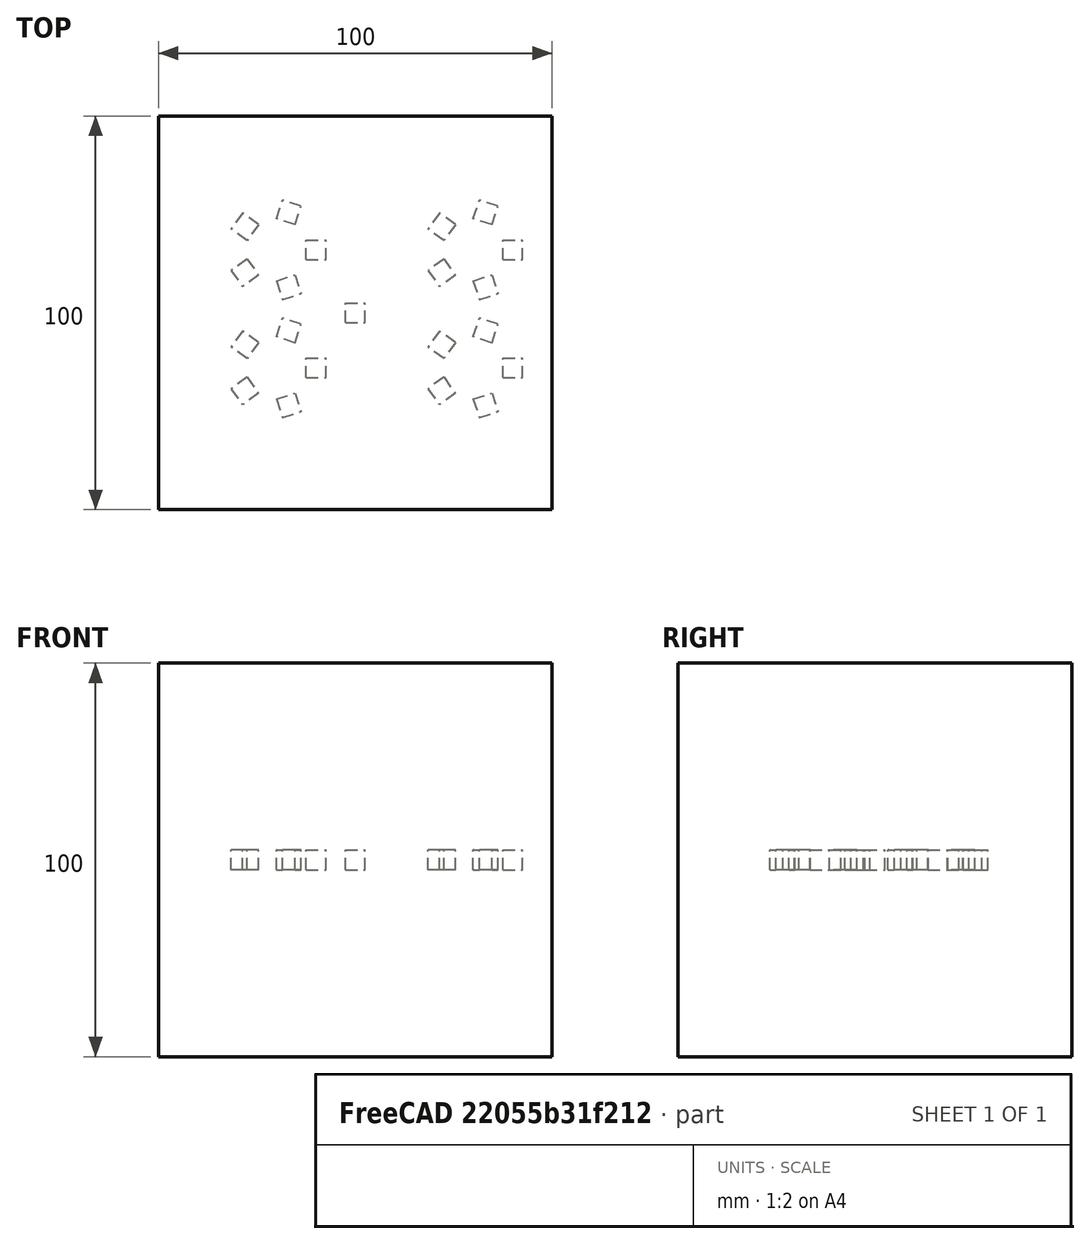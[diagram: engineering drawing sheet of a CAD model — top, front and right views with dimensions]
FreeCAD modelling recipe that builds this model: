
FCSTD DOCUMENT  (FreeCAD 1.0R39109 (Git))
Label: arrayTest-1
License: All rights reserved
LicenseURL: http://en.wikipedia.org/wiki/All_rights_reserved
objects: App::DocumentObjectGroupPython×1248, Part::FeaturePython×4, App::Part×3
note: 4 computed .brp shape members not serialized (recipe doc carries the construction recipe); baked Part::Feature solids carry a one-line shape summary decoded from their .brp

FEATURE [App::DocumentObjectGroupPython] HALFPI  # scripted group (container) (typed FeaturePython)
  name = HALFPI
  value = pi/2.
FEATURE [App::DocumentObjectGroupPython] PI  # scripted group (container) (typed FeaturePython)
  name = PI
  value = 1.*pi
FEATURE [App::DocumentObjectGroupPython] TWOPI  # scripted group (container) (typed FeaturePython)
  name = TWOPI
  value = 2.*pi
FEATURE [App::DocumentObjectGroupPython] Constants  # scripted group (container) (typed FeaturePython)
  Group = -> [HALFPI,PI,TWOPI]
FEATURE [App::DocumentObjectGroupPython] Variables  # scripted group (container) (typed FeaturePython)
FEATURE [App::DocumentObjectGroupPython] Quantities  # scripted group (container) (typed FeaturePython)
FEATURE [App::DocumentObjectGroupPython] Isotopes  # scripted group (container) (typed FeaturePython)
FEATURE [App::DocumentObjectGroupPython] Elements  # scripted group (container) (typed FeaturePython)
FEATURE [App::DocumentObjectGroupPython] G4Isotopes  # scripted group (container) (typed FeaturePython)
FEATURE [App::DocumentObjectGroupPython] H_element  # scripted group (container) (typed FeaturePython)
  Z = 1
  atom_value = 1.008
  formula = H
  name = H_element
FEATURE [App::DocumentObjectGroupPython] He_element  # scripted group (container) (typed FeaturePython)
  Z = 2
  atom_value = 4.0026
  formula = He
  name = He_element
FEATURE [App::DocumentObjectGroupPython] Li_element  # scripted group (container) (typed FeaturePython)
  Z = 3
  atom_value = 6.94
  formula = Li
  name = Li_element
FEATURE [App::DocumentObjectGroupPython] Be_element  # scripted group (container) (typed FeaturePython)
  Z = 4
  atom_value = 9.01218
  formula = Be
  name = Be_element
FEATURE [App::DocumentObjectGroupPython] B_element  # scripted group (container) (typed FeaturePython)
  Z = 5
  atom_value = 10.81
  formula = B
  name = B_element
FEATURE [App::DocumentObjectGroupPython] C_element  # scripted group (container) (typed FeaturePython)
  Z = 6
  atom_value = 12.011
  formula = C
  name = C_element
FEATURE [App::DocumentObjectGroupPython] N_element  # scripted group (container) (typed FeaturePython)
  Z = 7
  atom_value = 14.007
  formula = N
  name = N_element
FEATURE [App::DocumentObjectGroupPython] O_element  # scripted group (container) (typed FeaturePython)
  Z = 8
  atom_value = 15.999
  formula = O
  name = O_element
FEATURE [App::DocumentObjectGroupPython] F_element  # scripted group (container) (typed FeaturePython)
  Z = 9
  atom_value = 18.9984
  formula = F
  name = F_element
FEATURE [App::DocumentObjectGroupPython] Ne_element  # scripted group (container) (typed FeaturePython)
  Z = 10
  atom_value = 20.1797
  formula = Ne
  name = Ne_element
FEATURE [App::DocumentObjectGroupPython] Na_element  # scripted group (container) (typed FeaturePython)
  Z = 11
  atom_value = 22.9898
  formula = Na
  name = Na_element
FEATURE [App::DocumentObjectGroupPython] Mg_element  # scripted group (container) (typed FeaturePython)
  Z = 12
  atom_value = 24.305
  formula = Mg
  name = Mg_element
FEATURE [App::DocumentObjectGroupPython] Al_element  # scripted group (container) (typed FeaturePython)
  Z = 13
  atom_value = 26.9815
  formula = Al
  name = Al_element
FEATURE [App::DocumentObjectGroupPython] Si_element  # scripted group (container) (typed FeaturePython)
  Z = 14
  atom_value = 28.085
  formula = Si
  name = Si_element
FEATURE [App::DocumentObjectGroupPython] P_element  # scripted group (container) (typed FeaturePython)
  Z = 15
  atom_value = 30.9738
  formula = P
  name = P_element
FEATURE [App::DocumentObjectGroupPython] S_element  # scripted group (container) (typed FeaturePython)
  Z = 16
  atom_value = 32.06
  formula = S
  name = S_element
FEATURE [App::DocumentObjectGroupPython] Cl_element  # scripted group (container) (typed FeaturePython)
  Z = 17
  atom_value = 35.45
  formula = Cl
  name = Cl_element
FEATURE [App::DocumentObjectGroupPython] Ar_element  # scripted group (container) (typed FeaturePython)
  Z = 18
  atom_value = 39.95
  formula = Ar
  name = Ar_element
FEATURE [App::DocumentObjectGroupPython] K_element  # scripted group (container) (typed FeaturePython)
  Z = 19
  atom_value = 39.0983
  formula = K
  name = K_element
FEATURE [App::DocumentObjectGroupPython] Ca_element  # scripted group (container) (typed FeaturePython)
  Z = 20
  atom_value = 40.078
  formula = Ca
  name = Ca_element
FEATURE [App::DocumentObjectGroupPython] Sc_element  # scripted group (container) (typed FeaturePython)
  Z = 21
  atom_value = 44.9559
  formula = Sc
  name = Sc_element
FEATURE [App::DocumentObjectGroupPython] Ti_element  # scripted group (container) (typed FeaturePython)
  Z = 22
  atom_value = 47.867
  formula = Ti
  name = Ti_element
FEATURE [App::DocumentObjectGroupPython] V_element  # scripted group (container) (typed FeaturePython)
  Z = 23
  atom_value = 50.9415
  formula = V
  name = V_element
FEATURE [App::DocumentObjectGroupPython] Cr_element  # scripted group (container) (typed FeaturePython)
  Z = 24
  atom_value = 51.9961
  formula = Cr
  name = Cr_element
FEATURE [App::DocumentObjectGroupPython] Mn_element  # scripted group (container) (typed FeaturePython)
  Z = 25
  atom_value = 54.938
  formula = Mn
  name = Mn_element
FEATURE [App::DocumentObjectGroupPython] Fe_element  # scripted group (container) (typed FeaturePython)
  Z = 26
  atom_value = 55.845
  formula = Fe
  name = Fe_element
FEATURE [App::DocumentObjectGroupPython] Co_element  # scripted group (container) (typed FeaturePython)
  Z = 27
  atom_value = 58.9332
  formula = Co
  name = Co_element
FEATURE [App::DocumentObjectGroupPython] Ni_element  # scripted group (container) (typed FeaturePython)
  Z = 28
  atom_value = 58.6934
  formula = Ni
  name = Ni_element
FEATURE [App::DocumentObjectGroupPython] Cu_element  # scripted group (container) (typed FeaturePython)
  Z = 29
  atom_value = 63.546
  formula = Cu
  name = Cu_element
FEATURE [App::DocumentObjectGroupPython] Zn_element  # scripted group (container) (typed FeaturePython)
  Z = 30
  atom_value = 65.38
  formula = Zn
  name = Zn_element
FEATURE [App::DocumentObjectGroupPython] Ga_element  # scripted group (container) (typed FeaturePython)
  Z = 31
  atom_value = 69.723
  formula = Ga
  name = Ga_element
FEATURE [App::DocumentObjectGroupPython] Ge_element  # scripted group (container) (typed FeaturePython)
  Z = 32
  atom_value = 72.63
  formula = Ge
  name = Ge_element
FEATURE [App::DocumentObjectGroupPython] As_element  # scripted group (container) (typed FeaturePython)
  Z = 33
  atom_value = 74.9216
  formula = As
  name = As_element
FEATURE [App::DocumentObjectGroupPython] Se_element  # scripted group (container) (typed FeaturePython)
  Z = 34
  atom_value = 78.971
  formula = Se
  name = Se_element
FEATURE [App::DocumentObjectGroupPython] Br_element  # scripted group (container) (typed FeaturePython)
  Z = 35
  atom_value = 79.904
  formula = Br
  name = Br_element
FEATURE [App::DocumentObjectGroupPython] Kr_element  # scripted group (container) (typed FeaturePython)
  Z = 36
  atom_value = 83.798
  formula = Kr
  name = Kr_element
FEATURE [App::DocumentObjectGroupPython] Rb_element  # scripted group (container) (typed FeaturePython)
  Z = 37
  atom_value = 85.4678
  formula = Rb
  name = Rb_element
FEATURE [App::DocumentObjectGroupPython] Sr_element  # scripted group (container) (typed FeaturePython)
  Z = 38
  atom_value = 87.62
  formula = Sr
  name = Sr_element
FEATURE [App::DocumentObjectGroupPython] Y_element  # scripted group (container) (typed FeaturePython)
  Z = 39
  atom_value = 88.9058
  formula = Y
  name = Y_element
FEATURE [App::DocumentObjectGroupPython] Zr_element  # scripted group (container) (typed FeaturePython)
  Z = 40
  atom_value = 91.224
  formula = Zr
  name = Zr_element
FEATURE [App::DocumentObjectGroupPython] Nb_element  # scripted group (container) (typed FeaturePython)
  Z = 41
  atom_value = 92.9064
  formula = Nb
  name = Nb_element
FEATURE [App::DocumentObjectGroupPython] Mo_element  # scripted group (container) (typed FeaturePython)
  Z = 42
  atom_value = 95.95
  formula = Mo
  name = Mo_element
FEATURE [App::DocumentObjectGroupPython] Tc_element  # scripted group (container) (typed FeaturePython)
  Z = 43
  atom_value = 97
  formula = Tc
  name = Tc_element
FEATURE [App::DocumentObjectGroupPython] Ru_element  # scripted group (container) (typed FeaturePython)
  Z = 44
  atom_value = 101.07
  formula = Ru
  name = Ru_element
FEATURE [App::DocumentObjectGroupPython] Rh_element  # scripted group (container) (typed FeaturePython)
  Z = 45
  atom_value = 102.905
  formula = Rh
  name = Rh_element
FEATURE [App::DocumentObjectGroupPython] Pd_element  # scripted group (container) (typed FeaturePython)
  Z = 46
  atom_value = 106.42
  formula = Pd
  name = Pd_element
FEATURE [App::DocumentObjectGroupPython] Ag_element  # scripted group (container) (typed FeaturePython)
  Z = 47
  atom_value = 107.868
  formula = Ag
  name = Ag_element
FEATURE [App::DocumentObjectGroupPython] Cd_element  # scripted group (container) (typed FeaturePython)
  Z = 48
  atom_value = 112.414
  formula = Cd
  name = Cd_element
FEATURE [App::DocumentObjectGroupPython] In_element  # scripted group (container) (typed FeaturePython)
  Z = 49
  atom_value = 114.818
  formula = In
  name = In_element
FEATURE [App::DocumentObjectGroupPython] Sn_element  # scripted group (container) (typed FeaturePython)
  Z = 50
  atom_value = 118.71
  formula = Sn
  name = Sn_element
FEATURE [App::DocumentObjectGroupPython] Sb_element  # scripted group (container) (typed FeaturePython)
  Z = 51
  atom_value = 121.76
  formula = Sb
  name = Sb_element
FEATURE [App::DocumentObjectGroupPython] Te_element  # scripted group (container) (typed FeaturePython)
  Z = 52
  atom_value = 127.6
  formula = Te
  name = Te_element
FEATURE [App::DocumentObjectGroupPython] I_element  # scripted group (container) (typed FeaturePython)
  Z = 53
  atom_value = 126.904
  formula = I
  name = I_element
FEATURE [App::DocumentObjectGroupPython] Xe_element  # scripted group (container) (typed FeaturePython)
  Z = 54
  atom_value = 131.293
  formula = Xe
  name = Xe_element
FEATURE [App::DocumentObjectGroupPython] Cs_element  # scripted group (container) (typed FeaturePython)
  Z = 55
  atom_value = 132.905
  formula = Cs
  name = Cs_element
FEATURE [App::DocumentObjectGroupPython] Ba_element  # scripted group (container) (typed FeaturePython)
  Z = 56
  atom_value = 137.327
  formula = Ba
  name = Ba_element
FEATURE [App::DocumentObjectGroupPython] La_element  # scripted group (container) (typed FeaturePython)
  Z = 57
  atom_value = 138.905
  formula = La
  name = La_element
FEATURE [App::DocumentObjectGroupPython] Ce_element  # scripted group (container) (typed FeaturePython)
  Z = 58
  atom_value = 140.116
  formula = Ce
  name = Ce_element
FEATURE [App::DocumentObjectGroupPython] Pr_element  # scripted group (container) (typed FeaturePython)
  Z = 59
  atom_value = 140.908
  formula = Pr
  name = Pr_element
FEATURE [App::DocumentObjectGroupPython] Nd_element  # scripted group (container) (typed FeaturePython)
  Z = 60
  atom_value = 144.242
  formula = Nd
  name = Nd_element
FEATURE [App::DocumentObjectGroupPython] Pm_element  # scripted group (container) (typed FeaturePython)
  Z = 61
  atom_value = 145
  formula = Pm
  name = Pm_element
FEATURE [App::DocumentObjectGroupPython] Sm_element  # scripted group (container) (typed FeaturePython)
  Z = 62
  atom_value = 150.36
  formula = Sm
  name = Sm_element
FEATURE [App::DocumentObjectGroupPython] Eu_element  # scripted group (container) (typed FeaturePython)
  Z = 63
  atom_value = 151.964
  formula = Eu
  name = Eu_element
FEATURE [App::DocumentObjectGroupPython] Gd_element  # scripted group (container) (typed FeaturePython)
  Z = 64
  atom_value = 157.25
  formula = Gd
  name = Gd_element
FEATURE [App::DocumentObjectGroupPython] Tb_element  # scripted group (container) (typed FeaturePython)
  Z = 65
  atom_value = 158.925
  formula = Tb
  name = Tb_element
FEATURE [App::DocumentObjectGroupPython] Dy_element  # scripted group (container) (typed FeaturePython)
  Z = 66
  atom_value = 162.5
  formula = Dy
  name = Dy_element
FEATURE [App::DocumentObjectGroupPython] Ho_element  # scripted group (container) (typed FeaturePython)
  Z = 67
  atom_value = 164.93
  formula = Ho
  name = Ho_element
FEATURE [App::DocumentObjectGroupPython] Er_element  # scripted group (container) (typed FeaturePython)
  Z = 68
  atom_value = 167.259
  formula = Er
  name = Er_element
FEATURE [App::DocumentObjectGroupPython] Tm_element  # scripted group (container) (typed FeaturePython)
  Z = 69
  atom_value = 168.934
  formula = Tm
  name = Tm_element
FEATURE [App::DocumentObjectGroupPython] Yb_element  # scripted group (container) (typed FeaturePython)
  Z = 70
  atom_value = 173.045
  formula = Yb
  name = Yb_element
FEATURE [App::DocumentObjectGroupPython] Lu_element  # scripted group (container) (typed FeaturePython)
  Z = 71
  atom_value = 174.967
  formula = Lu
  name = Lu_element
FEATURE [App::DocumentObjectGroupPython] Hf_element  # scripted group (container) (typed FeaturePython)
  Z = 72
  atom_value = 178.49
  formula = Hf
  name = Hf_element
FEATURE [App::DocumentObjectGroupPython] Ta_element  # scripted group (container) (typed FeaturePython)
  Z = 73
  atom_value = 180.948
  formula = Ta
  name = Ta_element
FEATURE [App::DocumentObjectGroupPython] W_element  # scripted group (container) (typed FeaturePython)
  Z = 74
  atom_value = 183.84
  formula = W
  name = W_element
FEATURE [App::DocumentObjectGroupPython] Re_element  # scripted group (container) (typed FeaturePython)
  Z = 75
  atom_value = 186.207
  formula = Re
  name = Re_element
FEATURE [App::DocumentObjectGroupPython] Os_element  # scripted group (container) (typed FeaturePython)
  Z = 76
  atom_value = 190.23
  formula = Os
  name = Os_element
FEATURE [App::DocumentObjectGroupPython] Ir_element  # scripted group (container) (typed FeaturePython)
  Z = 77
  atom_value = 192.217
  formula = Ir
  name = Ir_element
FEATURE [App::DocumentObjectGroupPython] Pt_element  # scripted group (container) (typed FeaturePython)
  Z = 78
  atom_value = 195.084
  formula = Pt
  name = Pt_element
FEATURE [App::DocumentObjectGroupPython] Au_element  # scripted group (container) (typed FeaturePython)
  Z = 79
  atom_value = 196.967
  formula = Au
  name = Au_element
FEATURE [App::DocumentObjectGroupPython] Hg_element  # scripted group (container) (typed FeaturePython)
  Z = 80
  atom_value = 200.592
  formula = Hg
  name = Hg_element
FEATURE [App::DocumentObjectGroupPython] Tl_element  # scripted group (container) (typed FeaturePython)
  Z = 81
  atom_value = 204.38
  formula = Tl
  name = Tl_element
FEATURE [App::DocumentObjectGroupPython] Pb_element  # scripted group (container) (typed FeaturePython)
  Z = 82
  atom_value = 207.2
  formula = Pb
  name = Pb_element
FEATURE [App::DocumentObjectGroupPython] Bi_element  # scripted group (container) (typed FeaturePython)
  Z = 83
  atom_value = 208.98
  formula = Bi
  name = Bi_element
FEATURE [App::DocumentObjectGroupPython] Po_element  # scripted group (container) (typed FeaturePython)
  Z = 84
  atom_value = 209
  formula = Po
  name = Po_element
FEATURE [App::DocumentObjectGroupPython] At_element  # scripted group (container) (typed FeaturePython)
  Z = 85
  atom_value = 210
  formula = At
  name = At_element
FEATURE [App::DocumentObjectGroupPython] Rn_element  # scripted group (container) (typed FeaturePython)
  Z = 86
  atom_value = 222
  formula = Rn
  name = Rn_element
FEATURE [App::DocumentObjectGroupPython] Fr_element  # scripted group (container) (typed FeaturePython)
  Z = 87
  atom_value = 223
  formula = Fr
  name = Fr_element
FEATURE [App::DocumentObjectGroupPython] Ra_element  # scripted group (container) (typed FeaturePython)
  Z = 88
  atom_value = 226
  formula = Ra
  name = Ra_element
FEATURE [App::DocumentObjectGroupPython] Ac_element  # scripted group (container) (typed FeaturePython)
  Z = 89
  atom_value = 227
  formula = Ac
  name = Ac_element
FEATURE [App::DocumentObjectGroupPython] Th_element  # scripted group (container) (typed FeaturePython)
  Z = 90
  atom_value = 232.038
  formula = Th
  name = Th_element
FEATURE [App::DocumentObjectGroupPython] Pa_element  # scripted group (container) (typed FeaturePython)
  Z = 91
  atom_value = 231.036
  formula = Pa
  name = Pa_element
FEATURE [App::DocumentObjectGroupPython] U_element  # scripted group (container) (typed FeaturePython)
  Z = 92
  atom_value = 238.029
  formula = U
  name = U_element
FEATURE [App::DocumentObjectGroupPython] Np_element  # scripted group (container) (typed FeaturePython)
  Z = 93
  atom_value = 237
  formula = Np
  name = Np_element
FEATURE [App::DocumentObjectGroupPython] Pu_element  # scripted group (container) (typed FeaturePython)
  Z = 94
  atom_value = 244
  formula = Pu
  name = Pu_element
FEATURE [App::DocumentObjectGroupPython] Am_element  # scripted group (container) (typed FeaturePython)
  Z = 95
  atom_value = 243
  formula = Am
  name = Am_element
FEATURE [App::DocumentObjectGroupPython] Cm_element  # scripted group (container) (typed FeaturePython)
  Z = 96
  atom_value = 247
  formula = Cm
  name = Cm_element
FEATURE [App::DocumentObjectGroupPython] Bk_element  # scripted group (container) (typed FeaturePython)
  Z = 97
  atom_value = 247
  formula = Bk
  name = Bk_element
FEATURE [App::DocumentObjectGroupPython] Cf_element  # scripted group (container) (typed FeaturePython)
  Z = 98
  atom_value = 251
  formula = Cf
  name = Cf_element
FEATURE [App::DocumentObjectGroupPython] G4Elements  # scripted group (container) (typed FeaturePython)
  Group = -> [H_element,He_element,Li_element,Be_element,B_element,C_element,N_element,O_element,F_element,Ne_element,Na_element,Mg_element,Al_element,Si_element,P_element,S_element,Cl_element,Ar_element,K_element,Ca_element,Sc_element,Ti_element,V_element,Cr_element,Mn_element,Fe_element,Co_element,Ni_element,Cu_element,Zn_element,Ga_element,Ge_element,As_element,Se_element,Br_element,Kr_element,Rb_element,+61 more]
FEATURE [App::DocumentObjectGroupPython] H_element001  label="H_element : 0.101"  # scripted group (container) (typed FeaturePython)
  n = 0.101327
FEATURE [App::DocumentObjectGroupPython] C_element001  label="C_element : 0.775"  # scripted group (container) (typed FeaturePython)
  n = 0.7755
FEATURE [App::DocumentObjectGroupPython] N_element001  label="N_element : 0.035"  # scripted group (container) (typed FeaturePython)
  n = 0.035057
FEATURE [App::DocumentObjectGroupPython] O_element001  label="O_element : 0.052"  # scripted group (container) (typed FeaturePython)
  n = 0.0523159
FEATURE [App::DocumentObjectGroupPython] F_element001  label="F_element : 0.017"  # scripted group (container) (typed FeaturePython)
  n = 0.017422
FEATURE [App::DocumentObjectGroupPython] Ca_element001  label="Ca_element : 0.018"  # scripted group (container) (typed FeaturePython)
  n = 0.018378
FEATURE [App::DocumentObjectGroupPython] G4_A_150_TISSUE  label="G4_A-150_TISSUE"  # scripted group (container) (typed FeaturePython)
  Dunit = g/cm3
  Dvalue = 1.127
  Group = -> [H_element001,C_element001,N_element001,O_element001,F_element001,Ca_element001]
  conduct = 2
  density = 1
  expand = 3
  formula = G4_A-150_TISSUE
  name = G4_A-150_TISSUE
  specific = 4
FEATURE [App::DocumentObjectGroupPython] C_element002  label="C_element : 3"  # scripted group (container) (typed FeaturePython)
  n = 3
  ref = C_element
FEATURE [App::DocumentObjectGroupPython] H_element002  label="H_element : 6"  # scripted group (container) (typed FeaturePython)
  n = 6
  ref = H_element
FEATURE [App::DocumentObjectGroupPython] O_element002  label="O_element : 1"  # scripted group (container) (typed FeaturePython)
  n = 1
  ref = O_element
FEATURE [App::DocumentObjectGroupPython] G4_ACETONE  # scripted group (container) (typed FeaturePython)
  Dunit = g/cm3
  Dvalue = 0.7899
  Group = -> [C_element002,H_element002,O_element002]
  conduct = 2
  density = 1
  expand = 3
  formula = G4_ACETONE
  name = G4_ACETONE
  specific = 4
FEATURE [App::DocumentObjectGroupPython] C_element003  label="C_element : 2"  # scripted group (container) (typed FeaturePython)
  n = 2
  ref = C_element
FEATURE [App::DocumentObjectGroupPython] H_element003  label="H_element : 2"  # scripted group (container) (typed FeaturePython)
  n = 2
  ref = H_element
FEATURE [App::DocumentObjectGroupPython] G4_ACETYLENE  # scripted group (container) (typed FeaturePython)
  Dunit = g/cm3
  Dvalue = 0.0010967
  Group = -> [C_element003,H_element003]
  conduct = 2
  density = 1
  expand = 3
  formula = G4_ACETYLENE
  name = G4_ACETYLENE
  specific = 4
FEATURE [App::DocumentObjectGroupPython] C_element004  label="C_element : 5"  # scripted group (container) (typed FeaturePython)
  n = 5
  ref = C_element
FEATURE [App::DocumentObjectGroupPython] H_element004  label="H_element : 5"  # scripted group (container) (typed FeaturePython)
  n = 5
  ref = H_element
FEATURE [App::DocumentObjectGroupPython] N_element002  label="N_element : 5"  # scripted group (container) (typed FeaturePython)
  n = 5
  ref = N_element
FEATURE [App::DocumentObjectGroupPython] G4_ADENINE  # scripted group (container) (typed FeaturePython)
  Dunit = g/cm3
  Dvalue = 1.6
  Group = -> [C_element004,H_element004,N_element002]
  conduct = 2
  density = 1
  expand = 3
  formula = G4_ADENINE
  name = G4_ADENINE
  specific = 4
FEATURE [App::DocumentObjectGroupPython] H_element005  label="H_element : 0.114"  # scripted group (container) (typed FeaturePython)
  n = 0.114
FEATURE [App::DocumentObjectGroupPython] C_element005  label="C_element : 0.598"  # scripted group (container) (typed FeaturePython)
  n = 0.598
FEATURE [App::DocumentObjectGroupPython] N_element003  label="N_element : 0.007"  # scripted group (container) (typed FeaturePython)
  n = 0.007
FEATURE [App::DocumentObjectGroupPython] O_element003  label="O_element : 0.278"  # scripted group (container) (typed FeaturePython)
  n = 0.278
FEATURE [App::DocumentObjectGroupPython] Na_element001  label="Na_element : 0.001"  # scripted group (container) (typed FeaturePython)
  n = 0.001
FEATURE [App::DocumentObjectGroupPython] S_element001  label="S_element : 0.001"  # scripted group (container) (typed FeaturePython)
  n = 0.001
FEATURE [App::DocumentObjectGroupPython] Cl_element001  label="Cl_element : 0.001"  # scripted group (container) (typed FeaturePython)
  n = 0.001
FEATURE [App::DocumentObjectGroupPython] G4_ADIPOSE_TISSUE_ICRP  # scripted group (container) (typed FeaturePython)
  Dunit = g/cm3
  Dvalue = 0.95
  Group = -> [H_element005,C_element005,N_element003,O_element003,Na_element001,S_element001,Cl_element001]
  conduct = 2
  density = 1
  expand = 3
  formula = G4_ADIPOSE_TISSUE_ICRP
  name = G4_ADIPOSE_TISSUE_ICRP
  specific = 4
FEATURE [App::DocumentObjectGroupPython] C_element006  label="C_element : 0.000"  # scripted group (container) (typed FeaturePython)
  n = 0.000124
FEATURE [App::DocumentObjectGroupPython] N_element004  label="N_element : 0.755"  # scripted group (container) (typed FeaturePython)
  n = 0.755268
FEATURE [App::DocumentObjectGroupPython] O_element004  label="O_element : 0.232"  # scripted group (container) (typed FeaturePython)
  n = 0.231781
FEATURE [App::DocumentObjectGroupPython] Ar_element001  label="Ar_element : 0.013"  # scripted group (container) (typed FeaturePython)
  n = 0.012827
FEATURE [App::DocumentObjectGroupPython] G4_AIR  # scripted group (container) (typed FeaturePython)
  Dunit = g/cm3
  Dvalue = 0.00120479
  Group = -> [C_element006,N_element004,O_element004,Ar_element001]
  conduct = 2
  density = 1
  expand = 3
  formula = G4_AIR
  name = G4_AIR
  specific = 4
FEATURE [App::DocumentObjectGroupPython] C_element007  label="C_element : 006"  # scripted group (container) (typed FeaturePython)
  n = 3
  ref = C_element
FEATURE [App::DocumentObjectGroupPython] H_element006  label="H_element : 7"  # scripted group (container) (typed FeaturePython)
  n = 7
  ref = H_element
FEATURE [App::DocumentObjectGroupPython] N_element005  label="N_element : 1"  # scripted group (container) (typed FeaturePython)
  n = 1
  ref = N_element
FEATURE [App::DocumentObjectGroupPython] O_element005  label="O_element : 2"  # scripted group (container) (typed FeaturePython)
  n = 2
  ref = O_element
FEATURE [App::DocumentObjectGroupPython] G4_ALANINE  # scripted group (container) (typed FeaturePython)
  Dunit = g/cm3
  Dvalue = 1.42
  Group = -> [C_element007,H_element006,N_element005,O_element005]
  conduct = 2
  density = 1
  expand = 3
  formula = G4_ALANINE
  name = G4_ALANINE
  specific = 4
FEATURE [App::DocumentObjectGroupPython] Al_element001  label="Al_element : 2"  # scripted group (container) (typed FeaturePython)
  n = 2
  ref = Al_element
FEATURE [App::DocumentObjectGroupPython] O_element006  label="O_element : 3"  # scripted group (container) (typed FeaturePython)
  n = 3
  ref = O_element
FEATURE [App::DocumentObjectGroupPython] G4_ALUMINUM_OXIDE  # scripted group (container) (typed FeaturePython)
  Dunit = g/cm3
  Dvalue = 3.97
  Group = -> [Al_element001,O_element006]
  conduct = 2
  density = 1
  expand = 3
  formula = G4_ALUMINUM_OXIDE
  name = G4_ALUMINUM_OXIDE
  specific = 4
FEATURE [App::DocumentObjectGroupPython] H_element007  label="H_element : 0.106"  # scripted group (container) (typed FeaturePython)
  n = 0.10593
FEATURE [App::DocumentObjectGroupPython] C_element008  label="C_element : 0.789"  # scripted group (container) (typed FeaturePython)
  n = 0.788974
FEATURE [App::DocumentObjectGroupPython] O_element007  label="O_element : 0.105"  # scripted group (container) (typed FeaturePython)
  n = 0.105096
FEATURE [App::DocumentObjectGroupPython] G4_AMBER  # scripted group (container) (typed FeaturePython)
  Dunit = g/cm3
  Dvalue = 1.1
  Group = -> [H_element007,C_element008,O_element007]
  conduct = 2
  density = 1
  expand = 3
  formula = G4_AMBER
  name = G4_AMBER
  specific = 4
FEATURE [App::DocumentObjectGroupPython] N_element006  label="N_element : 006"  # scripted group (container) (typed FeaturePython)
  n = 1
  ref = N_element
FEATURE [App::DocumentObjectGroupPython] H_element008  label="H_element : 3"  # scripted group (container) (typed FeaturePython)
  n = 3
  ref = H_element
FEATURE [App::DocumentObjectGroupPython] G4_AMMONIA  # scripted group (container) (typed FeaturePython)
  Dunit = g/cm3
  Dvalue = 0.000826019
  Group = -> [N_element006,H_element008]
  conduct = 2
  density = 1
  expand = 3
  formula = G4_AMMONIA
  name = G4_AMMONIA
  specific = 4
FEATURE [App::DocumentObjectGroupPython] C_element009  label="C_element : 6"  # scripted group (container) (typed FeaturePython)
  n = 6
  ref = C_element
FEATURE [App::DocumentObjectGroupPython] H_element009  label="H_element : 008"  # scripted group (container) (typed FeaturePython)
  n = 7
  ref = H_element
FEATURE [App::DocumentObjectGroupPython] N_element007  label="N_element : 007"  # scripted group (container) (typed FeaturePython)
  n = 1
  ref = N_element
FEATURE [App::DocumentObjectGroupPython] G4_ANILINE  # scripted group (container) (typed FeaturePython)
  Dunit = g/cm3
  Dvalue = 1.0235
  Group = -> [C_element009,H_element009,N_element007]
  conduct = 2
  density = 1
  expand = 3
  formula = G4_ANILINE
  name = G4_ANILINE
  specific = 4
FEATURE [App::DocumentObjectGroupPython] C_element010  label="C_element : 14"  # scripted group (container) (typed FeaturePython)
  n = 14
  ref = C_element
FEATURE [App::DocumentObjectGroupPython] H_element010  label="H_element : 10"  # scripted group (container) (typed FeaturePython)
  n = 10
  ref = H_element
FEATURE [App::DocumentObjectGroupPython] G4_ANTHRACENE  # scripted group (container) (typed FeaturePython)
  Dunit = g/cm3
  Dvalue = 1.283
  Group = -> [C_element010,H_element010]
  conduct = 2
  density = 1
  expand = 3
  formula = G4_ANTHRACENE
  name = G4_ANTHRACENE
  specific = 4
FEATURE [App::DocumentObjectGroupPython] H_element011  label="H_element : 0.065"  # scripted group (container) (typed FeaturePython)
  n = 0.0654709
FEATURE [App::DocumentObjectGroupPython] C_element011  label="C_element : 0.537"  # scripted group (container) (typed FeaturePython)
  n = 0.536944
FEATURE [App::DocumentObjectGroupPython] N_element008  label="N_element : 0.021"  # scripted group (container) (typed FeaturePython)
  n = 0.0215
FEATURE [App::DocumentObjectGroupPython] O_element008  label="O_element : 0.032"  # scripted group (container) (typed FeaturePython)
  n = 0.032085
FEATURE [App::DocumentObjectGroupPython] F_element002  label="F_element : 0.167"  # scripted group (container) (typed FeaturePython)
  n = 0.167411
FEATURE [App::DocumentObjectGroupPython] Ca_element002  label="Ca_element : 0.177"  # scripted group (container) (typed FeaturePython)
  n = 0.176589
FEATURE [App::DocumentObjectGroupPython] G4_B_100_BONE  label="G4_B-100_BONE"  # scripted group (container) (typed FeaturePython)
  Dunit = g/cm3
  Dvalue = 1.45
  Group = -> [H_element011,C_element011,N_element008,O_element008,F_element002,Ca_element002]
  conduct = 2
  density = 1
  expand = 3
  formula = G4_B-100_BONE
  name = G4_B-100_BONE
  specific = 4
FEATURE [App::DocumentObjectGroupPython] H_element012  label="H_element : 0.057"  # scripted group (container) (typed FeaturePython)
  n = 0.057441
FEATURE [App::DocumentObjectGroupPython] C_element012  label="C_element : 0.790"  # scripted group (container) (typed FeaturePython)
  n = 0.774591
FEATURE [App::DocumentObjectGroupPython] O_element009  label="O_element : 0.168"  # scripted group (container) (typed FeaturePython)
  n = 0.167968
FEATURE [App::DocumentObjectGroupPython] G4_BAKELITE  # scripted group (container) (typed FeaturePython)
  Dunit = g/cm3
  Dvalue = 1.25
  Group = -> [H_element012,C_element012,O_element009]
  conduct = 2
  density = 1
  expand = 3
  formula = G4_BAKELITE
  name = G4_BAKELITE
  specific = 4
FEATURE [App::DocumentObjectGroupPython] Ba_element001  label="Ba_element : 1"  # scripted group (container) (typed FeaturePython)
  n = 1
  ref = Ba_element
FEATURE [App::DocumentObjectGroupPython] F_element003  label="F_element : 2"  # scripted group (container) (typed FeaturePython)
  n = 2
  ref = F_element
FEATURE [App::DocumentObjectGroupPython] G4_BARIUM_FLUORIDE  # scripted group (container) (typed FeaturePython)
  Dunit = g/cm3
  Dvalue = 4.89
  Group = -> [Ba_element001,F_element003]
  conduct = 2
  density = 1
  expand = 3
  formula = G4_BARIUM_FLUORIDE
  name = G4_BARIUM_FLUORIDE
  specific = 4
FEATURE [App::DocumentObjectGroupPython] Ba_element002  label="Ba_element : 002"  # scripted group (container) (typed FeaturePython)
  n = 1
  ref = Ba_element
FEATURE [App::DocumentObjectGroupPython] S_element002  label="S_element : 1"  # scripted group (container) (typed FeaturePython)
  n = 1
  ref = S_element
FEATURE [App::DocumentObjectGroupPython] O_element010  label="O_element : 4"  # scripted group (container) (typed FeaturePython)
  n = 4
  ref = O_element
FEATURE [App::DocumentObjectGroupPython] G4_BARIUM_SULFATE  # scripted group (container) (typed FeaturePython)
  Dunit = g/cm3
  Dvalue = 4.5
  Group = -> [Ba_element002,S_element002,O_element010]
  conduct = 2
  density = 1
  expand = 3
  formula = G4_BARIUM_SULFATE
  name = G4_BARIUM_SULFATE
  specific = 4
FEATURE [App::DocumentObjectGroupPython] C_element013  label="C_element : 007"  # scripted group (container) (typed FeaturePython)
  n = 6
  ref = C_element
FEATURE [App::DocumentObjectGroupPython] H_element013  label="H_element : 009"  # scripted group (container) (typed FeaturePython)
  n = 6
  ref = H_element
FEATURE [App::DocumentObjectGroupPython] G4_BENZENE  # scripted group (container) (typed FeaturePython)
  Dunit = g/cm3
  Dvalue = 0.87865
  Group = -> [C_element013,H_element013]
  conduct = 2
  density = 1
  expand = 3
  formula = G4_BENZENE
  name = G4_BENZENE
  specific = 4
FEATURE [App::DocumentObjectGroupPython] Be_element001  label="Be_element : 1"  # scripted group (container) (typed FeaturePython)
  n = 1
  ref = Be_element
FEATURE [App::DocumentObjectGroupPython] O_element011  label="O_element : 005"  # scripted group (container) (typed FeaturePython)
  n = 1
  ref = O_element
FEATURE [App::DocumentObjectGroupPython] G4_BERYLLIUM_OXIDE  # scripted group (container) (typed FeaturePython)
  Dunit = g/cm3
  Dvalue = 3.01
  Group = -> [Be_element001,O_element011]
  conduct = 2
  density = 1
  expand = 3
  formula = G4_BERYLLIUM_OXIDE
  name = G4_BERYLLIUM_OXIDE
  specific = 4
FEATURE [App::DocumentObjectGroupPython] Bi_element001  label="Bi_element : 4"  # scripted group (container) (typed FeaturePython)
  n = 4
  ref = Bi_element
FEATURE [App::DocumentObjectGroupPython] Ge_element001  label="Ge_element : 3"  # scripted group (container) (typed FeaturePython)
  n = 3
  ref = Ge_element
FEATURE [App::DocumentObjectGroupPython] O_element012  label="O_element : 12"  # scripted group (container) (typed FeaturePython)
  n = 12
  ref = O_element
FEATURE [App::DocumentObjectGroupPython] G4_BGO  # scripted group (container) (typed FeaturePython)
  Dunit = g/cm3
  Dvalue = 7.13
  Group = -> [Bi_element001,Ge_element001,O_element012]
  conduct = 2
  density = 1
  expand = 3
  formula = G4_BGO
  name = G4_BGO
  specific = 4
FEATURE [App::DocumentObjectGroupPython] H_element014  label="H_element : 0.102"  # scripted group (container) (typed FeaturePython)
  n = 0.102
FEATURE [App::DocumentObjectGroupPython] C_element014  label="C_element : 0.110"  # scripted group (container) (typed FeaturePython)
  n = 0.11
FEATURE [App::DocumentObjectGroupPython] N_element009  label="N_element : 0.033"  # scripted group (container) (typed FeaturePython)
  n = 0.033
FEATURE [App::DocumentObjectGroupPython] O_element013  label="O_element : 0.745"  # scripted group (container) (typed FeaturePython)
  n = 0.745
FEATURE [App::DocumentObjectGroupPython] Na_element002  label="Na_element : 0.002"  # scripted group (container) (typed FeaturePython)
  n = 0.001
FEATURE [App::DocumentObjectGroupPython] P_element001  label="P_element : 0.001"  # scripted group (container) (typed FeaturePython)
  n = 0.001
FEATURE [App::DocumentObjectGroupPython] S_element003  label="S_element : 0.002"  # scripted group (container) (typed FeaturePython)
  n = 0.002
FEATURE [App::DocumentObjectGroupPython] Cl_element002  label="Cl_element : 0.003"  # scripted group (container) (typed FeaturePython)
  n = 0.003
FEATURE [App::DocumentObjectGroupPython] K_element001  label="K_element : 0.002"  # scripted group (container) (typed FeaturePython)
  n = 0.002
FEATURE [App::DocumentObjectGroupPython] Fe_element001  label="Fe_element : 0.001"  # scripted group (container) (typed FeaturePython)
  n = 0.001
FEATURE [App::DocumentObjectGroupPython] G4_BLOOD_ICRP  # scripted group (container) (typed FeaturePython)
  Dunit = g/cm3
  Dvalue = 1.06
  Group = -> [H_element014,C_element014,N_element009,O_element013,Na_element002,P_element001,S_element003,Cl_element002,K_element001,Fe_element001]
  conduct = 2
  density = 1
  expand = 3
  formula = G4_BLOOD_ICRP
  name = G4_BLOOD_ICRP
  specific = 4
FEATURE [App::DocumentObjectGroupPython] H_element015  label="H_element : 0.064"  # scripted group (container) (typed FeaturePython)
  n = 0.064
FEATURE [App::DocumentObjectGroupPython] C_element015  label="C_element : 0.278"  # scripted group (container) (typed FeaturePython)
  n = 0.278
FEATURE [App::DocumentObjectGroupPython] N_element010  label="N_element : 0.027"  # scripted group (container) (typed FeaturePython)
  n = 0.027
FEATURE [App::DocumentObjectGroupPython] O_element014  label="O_element : 0.410"  # scripted group (container) (typed FeaturePython)
  n = 0.41
FEATURE [App::DocumentObjectGroupPython] Mg_element001  label="Mg_element : 0.002"  # scripted group (container) (typed FeaturePython)
  n = 0.002
FEATURE [App::DocumentObjectGroupPython] P_element002  label="P_element : 0.070"  # scripted group (container) (typed FeaturePython)
  n = 0.07
FEATURE [App::DocumentObjectGroupPython] S_element004  label="S_element : 0.003"  # scripted group (container) (typed FeaturePython)
  n = 0.002
FEATURE [App::DocumentObjectGroupPython] Ca_element003  label="Ca_element : 0.147"  # scripted group (container) (typed FeaturePython)
  n = 0.147
FEATURE [App::DocumentObjectGroupPython] G4_BONE_COMPACT_ICRU  # scripted group (container) (typed FeaturePython)
  Dunit = g/cm3
  Dvalue = 1.85
  Group = -> [H_element015,C_element015,N_element010,O_element014,Mg_element001,P_element002,S_element004,Ca_element003]
  conduct = 2
  density = 1
  expand = 3
  formula = G4_BONE_COMPACT_ICRU
  name = G4_BONE_COMPACT_ICRU
  specific = 4
FEATURE [App::DocumentObjectGroupPython] H_element016  label="H_element : 0.034"  # scripted group (container) (typed FeaturePython)
  n = 0.034
FEATURE [App::DocumentObjectGroupPython] C_element016  label="C_element : 0.155"  # scripted group (container) (typed FeaturePython)
  n = 0.155
FEATURE [App::DocumentObjectGroupPython] N_element011  label="N_element : 0.042"  # scripted group (container) (typed FeaturePython)
  n = 0.042
FEATURE [App::DocumentObjectGroupPython] O_element015  label="O_element : 0.435"  # scripted group (container) (typed FeaturePython)
  n = 0.435
FEATURE [App::DocumentObjectGroupPython] Na_element003  label="Na_element : 0.003"  # scripted group (container) (typed FeaturePython)
  n = 0.001
FEATURE [App::DocumentObjectGroupPython] Mg_element002  label="Mg_element : 0.003"  # scripted group (container) (typed FeaturePython)
  n = 0.002
FEATURE [App::DocumentObjectGroupPython] P_element003  label="P_element : 0.103"  # scripted group (container) (typed FeaturePython)
  n = 0.103
FEATURE [App::DocumentObjectGroupPython] S_element005  label="S_element : 0.004"  # scripted group (container) (typed FeaturePython)
  n = 0.003
FEATURE [App::DocumentObjectGroupPython] Ca_element004  label="Ca_element : 0.225"  # scripted group (container) (typed FeaturePython)
  n = 0.225
FEATURE [App::DocumentObjectGroupPython] G4_BONE_CORTICAL_ICRP  # scripted group (container) (typed FeaturePython)
  Dunit = g/cm3
  Dvalue = 1.92
  Group = -> [H_element016,C_element016,N_element011,O_element015,Na_element003,Mg_element002,P_element003,S_element005,Ca_element004]
  conduct = 2
  density = 1
  expand = 3
  formula = G4_BONE_CORTICAL_ICRP
  name = G4_BONE_CORTICAL_ICRP
  specific = 4
FEATURE [App::DocumentObjectGroupPython] B_element001  label="B_element : 4"  # scripted group (container) (typed FeaturePython)
  n = 4
  ref = B_element
FEATURE [App::DocumentObjectGroupPython] C_element017  label="C_element : 1"  # scripted group (container) (typed FeaturePython)
  n = 1
  ref = C_element
FEATURE [App::DocumentObjectGroupPython] G4_BORON_CARBIDE  # scripted group (container) (typed FeaturePython)
  Dunit = g/cm3
  Dvalue = 2.52
  Group = -> [B_element001,C_element017]
  conduct = 2
  density = 1
  expand = 3
  formula = G4_BORON_CARBIDE
  name = G4_BORON_CARBIDE
  specific = 4
FEATURE [App::DocumentObjectGroupPython] B_element002  label="B_element : 2"  # scripted group (container) (typed FeaturePython)
  n = 2
  ref = B_element
FEATURE [App::DocumentObjectGroupPython] O_element016  label="O_element : 006"  # scripted group (container) (typed FeaturePython)
  n = 3
  ref = O_element
FEATURE [App::DocumentObjectGroupPython] G4_BORON_OXIDE  # scripted group (container) (typed FeaturePython)
  Dunit = g/cm3
  Dvalue = 1.812
  Group = -> [B_element002,O_element016]
  conduct = 2
  density = 1
  expand = 3
  formula = G4_BORON_OXIDE
  name = G4_BORON_OXIDE
  specific = 4
FEATURE [App::DocumentObjectGroupPython] H_element017  label="H_element : 0.107"  # scripted group (container) (typed FeaturePython)
  n = 0.107
FEATURE [App::DocumentObjectGroupPython] C_element018  label="C_element : 0.145"  # scripted group (container) (typed FeaturePython)
  n = 0.145
FEATURE [App::DocumentObjectGroupPython] N_element012  label="N_element : 0.022"  # scripted group (container) (typed FeaturePython)
  n = 0.022
FEATURE [App::DocumentObjectGroupPython] O_element017  label="O_element : 0.712"  # scripted group (container) (typed FeaturePython)
  n = 0.712
FEATURE [App::DocumentObjectGroupPython] Na_element004  label="Na_element : 0.004"  # scripted group (container) (typed FeaturePython)
  n = 0.002
FEATURE [App::DocumentObjectGroupPython] P_element004  label="P_element : 0.004"  # scripted group (container) (typed FeaturePython)
  n = 0.004
FEATURE [App::DocumentObjectGroupPython] S_element006  label="S_element : 0.005"  # scripted group (container) (typed FeaturePython)
  n = 0.002
FEATURE [App::DocumentObjectGroupPython] Cl_element003  label="Cl_element : 0.004"  # scripted group (container) (typed FeaturePython)
  n = 0.003
FEATURE [App::DocumentObjectGroupPython] K_element002  label="K_element : 0.003"  # scripted group (container) (typed FeaturePython)
  n = 0.003
FEATURE [App::DocumentObjectGroupPython] G4_BRAIN_ICRP  # scripted group (container) (typed FeaturePython)
  Dunit = g/cm3
  Dvalue = 1.04
  Group = -> [H_element017,C_element018,N_element012,O_element017,Na_element004,P_element004,S_element006,Cl_element003,K_element002]
  conduct = 2
  density = 1
  expand = 3
  formula = G4_BRAIN_ICRP
  name = G4_BRAIN_ICRP
  specific = 4
FEATURE [App::DocumentObjectGroupPython] C_element019  label="C_element : 4"  # scripted group (container) (typed FeaturePython)
  n = 4
  ref = C_element
FEATURE [App::DocumentObjectGroupPython] H_element018  label="H_element : 010"  # scripted group (container) (typed FeaturePython)
  n = 10
  ref = H_element
FEATURE [App::DocumentObjectGroupPython] G4_BUTANE  # scripted group (container) (typed FeaturePython)
  Dunit = g/cm3
  Dvalue = 0.00249343
  Group = -> [C_element019,H_element018]
  conduct = 2
  density = 1
  expand = 3
  formula = G4_BUTANE
  name = G4_BUTANE
  specific = 4
FEATURE [App::DocumentObjectGroupPython] C_element020  label="C_element : 008"  # scripted group (container) (typed FeaturePython)
  n = 4
  ref = C_element
FEATURE [App::DocumentObjectGroupPython] H_element019  label="H_element : 011"  # scripted group (container) (typed FeaturePython)
  n = 10
  ref = H_element
FEATURE [App::DocumentObjectGroupPython] O_element018  label="O_element : 007"  # scripted group (container) (typed FeaturePython)
  n = 1
  ref = O_element
FEATURE [App::DocumentObjectGroupPython] G4_N_BUTYL_ALCOHOL  label="G4_N-BUTYL_ALCOHOL"  # scripted group (container) (typed FeaturePython)
  Dunit = g/cm3
  Dvalue = 0.8098
  Group = -> [C_element020,H_element019,O_element018]
  conduct = 2
  density = 1
  expand = 3
  formula = G4_N-BUTYL_ALCOHOL
  name = G4_N-BUTYL_ALCOHOL
  specific = 4
FEATURE [App::DocumentObjectGroupPython] H_element020  label="H_element : 0.025"  # scripted group (container) (typed FeaturePython)
  n = 0.02468
FEATURE [App::DocumentObjectGroupPython] C_element021  label="C_element : 0.502"  # scripted group (container) (typed FeaturePython)
  n = 0.501611
FEATURE [App::DocumentObjectGroupPython] O_element019  label="O_element : 0.005"  # scripted group (container) (typed FeaturePython)
  n = 0.004527
FEATURE [App::DocumentObjectGroupPython] F_element004  label="F_element : 0.465"  # scripted group (container) (typed FeaturePython)
  n = 0.465209
FEATURE [App::DocumentObjectGroupPython] Si_element001  label="Si_element : 0.004"  # scripted group (container) (typed FeaturePython)
  n = 0.003973
FEATURE [App::DocumentObjectGroupPython] G4_C_552  label="G4_C-552"  # scripted group (container) (typed FeaturePython)
  Dunit = g/cm3
  Dvalue = 1.76
  Group = -> [H_element020,C_element021,O_element019,F_element004,Si_element001]
  conduct = 2
  density = 1
  expand = 3
  formula = G4_C-552
  name = G4_C-552
  specific = 4
FEATURE [App::DocumentObjectGroupPython] Cd_element001  label="Cd_element : 1"  # scripted group (container) (typed FeaturePython)
  n = 1
  ref = Cd_element
FEATURE [App::DocumentObjectGroupPython] Te_element001  label="Te_element : 1"  # scripted group (container) (typed FeaturePython)
  n = 1
  ref = Te_element
FEATURE [App::DocumentObjectGroupPython] G4_CADMIUM_TELLURIDE  # scripted group (container) (typed FeaturePython)
  Dunit = g/cm3
  Dvalue = 6.2
  Group = -> [Cd_element001,Te_element001]
  conduct = 2
  density = 1
  expand = 3
  formula = G4_CADMIUM_TELLURIDE
  name = G4_CADMIUM_TELLURIDE
  specific = 4
FEATURE [App::DocumentObjectGroupPython] Cd_element002  label="Cd_element : 002"  # scripted group (container) (typed FeaturePython)
  n = 1
  ref = Cd_element
FEATURE [App::DocumentObjectGroupPython] W_element001  label="W_element : 1"  # scripted group (container) (typed FeaturePython)
  n = 1
  ref = W_element
FEATURE [App::DocumentObjectGroupPython] O_element020  label="O_element : 008"  # scripted group (container) (typed FeaturePython)
  n = 4
  ref = O_element
FEATURE [App::DocumentObjectGroupPython] G4_CADMIUM_TUNGSTATE  # scripted group (container) (typed FeaturePython)
  Dunit = g/cm3
  Dvalue = 7.9
  Group = -> [Cd_element002,W_element001,O_element020]
  conduct = 2
  density = 1
  expand = 3
  formula = G4_CADMIUM_TUNGSTATE
  name = G4_CADMIUM_TUNGSTATE
  specific = 4
FEATURE [App::DocumentObjectGroupPython] Ca_element005  label="Ca_element : 1"  # scripted group (container) (typed FeaturePython)
  n = 1
  ref = Ca_element
FEATURE [App::DocumentObjectGroupPython] C_element022  label="C_element : 009"  # scripted group (container) (typed FeaturePython)
  n = 1
  ref = C_element
FEATURE [App::DocumentObjectGroupPython] O_element021  label="O_element : 009"  # scripted group (container) (typed FeaturePython)
  n = 3
  ref = O_element
FEATURE [App::DocumentObjectGroupPython] G4_CALCIUM_CARBONATE  # scripted group (container) (typed FeaturePython)
  Dunit = g/cm3
  Dvalue = 2.8
  Group = -> [Ca_element005,C_element022,O_element021]
  conduct = 2
  density = 1
  expand = 3
  formula = G4_CALCIUM_CARBONATE
  name = G4_CALCIUM_CARBONATE
  specific = 4
FEATURE [App::DocumentObjectGroupPython] Ca_element006  label="Ca_element : 002"  # scripted group (container) (typed FeaturePython)
  n = 1
  ref = Ca_element
FEATURE [App::DocumentObjectGroupPython] F_element005  label="F_element : 003"  # scripted group (container) (typed FeaturePython)
  n = 2
  ref = F_element
FEATURE [App::DocumentObjectGroupPython] G4_CALCIUM_FLUORIDE  # scripted group (container) (typed FeaturePython)
  Dunit = g/cm3
  Dvalue = 3.18
  Group = -> [Ca_element006,F_element005]
  conduct = 2
  density = 1
  expand = 3
  formula = G4_CALCIUM_FLUORIDE
  name = G4_CALCIUM_FLUORIDE
  specific = 4
FEATURE [App::DocumentObjectGroupPython] Ca_element007  label="Ca_element : 003"  # scripted group (container) (typed FeaturePython)
  n = 1
  ref = Ca_element
FEATURE [App::DocumentObjectGroupPython] O_element022  label="O_element : 010"  # scripted group (container) (typed FeaturePython)
  n = 1
  ref = O_element
FEATURE [App::DocumentObjectGroupPython] G4_CALCIUM_OXIDE  # scripted group (container) (typed FeaturePython)
  Dunit = g/cm3
  Dvalue = 3.3
  Group = -> [Ca_element007,O_element022]
  conduct = 2
  density = 1
  expand = 3
  formula = G4_CALCIUM_OXIDE
  name = G4_CALCIUM_OXIDE
  specific = 4
FEATURE [App::DocumentObjectGroupPython] Ca_element008  label="Ca_element : 004"  # scripted group (container) (typed FeaturePython)
  n = 1
  ref = Ca_element
FEATURE [App::DocumentObjectGroupPython] S_element007  label="S_element : 002"  # scripted group (container) (typed FeaturePython)
  n = 1
  ref = S_element
FEATURE [App::DocumentObjectGroupPython] O_element023  label="O_element : 011"  # scripted group (container) (typed FeaturePython)
  n = 4
  ref = O_element
FEATURE [App::DocumentObjectGroupPython] G4_CALCIUM_SULFATE  # scripted group (container) (typed FeaturePython)
  Dunit = g/cm3
  Dvalue = 2.96
  Group = -> [Ca_element008,S_element007,O_element023]
  conduct = 2
  density = 1
  expand = 3
  formula = G4_CALCIUM_SULFATE
  name = G4_CALCIUM_SULFATE
  specific = 4
FEATURE [App::DocumentObjectGroupPython] Ca_element009  label="Ca_element : 005"  # scripted group (container) (typed FeaturePython)
  n = 1
  ref = Ca_element
FEATURE [App::DocumentObjectGroupPython] W_element002  label="W_element : 002"  # scripted group (container) (typed FeaturePython)
  n = 1
  ref = W_element
FEATURE [App::DocumentObjectGroupPython] O_element024  label="O_element : 012"  # scripted group (container) (typed FeaturePython)
  n = 4
  ref = O_element
FEATURE [App::DocumentObjectGroupPython] G4_CALCIUM_TUNGSTATE  # scripted group (container) (typed FeaturePython)
  Dunit = g/cm3
  Dvalue = 6.062
  Group = -> [Ca_element009,W_element002,O_element024]
  conduct = 2
  density = 1
  expand = 3
  formula = G4_CALCIUM_TUNGSTATE
  name = G4_CALCIUM_TUNGSTATE
  specific = 4
FEATURE [App::DocumentObjectGroupPython] C_element023  label="C_element : 010"  # scripted group (container) (typed FeaturePython)
  n = 1
  ref = C_element
FEATURE [App::DocumentObjectGroupPython] O_element025  label="O_element : 013"  # scripted group (container) (typed FeaturePython)
  n = 2
  ref = O_element
FEATURE [App::DocumentObjectGroupPython] G4_CARBON_DIOXIDE  # scripted group (container) (typed FeaturePython)
  Dunit = g/cm3
  Dvalue = 0.00184212
  Group = -> [C_element023,O_element025]
  conduct = 2
  density = 1
  expand = 3
  formula = G4_CARBON_DIOXIDE
  name = G4_CARBON_DIOXIDE
  specific = 4
FEATURE [App::DocumentObjectGroupPython] C_element024  label="C_element : 011"  # scripted group (container) (typed FeaturePython)
  n = 1
  ref = C_element
FEATURE [App::DocumentObjectGroupPython] Cl_element004  label="Cl_element : 4"  # scripted group (container) (typed FeaturePython)
  n = 4
  ref = Cl_element
FEATURE [App::DocumentObjectGroupPython] G4_CARBON_TETRACHLORIDE  # scripted group (container) (typed FeaturePython)
  Dunit = g/cm3
  Dvalue = 1.594
  Group = -> [C_element024,Cl_element004]
  conduct = 2
  density = 1
  expand = 3
  formula = G4_CARBON_TETRACHLORIDE
  name = G4_CARBON_TETRACHLORIDE
  specific = 4
FEATURE [App::DocumentObjectGroupPython] C_element025  label="C_element : 012"  # scripted group (container) (typed FeaturePython)
  n = 6
  ref = C_element
FEATURE [App::DocumentObjectGroupPython] H_element021  label="H_element : 012"  # scripted group (container) (typed FeaturePython)
  n = 10
  ref = H_element
FEATURE [App::DocumentObjectGroupPython] O_element026  label="O_element : 5"  # scripted group (container) (typed FeaturePython)
  n = 5
  ref = O_element
FEATURE [App::DocumentObjectGroupPython] G4_CELLULOSE_CELLOPHANE  # scripted group (container) (typed FeaturePython)
  Dunit = g/cm3
  Dvalue = 1.42
  Group = -> [C_element025,H_element021,O_element026]
  conduct = 2
  density = 1
  expand = 3
  formula = G4_CELLULOSE_CELLOPHANE
  name = G4_CELLULOSE_CELLOPHANE
  specific = 4
FEATURE [App::DocumentObjectGroupPython] H_element022  label="H_element : 0.067"  # scripted group (container) (typed FeaturePython)
  n = 0.067125
FEATURE [App::DocumentObjectGroupPython] C_element026  label="C_element : 0.545"  # scripted group (container) (typed FeaturePython)
  n = 0.545403
FEATURE [App::DocumentObjectGroupPython] O_element027  label="O_element : 0.387"  # scripted group (container) (typed FeaturePython)
  n = 0.387472
FEATURE [App::DocumentObjectGroupPython] G4_CELLULOSE_BUTYRATE  # scripted group (container) (typed FeaturePython)
  Dunit = g/cm3
  Dvalue = 1.2
  Group = -> [H_element022,C_element026,O_element027]
  conduct = 2
  density = 1
  expand = 3
  formula = G4_CELLULOSE_BUTYRATE
  name = G4_CELLULOSE_BUTYRATE
  specific = 4
FEATURE [App::DocumentObjectGroupPython] H_element023  label="H_element : 0.029"  # scripted group (container) (typed FeaturePython)
  n = 0.029216
FEATURE [App::DocumentObjectGroupPython] C_element027  label="C_element : 0.271"  # scripted group (container) (typed FeaturePython)
  n = 0.271296
FEATURE [App::DocumentObjectGroupPython] N_element013  label="N_element : 0.121"  # scripted group (container) (typed FeaturePython)
  n = 0.121276
FEATURE [App::DocumentObjectGroupPython] O_element028  label="O_element : 0.578"  # scripted group (container) (typed FeaturePython)
  n = 0.578212
FEATURE [App::DocumentObjectGroupPython] G4_CELLULOSE_NITRATE  # scripted group (container) (typed FeaturePython)
  Dunit = g/cm3
  Dvalue = 1.49
  Group = -> [H_element023,C_element027,N_element013,O_element028]
  conduct = 2
  density = 1
  expand = 3
  formula = G4_CELLULOSE_NITRATE
  name = G4_CELLULOSE_NITRATE
  specific = 4
FEATURE [App::DocumentObjectGroupPython] H_element024  label="H_element : 0.108"  # scripted group (container) (typed FeaturePython)
  n = 0.107596
FEATURE [App::DocumentObjectGroupPython] N_element014  label="N_element : 0.001"  # scripted group (container) (typed FeaturePython)
  n = 0.0008
FEATURE [App::DocumentObjectGroupPython] O_element029  label="O_element : 0.875"  # scripted group (container) (typed FeaturePython)
  n = 0.874976
FEATURE [App::DocumentObjectGroupPython] S_element008  label="S_element : 0.015"  # scripted group (container) (typed FeaturePython)
  n = 0.014627
FEATURE [App::DocumentObjectGroupPython] Ce_element001  label="Ce_element : 0.002"  # scripted group (container) (typed FeaturePython)
  n = 0.002001
FEATURE [App::DocumentObjectGroupPython] G4_CERIC_SULFATE  # scripted group (container) (typed FeaturePython)
  Dunit = g/cm3
  Dvalue = 1.03
  Group = -> [H_element024,N_element014,O_element029,S_element008,Ce_element001]
  conduct = 2
  density = 1
  expand = 3
  formula = G4_CERIC_SULFATE
  name = G4_CERIC_SULFATE
  specific = 4
FEATURE [App::DocumentObjectGroupPython] Cs_element001  label="Cs_element : 1"  # scripted group (container) (typed FeaturePython)
  n = 1
  ref = Cs_element
FEATURE [App::DocumentObjectGroupPython] F_element006  label="F_element : 1"  # scripted group (container) (typed FeaturePython)
  n = 1
  ref = F_element
FEATURE [App::DocumentObjectGroupPython] G4_CESIUM_FLUORIDE  # scripted group (container) (typed FeaturePython)
  Dunit = g/cm3
  Dvalue = 4.115
  Group = -> [Cs_element001,F_element006]
  conduct = 2
  density = 1
  expand = 3
  formula = G4_CESIUM_FLUORIDE
  name = G4_CESIUM_FLUORIDE
  specific = 4
FEATURE [App::DocumentObjectGroupPython] Cs_element002  label="Cs_element : 002"  # scripted group (container) (typed FeaturePython)
  n = 1
  ref = Cs_element
FEATURE [App::DocumentObjectGroupPython] I_element001  label="I_element : 1"  # scripted group (container) (typed FeaturePython)
  n = 1
  ref = I_element
FEATURE [App::DocumentObjectGroupPython] G4_CESIUM_IODIDE  # scripted group (container) (typed FeaturePython)
  Dunit = g/cm3
  Dvalue = 4.51
  Group = -> [Cs_element002,I_element001]
  conduct = 2
  density = 1
  expand = 3
  formula = G4_CESIUM_IODIDE
  name = G4_CESIUM_IODIDE
  specific = 4
FEATURE [App::DocumentObjectGroupPython] C_element028  label="C_element : 013"  # scripted group (container) (typed FeaturePython)
  n = 6
  ref = C_element
FEATURE [App::DocumentObjectGroupPython] H_element025  label="H_element : 013"  # scripted group (container) (typed FeaturePython)
  n = 5
  ref = H_element
FEATURE [App::DocumentObjectGroupPython] Cl_element005  label="Cl_element : 1"  # scripted group (container) (typed FeaturePython)
  n = 1
  ref = Cl_element
FEATURE [App::DocumentObjectGroupPython] G4_CHLOROBENZENE  # scripted group (container) (typed FeaturePython)
  Dunit = g/cm3
  Dvalue = 1.1058
  Group = -> [C_element028,H_element025,Cl_element005]
  conduct = 2
  density = 1
  expand = 3
  formula = G4_CHLOROBENZENE
  name = G4_CHLOROBENZENE
  specific = 4
FEATURE [App::DocumentObjectGroupPython] C_element029  label="C_element : 014"  # scripted group (container) (typed FeaturePython)
  n = 1
  ref = C_element
FEATURE [App::DocumentObjectGroupPython] H_element026  label="H_element : 1"  # scripted group (container) (typed FeaturePython)
  n = 1
  ref = H_element
FEATURE [App::DocumentObjectGroupPython] Cl_element006  label="Cl_element : 3"  # scripted group (container) (typed FeaturePython)
  n = 3
  ref = Cl_element
FEATURE [App::DocumentObjectGroupPython] G4_CHLOROFORM  # scripted group (container) (typed FeaturePython)
  Dunit = g/cm3
  Dvalue = 1.4832
  Group = -> [C_element029,H_element026,Cl_element006]
  conduct = 2
  density = 1
  expand = 3
  formula = G4_CHLOROFORM
  name = G4_CHLOROFORM
  specific = 4
FEATURE [App::DocumentObjectGroupPython] H_element027  label="H_element : 0.010"  # scripted group (container) (typed FeaturePython)
  n = 0.01
FEATURE [App::DocumentObjectGroupPython] C_element030  label="C_element : 0.001"  # scripted group (container) (typed FeaturePython)
  n = 0.001
FEATURE [App::DocumentObjectGroupPython] O_element030  label="O_element : 0.529"  # scripted group (container) (typed FeaturePython)
  n = 0.529107
FEATURE [App::DocumentObjectGroupPython] Na_element005  label="Na_element : 0.016"  # scripted group (container) (typed FeaturePython)
  n = 0.016
FEATURE [App::DocumentObjectGroupPython] Mg_element003  label="Mg_element : 0.004"  # scripted group (container) (typed FeaturePython)
  n = 0.002
FEATURE [App::DocumentObjectGroupPython] Al_element002  label="Al_element : 0.034"  # scripted group (container) (typed FeaturePython)
  n = 0.033872
FEATURE [App::DocumentObjectGroupPython] Si_element002  label="Si_element : 0.337"  # scripted group (container) (typed FeaturePython)
  n = 0.337021
FEATURE [App::DocumentObjectGroupPython] K_element003  label="K_element : 0.013"  # scripted group (container) (typed FeaturePython)
  n = 0.013
FEATURE [App::DocumentObjectGroupPython] Ca_element010  label="Ca_element : 0.044"  # scripted group (container) (typed FeaturePython)
  n = 0.044
FEATURE [App::DocumentObjectGroupPython] Fe_element002  label="Fe_element : 0.014"  # scripted group (container) (typed FeaturePython)
  n = 0.014
FEATURE [App::DocumentObjectGroupPython] G4_CONCRETE  # scripted group (container) (typed FeaturePython)
  Dunit = g/cm3
  Dvalue = 2.3
  Group = -> [H_element027,C_element030,O_element030,Na_element005,Mg_element003,Al_element002,Si_element002,K_element003,Ca_element010,Fe_element002]
  conduct = 2
  density = 1
  expand = 3
  formula = G4_CONCRETE
  name = G4_CONCRETE
  specific = 4
FEATURE [App::DocumentObjectGroupPython] C_element031  label="C_element : 015"  # scripted group (container) (typed FeaturePython)
  n = 6
  ref = C_element
FEATURE [App::DocumentObjectGroupPython] H_element028  label="H_element : 12"  # scripted group (container) (typed FeaturePython)
  n = 12
  ref = H_element
FEATURE [App::DocumentObjectGroupPython] G4_CYCLOHEXANE  # scripted group (container) (typed FeaturePython)
  Dunit = g/cm3
  Dvalue = 0.779
  Group = -> [C_element031,H_element028]
  conduct = 2
  density = 1
  expand = 3
  formula = G4_CYCLOHEXANE
  name = G4_CYCLOHEXANE
  specific = 4
FEATURE [App::DocumentObjectGroupPython] C_element032  label="C_element : 016"  # scripted group (container) (typed FeaturePython)
  n = 6
  ref = C_element
FEATURE [App::DocumentObjectGroupPython] H_element029  label="H_element : 4"  # scripted group (container) (typed FeaturePython)
  n = 4
  ref = H_element
FEATURE [App::DocumentObjectGroupPython] Cl_element007  label="Cl_element : 2"  # scripted group (container) (typed FeaturePython)
  n = 2
  ref = Cl_element
FEATURE [App::DocumentObjectGroupPython] G4_1_2_DICHLOROBENZENE  label="G4_1.2-DICHLOROBENZENE"  # scripted group (container) (typed FeaturePython)
  Dunit = g/cm3
  Dvalue = 1.3048
  Group = -> [C_element032,H_element029,Cl_element007]
  conduct = 2
  density = 1
  expand = 3
  formula = G4_1.2-DICHLOROBENZENE
  name = G4_1.2-DICHLOROBENZENE
  specific = 4
FEATURE [App::DocumentObjectGroupPython] C_element033  label="C_element : 017"  # scripted group (container) (typed FeaturePython)
  n = 4
  ref = C_element
FEATURE [App::DocumentObjectGroupPython] H_element030  label="H_element : 8"  # scripted group (container) (typed FeaturePython)
  n = 8
  ref = H_element
FEATURE [App::DocumentObjectGroupPython] O_element031  label="O_element : 014"  # scripted group (container) (typed FeaturePython)
  n = 1
  ref = O_element
FEATURE [App::DocumentObjectGroupPython] Cl_element008  label="Cl_element : 005"  # scripted group (container) (typed FeaturePython)
  n = 2
  ref = Cl_element
FEATURE [App::DocumentObjectGroupPython] G4_DICHLORODIETHYL_ETHER  # scripted group (container) (typed FeaturePython)
  Dunit = g/cm3
  Dvalue = 1.2199
  Group = -> [C_element033,H_element030,O_element031,Cl_element008]
  conduct = 2
  density = 1
  expand = 3
  formula = G4_DICHLORODIETHYL_ETHER
  name = G4_DICHLORODIETHYL_ETHER
  specific = 4
FEATURE [App::DocumentObjectGroupPython] C_element034  label="C_element : 018"  # scripted group (container) (typed FeaturePython)
  n = 2
  ref = C_element
FEATURE [App::DocumentObjectGroupPython] H_element031  label="H_element : 014"  # scripted group (container) (typed FeaturePython)
  n = 4
  ref = H_element
FEATURE [App::DocumentObjectGroupPython] Cl_element009  label="Cl_element : 006"  # scripted group (container) (typed FeaturePython)
  n = 2
  ref = Cl_element
FEATURE [App::DocumentObjectGroupPython] G4_1_2_DICHLOROETHANE  label="G4_1.2-DICHLOROETHANE"  # scripted group (container) (typed FeaturePython)
  Dunit = g/cm3
  Dvalue = 1.2351
  Group = -> [C_element034,H_element031,Cl_element009]
  conduct = 2
  density = 1
  expand = 3
  formula = G4_1.2-DICHLOROETHANE
  name = G4_1.2-DICHLOROETHANE
  specific = 4
FEATURE [App::DocumentObjectGroupPython] C_element035  label="C_element : 019"  # scripted group (container) (typed FeaturePython)
  n = 4
  ref = C_element
FEATURE [App::DocumentObjectGroupPython] H_element032  label="H_element : 015"  # scripted group (container) (typed FeaturePython)
  n = 10
  ref = H_element
FEATURE [App::DocumentObjectGroupPython] O_element032  label="O_element : 015"  # scripted group (container) (typed FeaturePython)
  n = 1
  ref = O_element
FEATURE [App::DocumentObjectGroupPython] G4_DIETHYL_ETHER  # scripted group (container) (typed FeaturePython)
  Dunit = g/cm3
  Dvalue = 0.71378
  Group = -> [C_element035,H_element032,O_element032]
  conduct = 2
  density = 1
  expand = 3
  formula = G4_DIETHYL_ETHER
  name = G4_DIETHYL_ETHER
  specific = 4
FEATURE [App::DocumentObjectGroupPython] C_element036  label="C_element : 020"  # scripted group (container) (typed FeaturePython)
  n = 3
  ref = C_element
FEATURE [App::DocumentObjectGroupPython] H_element033  label="H_element : 016"  # scripted group (container) (typed FeaturePython)
  n = 7
  ref = H_element
FEATURE [App::DocumentObjectGroupPython] N_element015  label="N_element : 008"  # scripted group (container) (typed FeaturePython)
  n = 1
  ref = N_element
FEATURE [App::DocumentObjectGroupPython] O_element033  label="O_element : 016"  # scripted group (container) (typed FeaturePython)
  n = 1
  ref = O_element
FEATURE [App::DocumentObjectGroupPython] G4_N_N_DIMETHYL_FORMAMIDE  label="G4_N.N-DIMETHYL_FORMAMIDE"  # scripted group (container) (typed FeaturePython)
  Dunit = g/cm3
  Dvalue = 0.9487
  Group = -> [C_element036,H_element033,N_element015,O_element033]
  conduct = 2
  density = 1
  expand = 3
  formula = G4_N.N-DIMETHYL_FORMAMIDE
  name = G4_N.N-DIMETHYL_FORMAMIDE
  specific = 4
FEATURE [App::DocumentObjectGroupPython] C_element037  label="C_element : 021"  # scripted group (container) (typed FeaturePython)
  n = 2
  ref = C_element
FEATURE [App::DocumentObjectGroupPython] H_element034  label="H_element : 017"  # scripted group (container) (typed FeaturePython)
  n = 6
  ref = H_element
FEATURE [App::DocumentObjectGroupPython] O_element034  label="O_element : 017"  # scripted group (container) (typed FeaturePython)
  n = 1
  ref = O_element
FEATURE [App::DocumentObjectGroupPython] S_element009  label="S_element : 003"  # scripted group (container) (typed FeaturePython)
  n = 1
  ref = S_element
FEATURE [App::DocumentObjectGroupPython] G4_DIMETHYL_SULFOXIDE  # scripted group (container) (typed FeaturePython)
  Dunit = g/cm3
  Dvalue = 1.1014
  Group = -> [C_element037,H_element034,O_element034,S_element009]
  conduct = 2
  density = 1
  expand = 3
  formula = G4_DIMETHYL_SULFOXIDE
  name = G4_DIMETHYL_SULFOXIDE
  specific = 4
FEATURE [App::DocumentObjectGroupPython] C_element038  label="C_element : 022"  # scripted group (container) (typed FeaturePython)
  n = 2
  ref = C_element
FEATURE [App::DocumentObjectGroupPython] H_element035  label="H_element : 018"  # scripted group (container) (typed FeaturePython)
  n = 6
  ref = H_element
FEATURE [App::DocumentObjectGroupPython] G4_ETHANE  # scripted group (container) (typed FeaturePython)
  Dunit = g/cm3
  Dvalue = 0.00125324
  Group = -> [C_element038,H_element035]
  conduct = 2
  density = 1
  expand = 3
  formula = G4_ETHANE
  name = G4_ETHANE
  specific = 4
FEATURE [App::DocumentObjectGroupPython] C_element039  label="C_element : 023"  # scripted group (container) (typed FeaturePython)
  n = 2
  ref = C_element
FEATURE [App::DocumentObjectGroupPython] H_element036  label="H_element : 019"  # scripted group (container) (typed FeaturePython)
  n = 6
  ref = H_element
FEATURE [App::DocumentObjectGroupPython] O_element035  label="O_element : 018"  # scripted group (container) (typed FeaturePython)
  n = 1
  ref = O_element
FEATURE [App::DocumentObjectGroupPython] G4_ETHYL_ALCOHOL  # scripted group (container) (typed FeaturePython)
  Dunit = g/cm3
  Dvalue = 0.7893
  Group = -> [C_element039,H_element036,O_element035]
  conduct = 2
  density = 1
  expand = 3
  formula = G4_ETHYL_ALCOHOL
  name = G4_ETHYL_ALCOHOL
  specific = 4
FEATURE [App::DocumentObjectGroupPython] H_element037  label="H_element : 0.090"  # scripted group (container) (typed FeaturePython)
  n = 0.090027
FEATURE [App::DocumentObjectGroupPython] C_element040  label="C_element : 0.585"  # scripted group (container) (typed FeaturePython)
  n = 0.585182
FEATURE [App::DocumentObjectGroupPython] O_element036  label="O_element : 0.325"  # scripted group (container) (typed FeaturePython)
  n = 0.324791
FEATURE [App::DocumentObjectGroupPython] G4_ETHYL_CELLULOSE  # scripted group (container) (typed FeaturePython)
  Dunit = g/cm3
  Dvalue = 1.13
  Group = -> [H_element037,C_element040,O_element036]
  conduct = 2
  density = 1
  expand = 3
  formula = G4_ETHYL_CELLULOSE
  name = G4_ETHYL_CELLULOSE
  specific = 4
FEATURE [App::DocumentObjectGroupPython] C_element041  label="C_element : 024"  # scripted group (container) (typed FeaturePython)
  n = 2
  ref = C_element
FEATURE [App::DocumentObjectGroupPython] H_element038  label="H_element : 020"  # scripted group (container) (typed FeaturePython)
  n = 4
  ref = H_element
FEATURE [App::DocumentObjectGroupPython] G4_ETHYLENE  # scripted group (container) (typed FeaturePython)
  Dunit = g/cm3
  Dvalue = 0.00117497
  Group = -> [C_element041,H_element038]
  conduct = 2
  density = 1
  expand = 3
  formula = G4_ETHYLENE
  name = G4_ETHYLENE
  specific = 4
FEATURE [App::DocumentObjectGroupPython] H_element039  label="H_element : 0.096"  # scripted group (container) (typed FeaturePython)
  n = 0.096
FEATURE [App::DocumentObjectGroupPython] C_element042  label="C_element : 0.195"  # scripted group (container) (typed FeaturePython)
  n = 0.195
FEATURE [App::DocumentObjectGroupPython] N_element016  label="N_element : 0.057"  # scripted group (container) (typed FeaturePython)
  n = 0.057
FEATURE [App::DocumentObjectGroupPython] O_element037  label="O_element : 0.646"  # scripted group (container) (typed FeaturePython)
  n = 0.646
FEATURE [App::DocumentObjectGroupPython] Na_element006  label="Na_element : 0.017"  # scripted group (container) (typed FeaturePython)
  n = 0.001
FEATURE [App::DocumentObjectGroupPython] P_element005  label="P_element : 0.104"  # scripted group (container) (typed FeaturePython)
  n = 0.001
FEATURE [App::DocumentObjectGroupPython] S_element010  label="S_element : 0.016"  # scripted group (container) (typed FeaturePython)
  n = 0.003
FEATURE [App::DocumentObjectGroupPython] Cl_element010  label="Cl_element : 0.005"  # scripted group (container) (typed FeaturePython)
  n = 0.001
FEATURE [App::DocumentObjectGroupPython] G4_EYE_LENS_ICRP  # scripted group (container) (typed FeaturePython)
  Dunit = g/cm3
  Dvalue = 1.07
  Group = -> [H_element039,C_element042,N_element016,O_element037,Na_element006,P_element005,S_element010,Cl_element010]
  conduct = 2
  density = 1
  expand = 3
  formula = G4_EYE_LENS_ICRP
  name = G4_EYE_LENS_ICRP
  specific = 4
FEATURE [App::DocumentObjectGroupPython] Fe_element003  label="Fe_element : 2"  # scripted group (container) (typed FeaturePython)
  n = 2
  ref = Fe_element
FEATURE [App::DocumentObjectGroupPython] O_element038  label="O_element : 019"  # scripted group (container) (typed FeaturePython)
  n = 3
  ref = O_element
FEATURE [App::DocumentObjectGroupPython] G4_FERRIC_OXIDE  # scripted group (container) (typed FeaturePython)
  Dunit = g/cm3
  Dvalue = 5.2
  Group = -> [Fe_element003,O_element038]
  conduct = 2
  density = 1
  expand = 3
  formula = G4_FERRIC_OXIDE
  name = G4_FERRIC_OXIDE
  specific = 4
FEATURE [App::DocumentObjectGroupPython] Fe_element004  label="Fe_element : 1"  # scripted group (container) (typed FeaturePython)
  n = 1
  ref = Fe_element
FEATURE [App::DocumentObjectGroupPython] B_element003  label="B_element : 1"  # scripted group (container) (typed FeaturePython)
  n = 1
  ref = B_element
FEATURE [App::DocumentObjectGroupPython] G4_FERROBORIDE  # scripted group (container) (typed FeaturePython)
  Dunit = g/cm3
  Dvalue = 7.15
  Group = -> [Fe_element004,B_element003]
  conduct = 2
  density = 1
  expand = 3
  formula = G4_FERROBORIDE
  name = G4_FERROBORIDE
  specific = 4
FEATURE [App::DocumentObjectGroupPython] Fe_element005  label="Fe_element : 003"  # scripted group (container) (typed FeaturePython)
  n = 1
  ref = Fe_element
FEATURE [App::DocumentObjectGroupPython] O_element039  label="O_element : 020"  # scripted group (container) (typed FeaturePython)
  n = 1
  ref = O_element
FEATURE [App::DocumentObjectGroupPython] G4_FERROUS_OXIDE  # scripted group (container) (typed FeaturePython)
  Dunit = g/cm3
  Dvalue = 5.7
  Group = -> [Fe_element005,O_element039]
  conduct = 2
  density = 1
  expand = 3
  formula = G4_FERROUS_OXIDE
  name = G4_FERROUS_OXIDE
  specific = 4
FEATURE [App::DocumentObjectGroupPython] H_element040  label="H_element : 0.115"  # scripted group (container) (typed FeaturePython)
  n = 0.108259
FEATURE [App::DocumentObjectGroupPython] N_element017  label="N_element : 0.000"  # scripted group (container) (typed FeaturePython)
  n = 2.7e-05
FEATURE [App::DocumentObjectGroupPython] O_element040  label="O_element : 0.879"  # scripted group (container) (typed FeaturePython)
  n = 0.878636
FEATURE [App::DocumentObjectGroupPython] Na_element007  label="Na_element : 0.000"  # scripted group (container) (typed FeaturePython)
  n = 2.2e-05
FEATURE [App::DocumentObjectGroupPython] S_element011  label="S_element : 0.013"  # scripted group (container) (typed FeaturePython)
  n = 0.012968
FEATURE [App::DocumentObjectGroupPython] Cl_element011  label="Cl_element : 0.000"  # scripted group (container) (typed FeaturePython)
  n = 3.4e-05
FEATURE [App::DocumentObjectGroupPython] Fe_element006  label="Fe_element : 0.000"  # scripted group (container) (typed FeaturePython)
  n = 5.4e-05
FEATURE [App::DocumentObjectGroupPython] G4_FERROUS_SULFATE  # scripted group (container) (typed FeaturePython)
  Dunit = g/cm3
  Dvalue = 1.024
  Group = -> [H_element040,N_element017,O_element040,Na_element007,S_element011,Cl_element011,Fe_element006]
  conduct = 2
  density = 1
  expand = 3
  formula = G4_FERROUS_SULFATE
  name = G4_FERROUS_SULFATE
  specific = 4
FEATURE [App::DocumentObjectGroupPython] C_element043  label="C_element : 0.099"  # scripted group (container) (typed FeaturePython)
  n = 0.099335
FEATURE [App::DocumentObjectGroupPython] F_element007  label="F_element : 0.314"  # scripted group (container) (typed FeaturePython)
  n = 0.314247
FEATURE [App::DocumentObjectGroupPython] Cl_element012  label="Cl_element : 0.586"  # scripted group (container) (typed FeaturePython)
  n = 0.586418
FEATURE [App::DocumentObjectGroupPython] G4_FREON_12  label="G4_FREON-12"  # scripted group (container) (typed FeaturePython)
  Dunit = g/cm3
  Dvalue = 1.12
  Group = -> [C_element043,F_element007,Cl_element012]
  conduct = 2
  density = 1
  expand = 3
  formula = G4_FREON-12
  name = G4_FREON-12
  specific = 4
FEATURE [App::DocumentObjectGroupPython] C_element044  label="C_element : 0.057"  # scripted group (container) (typed FeaturePython)
  n = 0.057245
FEATURE [App::DocumentObjectGroupPython] F_element008  label="F_element : 0.181"  # scripted group (container) (typed FeaturePython)
  n = 0.181096
FEATURE [App::DocumentObjectGroupPython] Br_element001  label="Br_element : 0.762"  # scripted group (container) (typed FeaturePython)
  n = 0.761659
FEATURE [App::DocumentObjectGroupPython] G4_FREON_12B2  label="G4_FREON-12B2"  # scripted group (container) (typed FeaturePython)
  Dunit = g/cm3
  Dvalue = 1.8
  Group = -> [C_element044,F_element008,Br_element001]
  conduct = 2
  density = 1
  expand = 3
  formula = G4_FREON-12B2
  name = G4_FREON-12B2
  specific = 4
FEATURE [App::DocumentObjectGroupPython] C_element045  label="C_element : 0.115"  # scripted group (container) (typed FeaturePython)
  n = 0.114983
FEATURE [App::DocumentObjectGroupPython] F_element009  label="F_element : 0.546"  # scripted group (container) (typed FeaturePython)
  n = 0.545621
FEATURE [App::DocumentObjectGroupPython] Cl_element013  label="Cl_element : 0.339"  # scripted group (container) (typed FeaturePython)
  n = 0.339396
FEATURE [App::DocumentObjectGroupPython] G4_FREON_13  label="G4_FREON-13"  # scripted group (container) (typed FeaturePython)
  Dunit = g/cm3
  Dvalue = 0.95
  Group = -> [C_element045,F_element009,Cl_element013]
  conduct = 2
  density = 1
  expand = 3
  formula = G4_FREON-13
  name = G4_FREON-13
  specific = 4
FEATURE [App::DocumentObjectGroupPython] C_element046  label="C_element : 025"  # scripted group (container) (typed FeaturePython)
  n = 1
  ref = C_element
FEATURE [App::DocumentObjectGroupPython] F_element010  label="F_element : 3"  # scripted group (container) (typed FeaturePython)
  n = 3
  ref = F_element
FEATURE [App::DocumentObjectGroupPython] Br_element002  label="Br_element : 1"  # scripted group (container) (typed FeaturePython)
  n = 1
  ref = Br_element
FEATURE [App::DocumentObjectGroupPython] G4_FREON_13B1  label="G4_FREON-13B1"  # scripted group (container) (typed FeaturePython)
  Dunit = g/cm3
  Dvalue = 1.5
  Group = -> [C_element046,F_element010,Br_element002]
  conduct = 2
  density = 1
  expand = 3
  formula = G4_FREON-13B1
  name = G4_FREON-13B1
  specific = 4
FEATURE [App::DocumentObjectGroupPython] C_element047  label="C_element : 0.061"  # scripted group (container) (typed FeaturePython)
  n = 0.061309
FEATURE [App::DocumentObjectGroupPython] F_element011  label="F_element : 0.291"  # scripted group (container) (typed FeaturePython)
  n = 0.290924
FEATURE [App::DocumentObjectGroupPython] I_element002  label="I_element : 0.648"  # scripted group (container) (typed FeaturePython)
  n = 0.647767
FEATURE [App::DocumentObjectGroupPython] G4_FREON_13I1  label="G4_FREON-13I1"  # scripted group (container) (typed FeaturePython)
  Dunit = g/cm3
  Dvalue = 1.8
  Group = -> [C_element047,F_element011,I_element002]
  conduct = 2
  density = 1
  expand = 3
  formula = G4_FREON-13I1
  name = G4_FREON-13I1
  specific = 4
FEATURE [App::DocumentObjectGroupPython] Gd_element001  label="Gd_element : 2"  # scripted group (container) (typed FeaturePython)
  n = 2
  ref = Gd_element
FEATURE [App::DocumentObjectGroupPython] O_element041  label="O_element : 021"  # scripted group (container) (typed FeaturePython)
  n = 2
  ref = O_element
FEATURE [App::DocumentObjectGroupPython] S_element012  label="S_element : 004"  # scripted group (container) (typed FeaturePython)
  n = 1
  ref = S_element
FEATURE [App::DocumentObjectGroupPython] G4_GADOLINIUM_OXYSULFIDE  # scripted group (container) (typed FeaturePython)
  Dunit = g/cm3
  Dvalue = 7.44
  Group = -> [Gd_element001,O_element041,S_element012]
  conduct = 2
  density = 1
  expand = 3
  formula = G4_GADOLINIUM_OXYSULFIDE
  name = G4_GADOLINIUM_OXYSULFIDE
  specific = 4
FEATURE [App::DocumentObjectGroupPython] Ga_element001  label="Ga_element : 1"  # scripted group (container) (typed FeaturePython)
  n = 1
  ref = Ga_element
FEATURE [App::DocumentObjectGroupPython] As_element001  label="As_element : 1"  # scripted group (container) (typed FeaturePython)
  n = 1
  ref = As_element
FEATURE [App::DocumentObjectGroupPython] G4_GALLIUM_ARSENIDE  # scripted group (container) (typed FeaturePython)
  Dunit = g/cm3
  Dvalue = 5.31
  Group = -> [Ga_element001,As_element001]
  conduct = 2
  density = 1
  expand = 3
  formula = G4_GALLIUM_ARSENIDE
  name = G4_GALLIUM_ARSENIDE
  specific = 4
FEATURE [App::DocumentObjectGroupPython] H_element041  label="H_element : 0.081"  # scripted group (container) (typed FeaturePython)
  n = 0.08118
FEATURE [App::DocumentObjectGroupPython] C_element048  label="C_element : 0.416"  # scripted group (container) (typed FeaturePython)
  n = 0.41606
FEATURE [App::DocumentObjectGroupPython] N_element018  label="N_element : 0.111"  # scripted group (container) (typed FeaturePython)
  n = 0.11124
FEATURE [App::DocumentObjectGroupPython] O_element042  label="O_element : 0.381"  # scripted group (container) (typed FeaturePython)
  n = 0.38064
FEATURE [App::DocumentObjectGroupPython] S_element013  label="S_element : 0.011"  # scripted group (container) (typed FeaturePython)
  n = 0.01088
FEATURE [App::DocumentObjectGroupPython] G4_GEL_PHOTO_EMULSION  # scripted group (container) (typed FeaturePython)
  Dunit = g/cm3
  Dvalue = 1.2914
  Group = -> [H_element041,C_element048,N_element018,O_element042,S_element013]
  conduct = 2
  density = 1
  expand = 3
  formula = G4_GEL_PHOTO_EMULSION
  name = G4_GEL_PHOTO_EMULSION
  specific = 4
FEATURE [App::DocumentObjectGroupPython] B_element004  label="B_element : 0.040"  # scripted group (container) (typed FeaturePython)
  n = 0.0400639
FEATURE [App::DocumentObjectGroupPython] O_element043  label="O_element : 0.540"  # scripted group (container) (typed FeaturePython)
  n = 0.539561
FEATURE [App::DocumentObjectGroupPython] Na_element008  label="Na_element : 0.028"  # scripted group (container) (typed FeaturePython)
  n = 0.0281909
FEATURE [App::DocumentObjectGroupPython] Al_element003  label="Al_element : 0.012"  # scripted group (container) (typed FeaturePython)
  n = 0.011644
FEATURE [App::DocumentObjectGroupPython] Si_element003  label="Si_element : 0.377"  # scripted group (container) (typed FeaturePython)
  n = 0.377219
FEATURE [App::DocumentObjectGroupPython] K_element004  label="K_element : 0.014"  # scripted group (container) (typed FeaturePython)
  n = 0.00332099
FEATURE [App::DocumentObjectGroupPython] G4_Pyrex_Glass  # scripted group (container) (typed FeaturePython)
  Dunit = g/cm3
  Dvalue = 2.23
  Group = -> [B_element004,O_element043,Na_element008,Al_element003,Si_element003,K_element004]
  conduct = 2
  density = 1
  expand = 3
  formula = G4_Pyrex_Glass
  name = G4_Pyrex_Glass
  specific = 4
FEATURE [App::DocumentObjectGroupPython] O_element044  label="O_element : 0.156"  # scripted group (container) (typed FeaturePython)
  n = 0.156453
FEATURE [App::DocumentObjectGroupPython] Si_element004  label="Si_element : 0.081"  # scripted group (container) (typed FeaturePython)
  n = 0.080866
FEATURE [App::DocumentObjectGroupPython] Ti_element001  label="Ti_element : 0.008"  # scripted group (container) (typed FeaturePython)
  n = 0.008092
FEATURE [App::DocumentObjectGroupPython] As_element002  label="As_element : 0.003"  # scripted group (container) (typed FeaturePython)
  n = 0.002651
FEATURE [App::DocumentObjectGroupPython] Pb_element001  label="Pb_element : 0.752"  # scripted group (container) (typed FeaturePython)
  n = 0.751938
FEATURE [App::DocumentObjectGroupPython] G4_GLASS_LEAD  # scripted group (container) (typed FeaturePython)
  Dunit = g/cm3
  Dvalue = 6.22
  Group = -> [O_element044,Si_element004,Ti_element001,As_element002,Pb_element001]
  conduct = 2
  density = 1
  expand = 3
  formula = G4_GLASS_LEAD
  name = G4_GLASS_LEAD
  specific = 4
FEATURE [App::DocumentObjectGroupPython] O_element045  label="O_element : 0.460"  # scripted group (container) (typed FeaturePython)
  n = 0.4598
FEATURE [App::DocumentObjectGroupPython] Na_element009  label="Na_element : 0.096"  # scripted group (container) (typed FeaturePython)
  n = 0.0964411
FEATURE [App::DocumentObjectGroupPython] Si_element005  label="Si_element : 0.378"  # scripted group (container) (typed FeaturePython)
  n = 0.336553
FEATURE [App::DocumentObjectGroupPython] Ca_element011  label="Ca_element : 0.107"  # scripted group (container) (typed FeaturePython)
  n = 0.107205
FEATURE [App::DocumentObjectGroupPython] G4_GLASS_PLATE  # scripted group (container) (typed FeaturePython)
  Dunit = g/cm3
  Dvalue = 2.4
  Group = -> [O_element045,Na_element009,Si_element005,Ca_element011]
  conduct = 2
  density = 1
  expand = 3
  formula = G4_GLASS_PLATE
  name = G4_GLASS_PLATE
  specific = 4
FEATURE [App::DocumentObjectGroupPython] C_element049  label="C_element : 026"  # scripted group (container) (typed FeaturePython)
  n = 5
  ref = C_element
FEATURE [App::DocumentObjectGroupPython] H_element042  label="H_element : 021"  # scripted group (container) (typed FeaturePython)
  n = 10
  ref = H_element
FEATURE [App::DocumentObjectGroupPython] N_element019  label="N_element : 2"  # scripted group (container) (typed FeaturePython)
  n = 2
  ref = N_element
FEATURE [App::DocumentObjectGroupPython] O_element046  label="O_element : 022"  # scripted group (container) (typed FeaturePython)
  n = 3
  ref = O_element
FEATURE [App::DocumentObjectGroupPython] G4_GLUTAMINE  # scripted group (container) (typed FeaturePython)
  Dunit = g/cm3
  Dvalue = 1.46
  Group = -> [C_element049,H_element042,N_element019,O_element046]
  conduct = 2
  density = 1
  expand = 3
  formula = G4_GLUTAMINE
  name = G4_GLUTAMINE
  specific = 4
FEATURE [App::DocumentObjectGroupPython] C_element050  label="C_element : 027"  # scripted group (container) (typed FeaturePython)
  n = 3
  ref = C_element
FEATURE [App::DocumentObjectGroupPython] H_element043  label="H_element : 022"  # scripted group (container) (typed FeaturePython)
  n = 8
  ref = H_element
FEATURE [App::DocumentObjectGroupPython] O_element047  label="O_element : 023"  # scripted group (container) (typed FeaturePython)
  n = 3
  ref = O_element
FEATURE [App::DocumentObjectGroupPython] G4_GLYCEROL  # scripted group (container) (typed FeaturePython)
  Dunit = g/cm3
  Dvalue = 1.2613
  Group = -> [C_element050,H_element043,O_element047]
  conduct = 2
  density = 1
  expand = 3
  formula = G4_GLYCEROL
  name = G4_GLYCEROL
  specific = 4
FEATURE [App::DocumentObjectGroupPython] C_element051  label="C_element : 028"  # scripted group (container) (typed FeaturePython)
  n = 5
  ref = C_element
FEATURE [App::DocumentObjectGroupPython] H_element044  label="H_element : 023"  # scripted group (container) (typed FeaturePython)
  n = 5
  ref = H_element
FEATURE [App::DocumentObjectGroupPython] N_element020  label="N_element : 009"  # scripted group (container) (typed FeaturePython)
  n = 5
  ref = N_element
FEATURE [App::DocumentObjectGroupPython] O_element048  label="O_element : 024"  # scripted group (container) (typed FeaturePython)
  n = 1
  ref = O_element
FEATURE [App::DocumentObjectGroupPython] G4_GUANINE  # scripted group (container) (typed FeaturePython)
  Dunit = g/cm3
  Dvalue = 2.2
  Group = -> [C_element051,H_element044,N_element020,O_element048]
  conduct = 2
  density = 1
  expand = 3
  formula = G4_GUANINE
  name = G4_GUANINE
  specific = 4
FEATURE [App::DocumentObjectGroupPython] Ca_element012  label="Ca_element : 006"  # scripted group (container) (typed FeaturePython)
  n = 1
  ref = Ca_element
FEATURE [App::DocumentObjectGroupPython] S_element014  label="S_element : 005"  # scripted group (container) (typed FeaturePython)
  n = 1
  ref = S_element
FEATURE [App::DocumentObjectGroupPython] O_element049  label="O_element : 6"  # scripted group (container) (typed FeaturePython)
  n = 6
  ref = O_element
FEATURE [App::DocumentObjectGroupPython] H_element045  label="H_element : 024"  # scripted group (container) (typed FeaturePython)
  n = 4
  ref = H_element
FEATURE [App::DocumentObjectGroupPython] G4_GYPSUM  # scripted group (container) (typed FeaturePython)
  Dunit = g/cm3
  Dvalue = 2.32
  Group = -> [Ca_element012,S_element014,O_element049,H_element045]
  conduct = 2
  density = 1
  expand = 3
  formula = G4_GYPSUM
  name = G4_GYPSUM
  specific = 4
FEATURE [App::DocumentObjectGroupPython] C_element052  label="C_element : 7"  # scripted group (container) (typed FeaturePython)
  n = 7
  ref = C_element
FEATURE [App::DocumentObjectGroupPython] H_element046  label="H_element : 16"  # scripted group (container) (typed FeaturePython)
  n = 16
  ref = H_element
FEATURE [App::DocumentObjectGroupPython] G4_N_HEPTANE  label="G4_N-HEPTANE"  # scripted group (container) (typed FeaturePython)
  Dunit = g/cm3
  Dvalue = 0.68376
  Group = -> [C_element052,H_element046]
  conduct = 2
  density = 1
  expand = 3
  formula = G4_N-HEPTANE
  name = G4_N-HEPTANE
  specific = 4
FEATURE [App::DocumentObjectGroupPython] C_element053  label="C_element : 029"  # scripted group (container) (typed FeaturePython)
  n = 6
  ref = C_element
FEATURE [App::DocumentObjectGroupPython] H_element047  label="H_element : 14"  # scripted group (container) (typed FeaturePython)
  n = 14
  ref = H_element
FEATURE [App::DocumentObjectGroupPython] G4_N_HEXANE  label="G4_N-HEXANE"  # scripted group (container) (typed FeaturePython)
  Dunit = g/cm3
  Dvalue = 0.6603
  Group = -> [C_element053,H_element047]
  conduct = 2
  density = 1
  expand = 3
  formula = G4_N-HEXANE
  name = G4_N-HEXANE
  specific = 4
FEATURE [App::DocumentObjectGroupPython] C_element054  label="C_element : 22"  # scripted group (container) (typed FeaturePython)
  n = 22
  ref = C_element
FEATURE [App::DocumentObjectGroupPython] H_element048  label="H_element : 025"  # scripted group (container) (typed FeaturePython)
  n = 10
  ref = H_element
FEATURE [App::DocumentObjectGroupPython] N_element021  label="N_element : 010"  # scripted group (container) (typed FeaturePython)
  n = 2
  ref = N_element
FEATURE [App::DocumentObjectGroupPython] O_element050  label="O_element : 025"  # scripted group (container) (typed FeaturePython)
  n = 5
  ref = O_element
FEATURE [App::DocumentObjectGroupPython] G4_KAPTON  # scripted group (container) (typed FeaturePython)
  Dunit = g/cm3
  Dvalue = 1.42
  Group = -> [C_element054,H_element048,N_element021,O_element050]
  conduct = 2
  density = 1
  expand = 3
  formula = G4_KAPTON
  name = G4_KAPTON
  specific = 4
FEATURE [App::DocumentObjectGroupPython] La_element001  label="La_element : 1"  # scripted group (container) (typed FeaturePython)
  n = 1
  ref = La_element
FEATURE [App::DocumentObjectGroupPython] Br_element003  label="Br_element : 002"  # scripted group (container) (typed FeaturePython)
  n = 1
  ref = Br_element
FEATURE [App::DocumentObjectGroupPython] O_element051  label="O_element : 026"  # scripted group (container) (typed FeaturePython)
  n = 1
  ref = O_element
FEATURE [App::DocumentObjectGroupPython] G4_LANTHANUM_OXYBROMIDE  # scripted group (container) (typed FeaturePython)
  Dunit = g/cm3
  Dvalue = 6.28
  Group = -> [La_element001,Br_element003,O_element051]
  conduct = 2
  density = 1
  expand = 3
  formula = G4_LANTHANUM_OXYBROMIDE
  name = G4_LANTHANUM_OXYBROMIDE
  specific = 4
FEATURE [App::DocumentObjectGroupPython] La_element002  label="La_element : 2"  # scripted group (container) (typed FeaturePython)
  n = 2
  ref = La_element
FEATURE [App::DocumentObjectGroupPython] O_element052  label="O_element : 027"  # scripted group (container) (typed FeaturePython)
  n = 2
  ref = O_element
FEATURE [App::DocumentObjectGroupPython] S_element015  label="S_element : 006"  # scripted group (container) (typed FeaturePython)
  n = 1
  ref = S_element
FEATURE [App::DocumentObjectGroupPython] G4_LANTHANUM_OXYSULFIDE  # scripted group (container) (typed FeaturePython)
  Dunit = g/cm3
  Dvalue = 5.86
  Group = -> [La_element002,O_element052,S_element015]
  conduct = 2
  density = 1
  expand = 3
  formula = G4_LANTHANUM_OXYSULFIDE
  name = G4_LANTHANUM_OXYSULFIDE
  specific = 4
FEATURE [App::DocumentObjectGroupPython] O_element053  label="O_element : 0.072"  # scripted group (container) (typed FeaturePython)
  n = 0.071682
FEATURE [App::DocumentObjectGroupPython] Pb_element002  label="Pb_element : 0.928"  # scripted group (container) (typed FeaturePython)
  n = 0.928318
FEATURE [App::DocumentObjectGroupPython] G4_LEAD_OXIDE  # scripted group (container) (typed FeaturePython)
  Dunit = g/cm3
  Dvalue = 9.53
  Group = -> [O_element053,Pb_element002]
  conduct = 2
  density = 1
  expand = 3
  formula = G4_LEAD_OXIDE
  name = G4_LEAD_OXIDE
  specific = 4
FEATURE [App::DocumentObjectGroupPython] Li_element001  label="Li_element : 1"  # scripted group (container) (typed FeaturePython)
  n = 1
  ref = Li_element
FEATURE [App::DocumentObjectGroupPython] N_element022  label="N_element : 011"  # scripted group (container) (typed FeaturePython)
  n = 1
  ref = N_element
FEATURE [App::DocumentObjectGroupPython] H_element049  label="H_element : 026"  # scripted group (container) (typed FeaturePython)
  n = 2
  ref = H_element
FEATURE [App::DocumentObjectGroupPython] G4_LITHIUM_AMIDE  # scripted group (container) (typed FeaturePython)
  Dunit = g/cm3
  Dvalue = 1.178
  Group = -> [Li_element001,N_element022,H_element049]
  conduct = 2
  density = 1
  expand = 3
  formula = G4_LITHIUM_AMIDE
  name = G4_LITHIUM_AMIDE
  specific = 4
FEATURE [App::DocumentObjectGroupPython] Li_element002  label="Li_element : 2"  # scripted group (container) (typed FeaturePython)
  n = 2
  ref = Li_element
FEATURE [App::DocumentObjectGroupPython] C_element055  label="C_element : 030"  # scripted group (container) (typed FeaturePython)
  n = 1
  ref = C_element
FEATURE [App::DocumentObjectGroupPython] O_element054  label="O_element : 028"  # scripted group (container) (typed FeaturePython)
  n = 3
  ref = O_element
FEATURE [App::DocumentObjectGroupPython] G4_LITHIUM_CARBONATE  # scripted group (container) (typed FeaturePython)
  Dunit = g/cm3
  Dvalue = 2.11
  Group = -> [Li_element002,C_element055,O_element054]
  conduct = 2
  density = 1
  expand = 3
  formula = G4_LITHIUM_CARBONATE
  name = G4_LITHIUM_CARBONATE
  specific = 4
FEATURE [App::DocumentObjectGroupPython] Li_element003  label="Li_element : 003"  # scripted group (container) (typed FeaturePython)
  n = 1
  ref = Li_element
FEATURE [App::DocumentObjectGroupPython] F_element012  label="F_element : 004"  # scripted group (container) (typed FeaturePython)
  n = 1
  ref = F_element
FEATURE [App::DocumentObjectGroupPython] G4_LITHIUM_FLUORIDE  # scripted group (container) (typed FeaturePython)
  Dunit = g/cm3
  Dvalue = 2.635
  Group = -> [Li_element003,F_element012]
  conduct = 2
  density = 1
  expand = 3
  formula = G4_LITHIUM_FLUORIDE
  name = G4_LITHIUM_FLUORIDE
  specific = 4
FEATURE [App::DocumentObjectGroupPython] Li_element004  label="Li_element : 004"  # scripted group (container) (typed FeaturePython)
  n = 1
  ref = Li_element
FEATURE [App::DocumentObjectGroupPython] H_element050  label="H_element : 027"  # scripted group (container) (typed FeaturePython)
  n = 1
  ref = H_element
FEATURE [App::DocumentObjectGroupPython] G4_LITHIUM_HYDRIDE  # scripted group (container) (typed FeaturePython)
  Dunit = g/cm3
  Dvalue = 0.82
  Group = -> [Li_element004,H_element050]
  conduct = 2
  density = 1
  expand = 3
  formula = G4_LITHIUM_HYDRIDE
  name = G4_LITHIUM_HYDRIDE
  specific = 4
FEATURE [App::DocumentObjectGroupPython] Li_element005  label="Li_element : 005"  # scripted group (container) (typed FeaturePython)
  n = 1
  ref = Li_element
FEATURE [App::DocumentObjectGroupPython] I_element003  label="I_element : 002"  # scripted group (container) (typed FeaturePython)
  n = 1
  ref = I_element
FEATURE [App::DocumentObjectGroupPython] G4_LITHIUM_IODIDE  # scripted group (container) (typed FeaturePython)
  Dunit = g/cm3
  Dvalue = 3.494
  Group = -> [Li_element005,I_element003]
  conduct = 2
  density = 1
  expand = 3
  formula = G4_LITHIUM_IODIDE
  name = G4_LITHIUM_IODIDE
  specific = 4
FEATURE [App::DocumentObjectGroupPython] Li_element006  label="Li_element : 006"  # scripted group (container) (typed FeaturePython)
  n = 2
  ref = Li_element
FEATURE [App::DocumentObjectGroupPython] O_element055  label="O_element : 029"  # scripted group (container) (typed FeaturePython)
  n = 1
  ref = O_element
FEATURE [App::DocumentObjectGroupPython] G4_LITHIUM_OXIDE  # scripted group (container) (typed FeaturePython)
  Dunit = g/cm3
  Dvalue = 2.013
  Group = -> [Li_element006,O_element055]
  conduct = 2
  density = 1
  expand = 3
  formula = G4_LITHIUM_OXIDE
  name = G4_LITHIUM_OXIDE
  specific = 4
FEATURE [App::DocumentObjectGroupPython] Li_element007  label="Li_element : 007"  # scripted group (container) (typed FeaturePython)
  n = 2
  ref = Li_element
FEATURE [App::DocumentObjectGroupPython] B_element005  label="B_element : 005"  # scripted group (container) (typed FeaturePython)
  n = 4
  ref = B_element
FEATURE [App::DocumentObjectGroupPython] O_element056  label="O_element : 7"  # scripted group (container) (typed FeaturePython)
  n = 7
  ref = O_element
FEATURE [App::DocumentObjectGroupPython] G4_LITHIUM_TETRABORATE  # scripted group (container) (typed FeaturePython)
  Dunit = g/cm3
  Dvalue = 2.44
  Group = -> [Li_element007,B_element005,O_element056]
  conduct = 2
  density = 1
  expand = 3
  formula = G4_LITHIUM_TETRABORATE
  name = G4_LITHIUM_TETRABORATE
  specific = 4
FEATURE [App::DocumentObjectGroupPython] H_element051  label="H_element : 0.105"  # scripted group (container) (typed FeaturePython)
  n = 0.105
FEATURE [App::DocumentObjectGroupPython] C_element056  label="C_element : 0.083"  # scripted group (container) (typed FeaturePython)
  n = 0.083
FEATURE [App::DocumentObjectGroupPython] N_element023  label="N_element : 0.023"  # scripted group (container) (typed FeaturePython)
  n = 0.023
FEATURE [App::DocumentObjectGroupPython] O_element057  label="O_element : 0.779"  # scripted group (container) (typed FeaturePython)
  n = 0.779
FEATURE [App::DocumentObjectGroupPython] Na_element010  label="Na_element : 0.097"  # scripted group (container) (typed FeaturePython)
  n = 0.002
FEATURE [App::DocumentObjectGroupPython] P_element006  label="P_element : 0.105"  # scripted group (container) (typed FeaturePython)
  n = 0.001
FEATURE [App::DocumentObjectGroupPython] S_element016  label="S_element : 0.017"  # scripted group (container) (typed FeaturePython)
  n = 0.002
FEATURE [App::DocumentObjectGroupPython] Cl_element014  label="Cl_element : 0.587"  # scripted group (container) (typed FeaturePython)
  n = 0.003
FEATURE [App::DocumentObjectGroupPython] K_element005  label="K_element : 0.015"  # scripted group (container) (typed FeaturePython)
  n = 0.002
FEATURE [App::DocumentObjectGroupPython] G4_LUNG_ICRP  # scripted group (container) (typed FeaturePython)
  Dunit = g/cm3
  Dvalue = 1.04
  Group = -> [H_element051,C_element056,N_element023,O_element057,Na_element010,P_element006,S_element016,Cl_element014,K_element005]
  conduct = 2
  density = 1
  expand = 3
  formula = G4_LUNG_ICRP
  name = G4_LUNG_ICRP
  specific = 4
FEATURE [App::DocumentObjectGroupPython] H_element052  label="H_element : 0.116"  # scripted group (container) (typed FeaturePython)
  n = 0.114318
FEATURE [App::DocumentObjectGroupPython] C_element057  label="C_element : 0.656"  # scripted group (container) (typed FeaturePython)
  n = 0.655824
FEATURE [App::DocumentObjectGroupPython] O_element058  label="O_element : 0.092"  # scripted group (container) (typed FeaturePython)
  n = 0.0921831
FEATURE [App::DocumentObjectGroupPython] Mg_element004  label="Mg_element : 0.135"  # scripted group (container) (typed FeaturePython)
  n = 0.134792
FEATURE [App::DocumentObjectGroupPython] Ca_element013  label="Ca_element : 0.003"  # scripted group (container) (typed FeaturePython)
  n = 0.002883
FEATURE [App::DocumentObjectGroupPython] G4_M3_WAX  # scripted group (container) (typed FeaturePython)
  Dunit = g/cm3
  Dvalue = 1.05
  Group = -> [H_element052,C_element057,O_element058,Mg_element004,Ca_element013]
  conduct = 2
  density = 1
  expand = 3
  formula = G4_M3_WAX
  name = G4_M3_WAX
  specific = 4
FEATURE [App::DocumentObjectGroupPython] Mg_element005  label="Mg_element : 1"  # scripted group (container) (typed FeaturePython)
  n = 1
  ref = Mg_element
FEATURE [App::DocumentObjectGroupPython] C_element058  label="C_element : 031"  # scripted group (container) (typed FeaturePython)
  n = 1
  ref = C_element
FEATURE [App::DocumentObjectGroupPython] O_element059  label="O_element : 030"  # scripted group (container) (typed FeaturePython)
  n = 3
  ref = O_element
FEATURE [App::DocumentObjectGroupPython] G4_MAGNESIUM_CARBONATE  # scripted group (container) (typed FeaturePython)
  Dunit = g/cm3
  Dvalue = 2.958
  Group = -> [Mg_element005,C_element058,O_element059]
  conduct = 2
  density = 1
  expand = 3
  formula = G4_MAGNESIUM_CARBONATE
  name = G4_MAGNESIUM_CARBONATE
  specific = 4
FEATURE [App::DocumentObjectGroupPython] Mg_element006  label="Mg_element : 002"  # scripted group (container) (typed FeaturePython)
  n = 1
  ref = Mg_element
FEATURE [App::DocumentObjectGroupPython] F_element013  label="F_element : 005"  # scripted group (container) (typed FeaturePython)
  n = 2
  ref = F_element
FEATURE [App::DocumentObjectGroupPython] G4_MAGNESIUM_FLUORIDE  # scripted group (container) (typed FeaturePython)
  Dunit = g/cm3
  Dvalue = 3
  Group = -> [Mg_element006,F_element013]
  conduct = 2
  density = 1
  expand = 3
  formula = G4_MAGNESIUM_FLUORIDE
  name = G4_MAGNESIUM_FLUORIDE
  specific = 4
FEATURE [App::DocumentObjectGroupPython] Mg_element007  label="Mg_element : 003"  # scripted group (container) (typed FeaturePython)
  n = 1
  ref = Mg_element
FEATURE [App::DocumentObjectGroupPython] O_element060  label="O_element : 031"  # scripted group (container) (typed FeaturePython)
  n = 1
  ref = O_element
FEATURE [App::DocumentObjectGroupPython] G4_MAGNESIUM_OXIDE  # scripted group (container) (typed FeaturePython)
  Dunit = g/cm3
  Dvalue = 3.58
  Group = -> [Mg_element007,O_element060]
  conduct = 2
  density = 1
  expand = 3
  formula = G4_MAGNESIUM_OXIDE
  name = G4_MAGNESIUM_OXIDE
  specific = 4
FEATURE [App::DocumentObjectGroupPython] Mg_element008  label="Mg_element : 004"  # scripted group (container) (typed FeaturePython)
  n = 1
  ref = Mg_element
FEATURE [App::DocumentObjectGroupPython] B_element006  label="B_element : 006"  # scripted group (container) (typed FeaturePython)
  n = 4
  ref = B_element
FEATURE [App::DocumentObjectGroupPython] O_element061  label="O_element : 032"  # scripted group (container) (typed FeaturePython)
  n = 7
  ref = O_element
FEATURE [App::DocumentObjectGroupPython] G4_MAGNESIUM_TETRABORATE  # scripted group (container) (typed FeaturePython)
  Dunit = g/cm3
  Dvalue = 2.53
  Group = -> [Mg_element008,B_element006,O_element061]
  conduct = 2
  density = 1
  expand = 3
  formula = G4_MAGNESIUM_TETRABORATE
  name = G4_MAGNESIUM_TETRABORATE
  specific = 4
FEATURE [App::DocumentObjectGroupPython] Hg_element001  label="Hg_element : 1"  # scripted group (container) (typed FeaturePython)
  n = 1
  ref = Hg_element
FEATURE [App::DocumentObjectGroupPython] I_element004  label="I_element : 2"  # scripted group (container) (typed FeaturePython)
  n = 2
  ref = I_element
FEATURE [App::DocumentObjectGroupPython] G4_MERCURIC_IODIDE  # scripted group (container) (typed FeaturePython)
  Dunit = g/cm3
  Dvalue = 6.36
  Group = -> [Hg_element001,I_element004]
  conduct = 2
  density = 1
  expand = 3
  formula = G4_MERCURIC_IODIDE
  name = G4_MERCURIC_IODIDE
  specific = 4
FEATURE [App::DocumentObjectGroupPython] C_element059  label="C_element : 032"  # scripted group (container) (typed FeaturePython)
  n = 1
  ref = C_element
FEATURE [App::DocumentObjectGroupPython] H_element053  label="H_element : 028"  # scripted group (container) (typed FeaturePython)
  n = 4
  ref = H_element
FEATURE [App::DocumentObjectGroupPython] G4_METHANE  # scripted group (container) (typed FeaturePython)
  Dunit = g/cm3
  Dvalue = 0.000667151
  Group = -> [C_element059,H_element053]
  conduct = 2
  density = 1
  expand = 3
  formula = G4_METHANE
  name = G4_METHANE
  specific = 4
FEATURE [App::DocumentObjectGroupPython] C_element060  label="C_element : 033"  # scripted group (container) (typed FeaturePython)
  n = 1
  ref = C_element
FEATURE [App::DocumentObjectGroupPython] H_element054  label="H_element : 029"  # scripted group (container) (typed FeaturePython)
  n = 4
  ref = H_element
FEATURE [App::DocumentObjectGroupPython] O_element062  label="O_element : 033"  # scripted group (container) (typed FeaturePython)
  n = 1
  ref = O_element
FEATURE [App::DocumentObjectGroupPython] G4_METHANOL  # scripted group (container) (typed FeaturePython)
  Dunit = g/cm3
  Dvalue = 0.7914
  Group = -> [C_element060,H_element054,O_element062]
  conduct = 2
  density = 1
  expand = 3
  formula = G4_METHANOL
  name = G4_METHANOL
  specific = 4
FEATURE [App::DocumentObjectGroupPython] H_element055  label="H_element : 0.134"  # scripted group (container) (typed FeaturePython)
  n = 0.13404
FEATURE [App::DocumentObjectGroupPython] C_element061  label="C_element : 0.778"  # scripted group (container) (typed FeaturePython)
  n = 0.77796
FEATURE [App::DocumentObjectGroupPython] O_element063  label="O_element : 0.035"  # scripted group (container) (typed FeaturePython)
  n = 0.03502
FEATURE [App::DocumentObjectGroupPython] Mg_element009  label="Mg_element : 0.039"  # scripted group (container) (typed FeaturePython)
  n = 0.038594
FEATURE [App::DocumentObjectGroupPython] Ti_element002  label="Ti_element : 0.014"  # scripted group (container) (typed FeaturePython)
  n = 0.014386
FEATURE [App::DocumentObjectGroupPython] G4_MIX_D_WAX  # scripted group (container) (typed FeaturePython)
  Dunit = g/cm3
  Dvalue = 0.99
  Group = -> [H_element055,C_element061,O_element063,Mg_element009,Ti_element002]
  conduct = 2
  density = 1
  expand = 3
  formula = G4_MIX_D_WAX
  name = G4_MIX_D_WAX
  specific = 4
FEATURE [App::DocumentObjectGroupPython] H_element056  label="H_element : 0.135"  # scripted group (container) (typed FeaturePython)
  n = 0.081192
FEATURE [App::DocumentObjectGroupPython] C_element062  label="C_element : 0.583"  # scripted group (container) (typed FeaturePython)
  n = 0.583442
FEATURE [App::DocumentObjectGroupPython] N_element024  label="N_element : 0.018"  # scripted group (container) (typed FeaturePython)
  n = 0.017798
FEATURE [App::DocumentObjectGroupPython] O_element064  label="O_element : 0.186"  # scripted group (container) (typed FeaturePython)
  n = 0.186381
FEATURE [App::DocumentObjectGroupPython] Mg_element010  label="Mg_element : 0.130"  # scripted group (container) (typed FeaturePython)
  n = 0.130287
FEATURE [App::DocumentObjectGroupPython] Cl_element015  label="Cl_element : 0.588"  # scripted group (container) (typed FeaturePython)
  n = 0.0009
FEATURE [App::DocumentObjectGroupPython] G4_MS20_TISSUE  # scripted group (container) (typed FeaturePython)
  Dunit = g/cm3
  Dvalue = 1
  Group = -> [H_element056,C_element062,N_element024,O_element064,Mg_element010,Cl_element015]
  conduct = 2
  density = 1
  expand = 3
  formula = G4_MS20_TISSUE
  name = G4_MS20_TISSUE
  specific = 4
FEATURE [App::DocumentObjectGroupPython] H_element057  label="H_element : 0.136"  # scripted group (container) (typed FeaturePython)
  n = 0.102
FEATURE [App::DocumentObjectGroupPython] C_element063  label="C_element : 0.143"  # scripted group (container) (typed FeaturePython)
  n = 0.143
FEATURE [App::DocumentObjectGroupPython] N_element025  label="N_element : 0.034"  # scripted group (container) (typed FeaturePython)
  n = 0.034
FEATURE [App::DocumentObjectGroupPython] O_element065  label="O_element : 0.710"  # scripted group (container) (typed FeaturePython)
  n = 0.71
FEATURE [App::DocumentObjectGroupPython] Na_element011  label="Na_element : 0.098"  # scripted group (container) (typed FeaturePython)
  n = 0.001
FEATURE [App::DocumentObjectGroupPython] P_element007  label="P_element : 0.002"  # scripted group (container) (typed FeaturePython)
  n = 0.002
FEATURE [App::DocumentObjectGroupPython] S_element017  label="S_element : 0.018"  # scripted group (container) (typed FeaturePython)
  n = 0.003
FEATURE [App::DocumentObjectGroupPython] Cl_element016  label="Cl_element : 0.589"  # scripted group (container) (typed FeaturePython)
  n = 0.001
FEATURE [App::DocumentObjectGroupPython] K_element006  label="K_element : 0.004"  # scripted group (container) (typed FeaturePython)
  n = 0.004
FEATURE [App::DocumentObjectGroupPython] G4_MUSCLE_SKELETAL_ICRP  # scripted group (container) (typed FeaturePython)
  Dunit = g/cm3
  Dvalue = 1.05
  Group = -> [H_element057,C_element063,N_element025,O_element065,Na_element011,P_element007,S_element017,Cl_element016,K_element006]
  conduct = 2
  density = 1
  expand = 3
  formula = G4_MUSCLE_SKELETAL_ICRP
  name = G4_MUSCLE_SKELETAL_ICRP
  specific = 4
FEATURE [App::DocumentObjectGroupPython] H_element058  label="H_element : 0.137"  # scripted group (container) (typed FeaturePython)
  n = 0.102102
FEATURE [App::DocumentObjectGroupPython] C_element064  label="C_element : 0.123"  # scripted group (container) (typed FeaturePython)
  n = 0.123123
FEATURE [App::DocumentObjectGroupPython] N_element026  label="N_element : 0.756"  # scripted group (container) (typed FeaturePython)
  n = 0.035035
FEATURE [App::DocumentObjectGroupPython] O_element066  label="O_element : 0.730"  # scripted group (container) (typed FeaturePython)
  n = 0.72973
FEATURE [App::DocumentObjectGroupPython] Na_element012  label="Na_element : 0.099"  # scripted group (container) (typed FeaturePython)
  n = 0.001001
FEATURE [App::DocumentObjectGroupPython] P_element008  label="P_element : 0.106"  # scripted group (container) (typed FeaturePython)
  n = 0.002002
FEATURE [App::DocumentObjectGroupPython] S_element018  label="S_element : 0.019"  # scripted group (container) (typed FeaturePython)
  n = 0.004004
FEATURE [App::DocumentObjectGroupPython] K_element007  label="K_element : 0.016"  # scripted group (container) (typed FeaturePython)
  n = 0.003003
FEATURE [App::DocumentObjectGroupPython] G4_MUSCLE_STRIATED_ICRU  # scripted group (container) (typed FeaturePython)
  Dunit = g/cm3
  Dvalue = 1.04
  Group = -> [H_element058,C_element064,N_element026,O_element066,Na_element012,P_element008,S_element018,K_element007]
  conduct = 2
  density = 1
  expand = 3
  formula = G4_MUSCLE_STRIATED_ICRU
  name = G4_MUSCLE_STRIATED_ICRU
  specific = 4
FEATURE [App::DocumentObjectGroupPython] H_element059  label="H_element : 0.098"  # scripted group (container) (typed FeaturePython)
  n = 0.0982341
FEATURE [App::DocumentObjectGroupPython] C_element065  label="C_element : 0.156"  # scripted group (container) (typed FeaturePython)
  n = 0.156214
FEATURE [App::DocumentObjectGroupPython] N_element027  label="N_element : 0.757"  # scripted group (container) (typed FeaturePython)
  n = 0.035451
FEATURE [App::DocumentObjectGroupPython] O_element067  label="O_element : 0.880"  # scripted group (container) (typed FeaturePython)
  n = 0.710101
FEATURE [App::DocumentObjectGroupPython] G4_MUSCLE_WITH_SUCROSE  # scripted group (container) (typed FeaturePython)
  Dunit = g/cm3
  Dvalue = 1.11
  Group = -> [H_element059,C_element065,N_element027,O_element067]
  conduct = 2
  density = 1
  expand = 3
  formula = G4_MUSCLE_WITH_SUCROSE
  name = G4_MUSCLE_WITH_SUCROSE
  specific = 4
FEATURE [App::DocumentObjectGroupPython] H_element060  label="H_element : 0.138"  # scripted group (container) (typed FeaturePython)
  n = 0.101969
FEATURE [App::DocumentObjectGroupPython] C_element066  label="C_element : 0.120"  # scripted group (container) (typed FeaturePython)
  n = 0.120058
FEATURE [App::DocumentObjectGroupPython] N_element028  label="N_element : 0.758"  # scripted group (container) (typed FeaturePython)
  n = 0.035451
FEATURE [App::DocumentObjectGroupPython] O_element068  label="O_element : 0.743"  # scripted group (container) (typed FeaturePython)
  n = 0.742522
FEATURE [App::DocumentObjectGroupPython] G4_MUSCLE_WITHOUT_SUCROSE  # scripted group (container) (typed FeaturePython)
  Dunit = g/cm3
  Dvalue = 1.07
  Group = -> [H_element060,C_element066,N_element028,O_element068]
  conduct = 2
  density = 1
  expand = 3
  formula = G4_MUSCLE_WITHOUT_SUCROSE
  name = G4_MUSCLE_WITHOUT_SUCROSE
  specific = 4
FEATURE [App::DocumentObjectGroupPython] C_element067  label="C_element : 10"  # scripted group (container) (typed FeaturePython)
  n = 10
  ref = C_element
FEATURE [App::DocumentObjectGroupPython] H_element061  label="H_element : 030"  # scripted group (container) (typed FeaturePython)
  n = 8
  ref = H_element
FEATURE [App::DocumentObjectGroupPython] G4_NAPHTHALENE  # scripted group (container) (typed FeaturePython)
  Dunit = g/cm3
  Dvalue = 1.145
  Group = -> [C_element067,H_element061]
  conduct = 2
  density = 1
  expand = 3
  formula = G4_NAPHTHALENE
  name = G4_NAPHTHALENE
  specific = 4
FEATURE [App::DocumentObjectGroupPython] C_element068  label="C_element : 034"  # scripted group (container) (typed FeaturePython)
  n = 6
  ref = C_element
FEATURE [App::DocumentObjectGroupPython] H_element062  label="H_element : 031"  # scripted group (container) (typed FeaturePython)
  n = 5
  ref = H_element
FEATURE [App::DocumentObjectGroupPython] N_element029  label="N_element : 012"  # scripted group (container) (typed FeaturePython)
  n = 1
  ref = N_element
FEATURE [App::DocumentObjectGroupPython] O_element069  label="O_element : 034"  # scripted group (container) (typed FeaturePython)
  n = 2
  ref = O_element
FEATURE [App::DocumentObjectGroupPython] G4_NITROBENZENE  # scripted group (container) (typed FeaturePython)
  Dunit = g/cm3
  Dvalue = 1.19867
  Group = -> [C_element068,H_element062,N_element029,O_element069]
  conduct = 2
  density = 1
  expand = 3
  formula = G4_NITROBENZENE
  name = G4_NITROBENZENE
  specific = 4
FEATURE [App::DocumentObjectGroupPython] N_element030  label="N_element : 013"  # scripted group (container) (typed FeaturePython)
  n = 2
  ref = N_element
FEATURE [App::DocumentObjectGroupPython] O_element070  label="O_element : 035"  # scripted group (container) (typed FeaturePython)
  n = 1
  ref = O_element
FEATURE [App::DocumentObjectGroupPython] G4_NITROUS_OXIDE  # scripted group (container) (typed FeaturePython)
  Dunit = g/cm3
  Dvalue = 0.00183094
  Group = -> [N_element030,O_element070]
  conduct = 2
  density = 1
  expand = 3
  formula = G4_NITROUS_OXIDE
  name = G4_NITROUS_OXIDE
  specific = 4
FEATURE [App::DocumentObjectGroupPython] H_element063  label="H_element : 0.104"  # scripted group (container) (typed FeaturePython)
  n = 0.103509
FEATURE [App::DocumentObjectGroupPython] C_element069  label="C_element : 0.648"  # scripted group (container) (typed FeaturePython)
  n = 0.648416
FEATURE [App::DocumentObjectGroupPython] N_element031  label="N_element : 0.100"  # scripted group (container) (typed FeaturePython)
  n = 0.0995361
FEATURE [App::DocumentObjectGroupPython] O_element071  label="O_element : 0.149"  # scripted group (container) (typed FeaturePython)
  n = 0.148539
FEATURE [App::DocumentObjectGroupPython] G4_NYLON_8062  label="G4_NYLON-8062"  # scripted group (container) (typed FeaturePython)
  Dunit = g/cm3
  Dvalue = 1.08
  Group = -> [H_element063,C_element069,N_element031,O_element071]
  conduct = 2
  density = 1
  expand = 3
  formula = G4_NYLON-8062
  name = G4_NYLON-8062
  specific = 4
FEATURE [App::DocumentObjectGroupPython] C_element070  label="C_element : 035"  # scripted group (container) (typed FeaturePython)
  n = 6
  ref = C_element
FEATURE [App::DocumentObjectGroupPython] H_element064  label="H_element : 11"  # scripted group (container) (typed FeaturePython)
  n = 11
  ref = H_element
FEATURE [App::DocumentObjectGroupPython] N_element032  label="N_element : 014"  # scripted group (container) (typed FeaturePython)
  n = 1
  ref = N_element
FEATURE [App::DocumentObjectGroupPython] O_element072  label="O_element : 036"  # scripted group (container) (typed FeaturePython)
  n = 1
  ref = O_element
FEATURE [App::DocumentObjectGroupPython] G4_NYLON_6_6  label="G4_NYLON-6-6"  # scripted group (container) (typed FeaturePython)
  Dunit = g/cm3
  Dvalue = 1.14
  Group = -> [C_element070,H_element064,N_element032,O_element072]
  conduct = 2
  density = 1
  expand = 3
  formula = G4_NYLON-6-6
  name = G4_NYLON-6-6
  specific = 4
FEATURE [App::DocumentObjectGroupPython] H_element065  label="H_element : 0.139"  # scripted group (container) (typed FeaturePython)
  n = 0.107062
FEATURE [App::DocumentObjectGroupPython] C_element071  label="C_element : 0.680"  # scripted group (container) (typed FeaturePython)
  n = 0.680449
FEATURE [App::DocumentObjectGroupPython] N_element033  label="N_element : 0.099"  # scripted group (container) (typed FeaturePython)
  n = 0.099189
FEATURE [App::DocumentObjectGroupPython] O_element073  label="O_element : 0.113"  # scripted group (container) (typed FeaturePython)
  n = 0.1133
FEATURE [App::DocumentObjectGroupPython] G4_NYLON_6_10  label="G4_NYLON-6-10"  # scripted group (container) (typed FeaturePython)
  Dunit = g/cm3
  Dvalue = 1.14
  Group = -> [H_element065,C_element071,N_element033,O_element073]
  conduct = 2
  density = 1
  expand = 3
  formula = G4_NYLON-6-10
  name = G4_NYLON-6-10
  specific = 4
FEATURE [App::DocumentObjectGroupPython] H_element066  label="H_element : 0.140"  # scripted group (container) (typed FeaturePython)
  n = 0.115476
FEATURE [App::DocumentObjectGroupPython] C_element072  label="C_element : 0.721"  # scripted group (container) (typed FeaturePython)
  n = 0.720818
FEATURE [App::DocumentObjectGroupPython] N_element034  label="N_element : 0.076"  # scripted group (container) (typed FeaturePython)
  n = 0.0764169
FEATURE [App::DocumentObjectGroupPython] O_element074  label="O_element : 0.087"  # scripted group (container) (typed FeaturePython)
  n = 0.0872889
FEATURE [App::DocumentObjectGroupPython] G4_NYLON_11_RILSAN  label="G4_NYLON-11_RILSAN"  # scripted group (container) (typed FeaturePython)
  Dunit = g/cm3
  Dvalue = 1.425
  Group = -> [H_element066,C_element072,N_element034,O_element074]
  conduct = 2
  density = 1
  expand = 3
  formula = G4_NYLON-11_RILSAN
  name = G4_NYLON-11_RILSAN
  specific = 4
FEATURE [App::DocumentObjectGroupPython] C_element073  label="C_element : 8"  # scripted group (container) (typed FeaturePython)
  n = 8
  ref = C_element
FEATURE [App::DocumentObjectGroupPython] H_element067  label="H_element : 18"  # scripted group (container) (typed FeaturePython)
  n = 18
  ref = H_element
FEATURE [App::DocumentObjectGroupPython] G4_OCTANE  # scripted group (container) (typed FeaturePython)
  Dunit = g/cm3
  Dvalue = 0.7026
  Group = -> [C_element073,H_element067]
  conduct = 2
  density = 1
  expand = 3
  formula = G4_OCTANE
  name = G4_OCTANE
  specific = 4
FEATURE [App::DocumentObjectGroupPython] C_element074  label="C_element : 25"  # scripted group (container) (typed FeaturePython)
  n = 25
  ref = C_element
FEATURE [App::DocumentObjectGroupPython] H_element068  label="H_element : 52"  # scripted group (container) (typed FeaturePython)
  n = 52
  ref = H_element
FEATURE [App::DocumentObjectGroupPython] G4_PARAFFIN  # scripted group (container) (typed FeaturePython)
  Dunit = g/cm3
  Dvalue = 0.93
  Group = -> [C_element074,H_element068]
  conduct = 2
  density = 1
  expand = 3
  formula = G4_PARAFFIN
  name = G4_PARAFFIN
  specific = 4
FEATURE [App::DocumentObjectGroupPython] C_element075  label="C_element : 036"  # scripted group (container) (typed FeaturePython)
  n = 5
  ref = C_element
FEATURE [App::DocumentObjectGroupPython] H_element069  label="H_element : 032"  # scripted group (container) (typed FeaturePython)
  n = 12
  ref = H_element
FEATURE [App::DocumentObjectGroupPython] G4_N_PENTANE  label="G4_N-PENTANE"  # scripted group (container) (typed FeaturePython)
  Dunit = g/cm3
  Dvalue = 0.6262
  Group = -> [C_element075,H_element069]
  conduct = 2
  density = 1
  expand = 3
  formula = G4_N-PENTANE
  name = G4_N-PENTANE
  specific = 4
FEATURE [App::DocumentObjectGroupPython] H_element070  label="H_element : 0.014"  # scripted group (container) (typed FeaturePython)
  n = 0.0141
FEATURE [App::DocumentObjectGroupPython] C_element076  label="C_element : 0.072"  # scripted group (container) (typed FeaturePython)
  n = 0.072261
FEATURE [App::DocumentObjectGroupPython] N_element035  label="N_element : 0.019"  # scripted group (container) (typed FeaturePython)
  n = 0.01932
FEATURE [App::DocumentObjectGroupPython] O_element075  label="O_element : 0.066"  # scripted group (container) (typed FeaturePython)
  n = 0.066101
FEATURE [App::DocumentObjectGroupPython] S_element019  label="S_element : 0.020"  # scripted group (container) (typed FeaturePython)
  n = 0.00189
FEATURE [App::DocumentObjectGroupPython] Br_element004  label="Br_element : 0.349"  # scripted group (container) (typed FeaturePython)
  n = 0.349103
FEATURE [App::DocumentObjectGroupPython] Ag_element001  label="Ag_element : 0.474"  # scripted group (container) (typed FeaturePython)
  n = 0.474105
FEATURE [App::DocumentObjectGroupPython] I_element005  label="I_element : 0.003"  # scripted group (container) (typed FeaturePython)
  n = 0.00312
FEATURE [App::DocumentObjectGroupPython] G4_PHOTO_EMULSION  # scripted group (container) (typed FeaturePython)
  Dunit = g/cm3
  Dvalue = 3.815
  Group = -> [H_element070,C_element076,N_element035,O_element075,S_element019,Br_element004,Ag_element001,I_element005]
  conduct = 2
  density = 1
  expand = 3
  formula = G4_PHOTO_EMULSION
  name = G4_PHOTO_EMULSION
  specific = 4
FEATURE [App::DocumentObjectGroupPython] C_element077  label="C_element : 9"  # scripted group (container) (typed FeaturePython)
  n = 9
  ref = C_element
FEATURE [App::DocumentObjectGroupPython] H_element071  label="H_element : 033"  # scripted group (container) (typed FeaturePython)
  n = 10
  ref = H_element
FEATURE [App::DocumentObjectGroupPython] G4_PLASTIC_SC_VINYLTOLUENE  # scripted group (container) (typed FeaturePython)
  Dunit = g/cm3
  Dvalue = 1.032
  Group = -> [C_element077,H_element071]
  conduct = 2
  density = 1
  expand = 3
  formula = G4_PLASTIC_SC_VINYLTOLUENE
  name = G4_PLASTIC_SC_VINYLTOLUENE
  specific = 4
FEATURE [App::DocumentObjectGroupPython] Pu_element001  label="Pu_element : 1"  # scripted group (container) (typed FeaturePython)
  n = 1
  ref = Pu_element
FEATURE [App::DocumentObjectGroupPython] O_element076  label="O_element : 037"  # scripted group (container) (typed FeaturePython)
  n = 2
  ref = O_element
FEATURE [App::DocumentObjectGroupPython] G4_PLUTONIUM_DIOXIDE  # scripted group (container) (typed FeaturePython)
  Dunit = g/cm3
  Dvalue = 11.46
  Group = -> [Pu_element001,O_element076]
  conduct = 2
  density = 1
  expand = 3
  formula = G4_PLUTONIUM_DIOXIDE
  name = G4_PLUTONIUM_DIOXIDE
  specific = 4
FEATURE [App::DocumentObjectGroupPython] C_element078  label="C_element : 037"  # scripted group (container) (typed FeaturePython)
  n = 3
  ref = C_element
FEATURE [App::DocumentObjectGroupPython] H_element072  label="H_element : 034"  # scripted group (container) (typed FeaturePython)
  n = 3
  ref = H_element
FEATURE [App::DocumentObjectGroupPython] N_element036  label="N_element : 015"  # scripted group (container) (typed FeaturePython)
  n = 1
  ref = N_element
FEATURE [App::DocumentObjectGroupPython] G4_POLYACRYLONITRILE  # scripted group (container) (typed FeaturePython)
  Dunit = g/cm3
  Dvalue = 1.17
  Group = -> [C_element078,H_element072,N_element036]
  conduct = 2
  density = 1
  expand = 3
  formula = G4_POLYACRYLONITRILE
  name = G4_POLYACRYLONITRILE
  specific = 4
FEATURE [App::DocumentObjectGroupPython] C_element079  label="C_element : 16"  # scripted group (container) (typed FeaturePython)
  n = 16
  ref = C_element
FEATURE [App::DocumentObjectGroupPython] H_element073  label="H_element : 035"  # scripted group (container) (typed FeaturePython)
  n = 14
  ref = H_element
FEATURE [App::DocumentObjectGroupPython] O_element077  label="O_element : 038"  # scripted group (container) (typed FeaturePython)
  n = 3
  ref = O_element
FEATURE [App::DocumentObjectGroupPython] G4_POLYCARBONATE  # scripted group (container) (typed FeaturePython)
  Dunit = g/cm3
  Dvalue = 1.2
  Group = -> [C_element079,H_element073,O_element077]
  conduct = 2
  density = 1
  expand = 3
  formula = G4_POLYCARBONATE
  name = G4_POLYCARBONATE
  specific = 4
FEATURE [App::DocumentObjectGroupPython] C_element080  label="C_element : 038"  # scripted group (container) (typed FeaturePython)
  n = 8
  ref = C_element
FEATURE [App::DocumentObjectGroupPython] H_element074  label="H_element : 036"  # scripted group (container) (typed FeaturePython)
  n = 7
  ref = H_element
FEATURE [App::DocumentObjectGroupPython] Cl_element017  label="Cl_element : 007"  # scripted group (container) (typed FeaturePython)
  n = 1
  ref = Cl_element
FEATURE [App::DocumentObjectGroupPython] G4_POLYCHLOROSTYRENE  # scripted group (container) (typed FeaturePython)
  Dunit = g/cm3
  Dvalue = 1.3
  Group = -> [C_element080,H_element074,Cl_element017]
  conduct = 2
  density = 1
  expand = 3
  formula = G4_POLYCHLOROSTYRENE
  name = G4_POLYCHLOROSTYRENE
  specific = 4
FEATURE [App::DocumentObjectGroupPython] C_element081  label="C_element : 039"  # scripted group (container) (typed FeaturePython)
  n = 1
  ref = C_element
FEATURE [App::DocumentObjectGroupPython] H_element075  label="H_element : 037"  # scripted group (container) (typed FeaturePython)
  n = 2
  ref = H_element
FEATURE [App::DocumentObjectGroupPython] G4_POLYETHYLENE  # scripted group (container) (typed FeaturePython)
  Dunit = g/cm3
  Dvalue = 0.94
  Group = -> [C_element081,H_element075]
  conduct = 2
  density = 1
  expand = 3
  formula = G4_POLYETHYLENE
  name = G4_POLYETHYLENE
  specific = 4
FEATURE [App::DocumentObjectGroupPython] C_element082  label="C_element : 040"  # scripted group (container) (typed FeaturePython)
  n = 10
  ref = C_element
FEATURE [App::DocumentObjectGroupPython] H_element076  label="H_element : 038"  # scripted group (container) (typed FeaturePython)
  n = 8
  ref = H_element
FEATURE [App::DocumentObjectGroupPython] O_element078  label="O_element : 039"  # scripted group (container) (typed FeaturePython)
  n = 4
  ref = O_element
FEATURE [App::DocumentObjectGroupPython] G4_MYLAR  # scripted group (container) (typed FeaturePython)
  Dunit = g/cm3
  Dvalue = 1.4
  Group = -> [C_element082,H_element076,O_element078]
  conduct = 2
  density = 1
  expand = 3
  formula = G4_MYLAR
  name = G4_MYLAR
  specific = 4
FEATURE [App::DocumentObjectGroupPython] C_element083  label="C_element : 041"  # scripted group (container) (typed FeaturePython)
  n = 5
  ref = C_element
FEATURE [App::DocumentObjectGroupPython] H_element077  label="H_element : 039"  # scripted group (container) (typed FeaturePython)
  n = 8
  ref = H_element
FEATURE [App::DocumentObjectGroupPython] O_element079  label="O_element : 040"  # scripted group (container) (typed FeaturePython)
  n = 2
  ref = O_element
FEATURE [App::DocumentObjectGroupPython] G4_PLEXIGLASS  # scripted group (container) (typed FeaturePython)
  Dunit = g/cm3
  Dvalue = 1.19
  Group = -> [C_element083,H_element077,O_element079]
  conduct = 2
  density = 1
  expand = 3
  formula = G4_PLEXIGLASS
  name = G4_PLEXIGLASS
  specific = 4
FEATURE [App::DocumentObjectGroupPython] C_element084  label="C_element : 042"  # scripted group (container) (typed FeaturePython)
  n = 1
  ref = C_element
FEATURE [App::DocumentObjectGroupPython] H_element078  label="H_element : 040"  # scripted group (container) (typed FeaturePython)
  n = 2
  ref = H_element
FEATURE [App::DocumentObjectGroupPython] O_element080  label="O_element : 041"  # scripted group (container) (typed FeaturePython)
  n = 1
  ref = O_element
FEATURE [App::DocumentObjectGroupPython] G4_POLYOXYMETHYLENE  # scripted group (container) (typed FeaturePython)
  Dunit = g/cm3
  Dvalue = 1.425
  Group = -> [C_element084,H_element078,O_element080]
  conduct = 2
  density = 1
  expand = 3
  formula = G4_POLYOXYMETHYLENE
  name = G4_POLYOXYMETHYLENE
  specific = 4
FEATURE [App::DocumentObjectGroupPython] C_element085  label="C_element : 043"  # scripted group (container) (typed FeaturePython)
  n = 2
  ref = C_element
FEATURE [App::DocumentObjectGroupPython] H_element079  label="H_element : 041"  # scripted group (container) (typed FeaturePython)
  n = 4
  ref = H_element
FEATURE [App::DocumentObjectGroupPython] G4_POLYPROPYLENE  # scripted group (container) (typed FeaturePython)
  Dunit = g/cm3
  Dvalue = 0.9
  Group = -> [C_element085,H_element079]
  conduct = 2
  density = 1
  expand = 3
  formula = G4_POLYPROPYLENE
  name = G4_POLYPROPYLENE
  specific = 4
FEATURE [App::DocumentObjectGroupPython] C_element086  label="C_element : 044"  # scripted group (container) (typed FeaturePython)
  n = 8
  ref = C_element
FEATURE [App::DocumentObjectGroupPython] H_element080  label="H_element : 042"  # scripted group (container) (typed FeaturePython)
  n = 8
  ref = H_element
FEATURE [App::DocumentObjectGroupPython] G4_POLYSTYRENE  # scripted group (container) (typed FeaturePython)
  Dunit = g/cm3
  Dvalue = 1.06
  Group = -> [C_element086,H_element080]
  conduct = 2
  density = 1
  expand = 3
  formula = G4_POLYSTYRENE
  name = G4_POLYSTYRENE
  specific = 4
FEATURE [App::DocumentObjectGroupPython] C_element087  label="C_element : 045"  # scripted group (container) (typed FeaturePython)
  n = 2
  ref = C_element
FEATURE [App::DocumentObjectGroupPython] F_element014  label="F_element : 4"  # scripted group (container) (typed FeaturePython)
  n = 4
  ref = F_element
FEATURE [App::DocumentObjectGroupPython] G4_TEFLON  # scripted group (container) (typed FeaturePython)
  Dunit = g/cm3
  Dvalue = 2.2
  Group = -> [C_element087,F_element014]
  conduct = 2
  density = 1
  expand = 3
  formula = G4_TEFLON
  name = G4_TEFLON
  specific = 4
FEATURE [App::DocumentObjectGroupPython] C_element088  label="C_element : 046"  # scripted group (container) (typed FeaturePython)
  n = 2
  ref = C_element
FEATURE [App::DocumentObjectGroupPython] F_element015  label="F_element : 006"  # scripted group (container) (typed FeaturePython)
  n = 3
  ref = F_element
FEATURE [App::DocumentObjectGroupPython] Cl_element018  label="Cl_element : 008"  # scripted group (container) (typed FeaturePython)
  n = 1
  ref = Cl_element
FEATURE [App::DocumentObjectGroupPython] G4_POLYTRIFLUOROCHLOROETHYLENE  # scripted group (container) (typed FeaturePython)
  Dunit = g/cm3
  Dvalue = 2.1
  Group = -> [C_element088,F_element015,Cl_element018]
  conduct = 2
  density = 1
  expand = 3
  formula = G4_POLYTRIFLUOROCHLOROETHYLENE
  name = G4_POLYTRIFLUOROCHLOROETHYLENE
  specific = 4
FEATURE [App::DocumentObjectGroupPython] C_element089  label="C_element : 047"  # scripted group (container) (typed FeaturePython)
  n = 4
  ref = C_element
FEATURE [App::DocumentObjectGroupPython] H_element081  label="H_element : 043"  # scripted group (container) (typed FeaturePython)
  n = 6
  ref = H_element
FEATURE [App::DocumentObjectGroupPython] O_element081  label="O_element : 042"  # scripted group (container) (typed FeaturePython)
  n = 2
  ref = O_element
FEATURE [App::DocumentObjectGroupPython] G4_POLYVINYL_ACETATE  # scripted group (container) (typed FeaturePython)
  Dunit = g/cm3
  Dvalue = 1.19
  Group = -> [C_element089,H_element081,O_element081]
  conduct = 2
  density = 1
  expand = 3
  formula = G4_POLYVINYL_ACETATE
  name = G4_POLYVINYL_ACETATE
  specific = 4
FEATURE [App::DocumentObjectGroupPython] C_element090  label="C_element : 048"  # scripted group (container) (typed FeaturePython)
  n = 2
  ref = C_element
FEATURE [App::DocumentObjectGroupPython] H_element082  label="H_element : 044"  # scripted group (container) (typed FeaturePython)
  n = 4
  ref = H_element
FEATURE [App::DocumentObjectGroupPython] O_element082  label="O_element : 043"  # scripted group (container) (typed FeaturePython)
  n = 1
  ref = O_element
FEATURE [App::DocumentObjectGroupPython] G4_POLYVINYL_ALCOHOL  # scripted group (container) (typed FeaturePython)
  Dunit = g/cm3
  Dvalue = 1.3
  Group = -> [C_element090,H_element082,O_element082]
  conduct = 2
  density = 1
  expand = 3
  formula = G4_POLYVINYL_ALCOHOL
  name = G4_POLYVINYL_ALCOHOL
  specific = 4
FEATURE [App::DocumentObjectGroupPython] C_element091  label="C_element : 049"  # scripted group (container) (typed FeaturePython)
  n = 8
  ref = C_element
FEATURE [App::DocumentObjectGroupPython] H_element083  label="H_element : 045"  # scripted group (container) (typed FeaturePython)
  n = 14
  ref = H_element
FEATURE [App::DocumentObjectGroupPython] O_element083  label="O_element : 044"  # scripted group (container) (typed FeaturePython)
  n = 2
  ref = O_element
FEATURE [App::DocumentObjectGroupPython] G4_POLYVINYL_BUTYRAL  # scripted group (container) (typed FeaturePython)
  Dunit = g/cm3
  Dvalue = 1.12
  Group = -> [C_element091,H_element083,O_element083]
  conduct = 2
  density = 1
  expand = 3
  formula = G4_POLYVINYL_BUTYRAL
  name = G4_POLYVINYL_BUTYRAL
  specific = 4
FEATURE [App::DocumentObjectGroupPython] C_element092  label="C_element : 050"  # scripted group (container) (typed FeaturePython)
  n = 2
  ref = C_element
FEATURE [App::DocumentObjectGroupPython] H_element084  label="H_element : 046"  # scripted group (container) (typed FeaturePython)
  n = 3
  ref = H_element
FEATURE [App::DocumentObjectGroupPython] Cl_element019  label="Cl_element : 009"  # scripted group (container) (typed FeaturePython)
  n = 1
  ref = Cl_element
FEATURE [App::DocumentObjectGroupPython] G4_POLYVINYL_CHLORIDE  # scripted group (container) (typed FeaturePython)
  Dunit = g/cm3
  Dvalue = 1.3
  Group = -> [C_element092,H_element084,Cl_element019]
  conduct = 2
  density = 1
  expand = 3
  formula = G4_POLYVINYL_CHLORIDE
  name = G4_POLYVINYL_CHLORIDE
  specific = 4
FEATURE [App::DocumentObjectGroupPython] C_element093  label="C_element : 051"  # scripted group (container) (typed FeaturePython)
  n = 2
  ref = C_element
FEATURE [App::DocumentObjectGroupPython] H_element085  label="H_element : 047"  # scripted group (container) (typed FeaturePython)
  n = 2
  ref = H_element
FEATURE [App::DocumentObjectGroupPython] Cl_element020  label="Cl_element : 010"  # scripted group (container) (typed FeaturePython)
  n = 2
  ref = Cl_element
FEATURE [App::DocumentObjectGroupPython] G4_POLYVINYLIDENE_CHLORIDE  # scripted group (container) (typed FeaturePython)
  Dunit = g/cm3
  Dvalue = 1.7
  Group = -> [C_element093,H_element085,Cl_element020]
  conduct = 2
  density = 1
  expand = 3
  formula = G4_POLYVINYLIDENE_CHLORIDE
  name = G4_POLYVINYLIDENE_CHLORIDE
  specific = 4
FEATURE [App::DocumentObjectGroupPython] C_element094  label="C_element : 052"  # scripted group (container) (typed FeaturePython)
  n = 2
  ref = C_element
FEATURE [App::DocumentObjectGroupPython] H_element086  label="H_element : 048"  # scripted group (container) (typed FeaturePython)
  n = 2
  ref = H_element
FEATURE [App::DocumentObjectGroupPython] F_element016  label="F_element : 007"  # scripted group (container) (typed FeaturePython)
  n = 2
  ref = F_element
FEATURE [App::DocumentObjectGroupPython] G4_POLYVINYLIDENE_FLUORIDE  # scripted group (container) (typed FeaturePython)
  Dunit = g/cm3
  Dvalue = 1.76
  Group = -> [C_element094,H_element086,F_element016]
  conduct = 2
  density = 1
  expand = 3
  formula = G4_POLYVINYLIDENE_FLUORIDE
  name = G4_POLYVINYLIDENE_FLUORIDE
  specific = 4
FEATURE [App::DocumentObjectGroupPython] C_element095  label="C_element : 053"  # scripted group (container) (typed FeaturePython)
  n = 6
  ref = C_element
FEATURE [App::DocumentObjectGroupPython] H_element087  label="H_element : 9"  # scripted group (container) (typed FeaturePython)
  n = 9
  ref = H_element
FEATURE [App::DocumentObjectGroupPython] N_element037  label="N_element : 016"  # scripted group (container) (typed FeaturePython)
  n = 1
  ref = N_element
FEATURE [App::DocumentObjectGroupPython] O_element084  label="O_element : 045"  # scripted group (container) (typed FeaturePython)
  n = 1
  ref = O_element
FEATURE [App::DocumentObjectGroupPython] G4_POLYVINYL_PYRROLIDONE  # scripted group (container) (typed FeaturePython)
  Dunit = g/cm3
  Dvalue = 1.25
  Group = -> [C_element095,H_element087,N_element037,O_element084]
  conduct = 2
  density = 1
  expand = 3
  formula = G4_POLYVINYL_PYRROLIDONE
  name = G4_POLYVINYL_PYRROLIDONE
  specific = 4
FEATURE [App::DocumentObjectGroupPython] K_element008  label="K_element : 1"  # scripted group (container) (typed FeaturePython)
  n = 1
  ref = K_element
FEATURE [App::DocumentObjectGroupPython] I_element006  label="I_element : 003"  # scripted group (container) (typed FeaturePython)
  n = 1
  ref = I_element
FEATURE [App::DocumentObjectGroupPython] G4_POTASSIUM_IODIDE  # scripted group (container) (typed FeaturePython)
  Dunit = g/cm3
  Dvalue = 3.13
  Group = -> [K_element008,I_element006]
  conduct = 2
  density = 1
  expand = 3
  formula = G4_POTASSIUM_IODIDE
  name = G4_POTASSIUM_IODIDE
  specific = 4
FEATURE [App::DocumentObjectGroupPython] K_element009  label="K_element : 2"  # scripted group (container) (typed FeaturePython)
  n = 2
  ref = K_element
FEATURE [App::DocumentObjectGroupPython] O_element085  label="O_element : 046"  # scripted group (container) (typed FeaturePython)
  n = 1
  ref = O_element
FEATURE [App::DocumentObjectGroupPython] G4_POTASSIUM_OXIDE  # scripted group (container) (typed FeaturePython)
  Dunit = g/cm3
  Dvalue = 2.32
  Group = -> [K_element009,O_element085]
  conduct = 2
  density = 1
  expand = 3
  formula = G4_POTASSIUM_OXIDE
  name = G4_POTASSIUM_OXIDE
  specific = 4
FEATURE [App::DocumentObjectGroupPython] C_element096  label="C_element : 054"  # scripted group (container) (typed FeaturePython)
  n = 3
  ref = C_element
FEATURE [App::DocumentObjectGroupPython] H_element088  label="H_element : 049"  # scripted group (container) (typed FeaturePython)
  n = 8
  ref = H_element
FEATURE [App::DocumentObjectGroupPython] G4_PROPANE  # scripted group (container) (typed FeaturePython)
  Dunit = g/cm3
  Dvalue = 0.00187939
  Group = -> [C_element096,H_element088]
  conduct = 2
  density = 1
  expand = 3
  formula = G4_PROPANE
  name = G4_PROPANE
  specific = 4
FEATURE [App::DocumentObjectGroupPython] C_element097  label="C_element : 055"  # scripted group (container) (typed FeaturePython)
  n = 3
  ref = C_element
FEATURE [App::DocumentObjectGroupPython] H_element089  label="H_element : 050"  # scripted group (container) (typed FeaturePython)
  n = 8
  ref = H_element
FEATURE [App::DocumentObjectGroupPython] G4_lPROPANE  # scripted group (container) (typed FeaturePython)
  Dunit = g/cm3
  Dvalue = 0.43
  Group = -> [C_element097,H_element089]
  conduct = 2
  density = 1
  expand = 3
  formula = G4_lPROPANE
  name = G4_lPROPANE
  specific = 4
FEATURE [App::DocumentObjectGroupPython] C_element098  label="C_element : 056"  # scripted group (container) (typed FeaturePython)
  n = 3
  ref = C_element
FEATURE [App::DocumentObjectGroupPython] H_element090  label="H_element : 051"  # scripted group (container) (typed FeaturePython)
  n = 8
  ref = H_element
FEATURE [App::DocumentObjectGroupPython] O_element086  label="O_element : 047"  # scripted group (container) (typed FeaturePython)
  n = 1
  ref = O_element
FEATURE [App::DocumentObjectGroupPython] G4_N_PROPYL_ALCOHOL  label="G4_N-PROPYL_ALCOHOL"  # scripted group (container) (typed FeaturePython)
  Dunit = g/cm3
  Dvalue = 0.8035
  Group = -> [C_element098,H_element090,O_element086]
  conduct = 2
  density = 1
  expand = 3
  formula = G4_N-PROPYL_ALCOHOL
  name = G4_N-PROPYL_ALCOHOL
  specific = 4
FEATURE [App::DocumentObjectGroupPython] C_element099  label="C_element : 057"  # scripted group (container) (typed FeaturePython)
  n = 5
  ref = C_element
FEATURE [App::DocumentObjectGroupPython] H_element091  label="H_element : 052"  # scripted group (container) (typed FeaturePython)
  n = 5
  ref = H_element
FEATURE [App::DocumentObjectGroupPython] N_element038  label="N_element : 017"  # scripted group (container) (typed FeaturePython)
  n = 1
  ref = N_element
FEATURE [App::DocumentObjectGroupPython] G4_PYRIDINE  # scripted group (container) (typed FeaturePython)
  Dunit = g/cm3
  Dvalue = 0.9819
  Group = -> [C_element099,H_element091,N_element038]
  conduct = 2
  density = 1
  expand = 3
  formula = G4_PYRIDINE
  name = G4_PYRIDINE
  specific = 4
FEATURE [App::DocumentObjectGroupPython] H_element092  label="H_element : 0.144"  # scripted group (container) (typed FeaturePython)
  n = 0.143711
FEATURE [App::DocumentObjectGroupPython] C_element100  label="C_element : 0.856"  # scripted group (container) (typed FeaturePython)
  n = 0.856289
FEATURE [App::DocumentObjectGroupPython] G4_RUBBER_BUTYL  # scripted group (container) (typed FeaturePython)
  Dunit = g/cm3
  Dvalue = 0.92
  Group = -> [H_element092,C_element100]
  conduct = 2
  density = 1
  expand = 3
  formula = G4_RUBBER_BUTYL
  name = G4_RUBBER_BUTYL
  specific = 4
FEATURE [App::DocumentObjectGroupPython] H_element093  label="H_element : 0.118"  # scripted group (container) (typed FeaturePython)
  n = 0.118371
FEATURE [App::DocumentObjectGroupPython] C_element101  label="C_element : 0.882"  # scripted group (container) (typed FeaturePython)
  n = 0.881629
FEATURE [App::DocumentObjectGroupPython] G4_RUBBER_NATURAL  # scripted group (container) (typed FeaturePython)
  Dunit = g/cm3
  Dvalue = 0.92
  Group = -> [H_element093,C_element101]
  conduct = 2
  density = 1
  expand = 3
  formula = G4_RUBBER_NATURAL
  name = G4_RUBBER_NATURAL
  specific = 4
FEATURE [App::DocumentObjectGroupPython] H_element094  label="H_element : 0.145"  # scripted group (container) (typed FeaturePython)
  n = 0.05692
FEATURE [App::DocumentObjectGroupPython] C_element102  label="C_element : 0.543"  # scripted group (container) (typed FeaturePython)
  n = 0.542646
FEATURE [App::DocumentObjectGroupPython] Cl_element021  label="Cl_element : 0.400"  # scripted group (container) (typed FeaturePython)
  n = 0.400434
FEATURE [App::DocumentObjectGroupPython] G4_RUBBER_NEOPRENE  # scripted group (container) (typed FeaturePython)
  Dunit = g/cm3
  Dvalue = 1.23
  Group = -> [H_element094,C_element102,Cl_element021]
  conduct = 2
  density = 1
  expand = 3
  formula = G4_RUBBER_NEOPRENE
  name = G4_RUBBER_NEOPRENE
  specific = 4
FEATURE [App::DocumentObjectGroupPython] Si_element006  label="Si_element : 1"  # scripted group (container) (typed FeaturePython)
  n = 1
  ref = Si_element
FEATURE [App::DocumentObjectGroupPython] O_element087  label="O_element : 048"  # scripted group (container) (typed FeaturePython)
  n = 2
  ref = O_element
FEATURE [App::DocumentObjectGroupPython] G4_SILICON_DIOXIDE  # scripted group (container) (typed FeaturePython)
  Dunit = g/cm3
  Dvalue = 2.32
  Group = -> [Si_element006,O_element087]
  conduct = 2
  density = 1
  expand = 3
  formula = G4_SILICON_DIOXIDE
  name = G4_SILICON_DIOXIDE
  specific = 4
FEATURE [App::DocumentObjectGroupPython] Ag_element002  label="Ag_element : 1"  # scripted group (container) (typed FeaturePython)
  n = 1
  ref = Ag_element
FEATURE [App::DocumentObjectGroupPython] Br_element005  label="Br_element : 003"  # scripted group (container) (typed FeaturePython)
  n = 1
  ref = Br_element
FEATURE [App::DocumentObjectGroupPython] G4_SILVER_BROMIDE  # scripted group (container) (typed FeaturePython)
  Dunit = g/cm3
  Dvalue = 6.473
  Group = -> [Ag_element002,Br_element005]
  conduct = 2
  density = 1
  expand = 3
  formula = G4_SILVER_BROMIDE
  name = G4_SILVER_BROMIDE
  specific = 4
FEATURE [App::DocumentObjectGroupPython] Ag_element003  label="Ag_element : 002"  # scripted group (container) (typed FeaturePython)
  n = 1
  ref = Ag_element
FEATURE [App::DocumentObjectGroupPython] Cl_element022  label="Cl_element : 011"  # scripted group (container) (typed FeaturePython)
  n = 1
  ref = Cl_element
FEATURE [App::DocumentObjectGroupPython] G4_SILVER_CHLORIDE  # scripted group (container) (typed FeaturePython)
  Dunit = g/cm3
  Dvalue = 5.56
  Group = -> [Ag_element003,Cl_element022]
  conduct = 2
  density = 1
  expand = 3
  formula = G4_SILVER_CHLORIDE
  name = G4_SILVER_CHLORIDE
  specific = 4
FEATURE [App::DocumentObjectGroupPython] Br_element006  label="Br_element : 0.423"  # scripted group (container) (typed FeaturePython)
  n = 0.422895
FEATURE [App::DocumentObjectGroupPython] Ag_element004  label="Ag_element : 0.574"  # scripted group (container) (typed FeaturePython)
  n = 0.573748
FEATURE [App::DocumentObjectGroupPython] I_element007  label="I_element : 0.649"  # scripted group (container) (typed FeaturePython)
  n = 0.003357
FEATURE [App::DocumentObjectGroupPython] G4_SILVER_HALIDES  # scripted group (container) (typed FeaturePython)
  Dunit = g/cm3
  Dvalue = 6.47
  Group = -> [Br_element006,Ag_element004,I_element007]
  conduct = 2
  density = 1
  expand = 3
  formula = G4_SILVER_HALIDES
  name = G4_SILVER_HALIDES
  specific = 4
FEATURE [App::DocumentObjectGroupPython] Ag_element005  label="Ag_element : 003"  # scripted group (container) (typed FeaturePython)
  n = 1
  ref = Ag_element
FEATURE [App::DocumentObjectGroupPython] I_element008  label="I_element : 004"  # scripted group (container) (typed FeaturePython)
  n = 1
  ref = I_element
FEATURE [App::DocumentObjectGroupPython] G4_SILVER_IODIDE  # scripted group (container) (typed FeaturePython)
  Dunit = g/cm3
  Dvalue = 6.01
  Group = -> [Ag_element005,I_element008]
  conduct = 2
  density = 1
  expand = 3
  formula = G4_SILVER_IODIDE
  name = G4_SILVER_IODIDE
  specific = 4
FEATURE [App::DocumentObjectGroupPython] H_element095  label="H_element : 0.100"  # scripted group (container) (typed FeaturePython)
  n = 0.1
FEATURE [App::DocumentObjectGroupPython] C_element103  label="C_element : 0.204"  # scripted group (container) (typed FeaturePython)
  n = 0.204
FEATURE [App::DocumentObjectGroupPython] N_element039  label="N_element : 0.759"  # scripted group (container) (typed FeaturePython)
  n = 0.042
FEATURE [App::DocumentObjectGroupPython] O_element088  label="O_element : 0.645"  # scripted group (container) (typed FeaturePython)
  n = 0.645
FEATURE [App::DocumentObjectGroupPython] Na_element013  label="Na_element : 0.100"  # scripted group (container) (typed FeaturePython)
  n = 0.002
FEATURE [App::DocumentObjectGroupPython] P_element009  label="P_element : 0.107"  # scripted group (container) (typed FeaturePython)
  n = 0.001
FEATURE [App::DocumentObjectGroupPython] S_element020  label="S_element : 0.021"  # scripted group (container) (typed FeaturePython)
  n = 0.002
FEATURE [App::DocumentObjectGroupPython] Cl_element023  label="Cl_element : 0.590"  # scripted group (container) (typed FeaturePython)
  n = 0.003
FEATURE [App::DocumentObjectGroupPython] K_element010  label="K_element : 0.001"  # scripted group (container) (typed FeaturePython)
  n = 0.001
FEATURE [App::DocumentObjectGroupPython] G4_SKIN_ICRP  # scripted group (container) (typed FeaturePython)
  Dunit = g/cm3
  Dvalue = 1.09
  Group = -> [H_element095,C_element103,N_element039,O_element088,Na_element013,P_element009,S_element020,Cl_element023,K_element010]
  conduct = 2
  density = 1
  expand = 3
  formula = G4_SKIN_ICRP
  name = G4_SKIN_ICRP
  specific = 4
FEATURE [App::DocumentObjectGroupPython] Na_element014  label="Na_element : 2"  # scripted group (container) (typed FeaturePython)
  n = 2
  ref = Na_element
FEATURE [App::DocumentObjectGroupPython] C_element104  label="C_element : 058"  # scripted group (container) (typed FeaturePython)
  n = 1
  ref = C_element
FEATURE [App::DocumentObjectGroupPython] O_element089  label="O_element : 049"  # scripted group (container) (typed FeaturePython)
  n = 3
  ref = O_element
FEATURE [App::DocumentObjectGroupPython] G4_SODIUM_CARBONATE  # scripted group (container) (typed FeaturePython)
  Dunit = g/cm3
  Dvalue = 2.532
  Group = -> [Na_element014,C_element104,O_element089]
  conduct = 2
  density = 1
  expand = 3
  formula = G4_SODIUM_CARBONATE
  name = G4_SODIUM_CARBONATE
  specific = 4
FEATURE [App::DocumentObjectGroupPython] Na_element015  label="Na_element : 1"  # scripted group (container) (typed FeaturePython)
  n = 1
  ref = Na_element
FEATURE [App::DocumentObjectGroupPython] I_element009  label="I_element : 005"  # scripted group (container) (typed FeaturePython)
  n = 1
  ref = I_element
FEATURE [App::DocumentObjectGroupPython] G4_SODIUM_IODIDE  # scripted group (container) (typed FeaturePython)
  Dunit = g/cm3
  Dvalue = 3.667
  Group = -> [Na_element015,I_element009]
  conduct = 2
  density = 1
  expand = 3
  formula = G4_SODIUM_IODIDE
  name = G4_SODIUM_IODIDE
  specific = 4
FEATURE [App::DocumentObjectGroupPython] Na_element016  label="Na_element : 003"  # scripted group (container) (typed FeaturePython)
  n = 2
  ref = Na_element
FEATURE [App::DocumentObjectGroupPython] O_element090  label="O_element : 050"  # scripted group (container) (typed FeaturePython)
  n = 1
  ref = O_element
FEATURE [App::DocumentObjectGroupPython] G4_SODIUM_MONOXIDE  # scripted group (container) (typed FeaturePython)
  Dunit = g/cm3
  Dvalue = 2.27
  Group = -> [Na_element016,O_element090]
  conduct = 2
  density = 1
  expand = 3
  formula = G4_SODIUM_MONOXIDE
  name = G4_SODIUM_MONOXIDE
  specific = 4
FEATURE [App::DocumentObjectGroupPython] Na_element017  label="Na_element : 004"  # scripted group (container) (typed FeaturePython)
  n = 1
  ref = Na_element
FEATURE [App::DocumentObjectGroupPython] N_element040  label="N_element : 018"  # scripted group (container) (typed FeaturePython)
  n = 1
  ref = N_element
FEATURE [App::DocumentObjectGroupPython] O_element091  label="O_element : 051"  # scripted group (container) (typed FeaturePython)
  n = 3
  ref = O_element
FEATURE [App::DocumentObjectGroupPython] G4_SODIUM_NITRATE  # scripted group (container) (typed FeaturePython)
  Dunit = g/cm3
  Dvalue = 2.261
  Group = -> [Na_element017,N_element040,O_element091]
  conduct = 2
  density = 1
  expand = 3
  formula = G4_SODIUM_NITRATE
  name = G4_SODIUM_NITRATE
  specific = 4
FEATURE [App::DocumentObjectGroupPython] C_element105  label="C_element : 059"  # scripted group (container) (typed FeaturePython)
  n = 14
  ref = C_element
FEATURE [App::DocumentObjectGroupPython] H_element096  label="H_element : 053"  # scripted group (container) (typed FeaturePython)
  n = 12
  ref = H_element
FEATURE [App::DocumentObjectGroupPython] G4_STILBENE  # scripted group (container) (typed FeaturePython)
  Dunit = g/cm3
  Dvalue = 0.9707
  Group = -> [C_element105,H_element096]
  conduct = 2
  density = 1
  expand = 3
  formula = G4_STILBENE
  name = G4_STILBENE
  specific = 4
FEATURE [App::DocumentObjectGroupPython] C_element106  label="C_element : 12"  # scripted group (container) (typed FeaturePython)
  n = 12
  ref = C_element
FEATURE [App::DocumentObjectGroupPython] H_element097  label="H_element : 22"  # scripted group (container) (typed FeaturePython)
  n = 22
  ref = H_element
FEATURE [App::DocumentObjectGroupPython] O_element092  label="O_element : 11"  # scripted group (container) (typed FeaturePython)
  n = 11
  ref = O_element
FEATURE [App::DocumentObjectGroupPython] G4_SUCROSE  # scripted group (container) (typed FeaturePython)
  Dunit = g/cm3
  Dvalue = 1.5805
  Group = -> [C_element106,H_element097,O_element092]
  conduct = 2
  density = 1
  expand = 3
  formula = G4_SUCROSE
  name = G4_SUCROSE
  specific = 4
FEATURE [App::DocumentObjectGroupPython] C_element107  label="C_element : 18"  # scripted group (container) (typed FeaturePython)
  n = 18
  ref = C_element
FEATURE [App::DocumentObjectGroupPython] H_element098  label="H_element : 054"  # scripted group (container) (typed FeaturePython)
  n = 14
  ref = H_element
FEATURE [App::DocumentObjectGroupPython] G4_TERPHENYL  # scripted group (container) (typed FeaturePython)
  Dunit = g/cm3
  Dvalue = 1.24
  Group = -> [C_element107,H_element098]
  conduct = 2
  density = 1
  expand = 3
  formula = G4_TERPHENYL
  name = G4_TERPHENYL
  specific = 4
FEATURE [App::DocumentObjectGroupPython] H_element099  label="H_element : 0.146"  # scripted group (container) (typed FeaturePython)
  n = 0.106
FEATURE [App::DocumentObjectGroupPython] C_element108  label="C_element : 0.883"  # scripted group (container) (typed FeaturePython)
  n = 0.099
FEATURE [App::DocumentObjectGroupPython] N_element041  label="N_element : 0.020"  # scripted group (container) (typed FeaturePython)
  n = 0.02
FEATURE [App::DocumentObjectGroupPython] O_element093  label="O_element : 0.766"  # scripted group (container) (typed FeaturePython)
  n = 0.766
FEATURE [App::DocumentObjectGroupPython] Na_element018  label="Na_element : 0.101"  # scripted group (container) (typed FeaturePython)
  n = 0.002
FEATURE [App::DocumentObjectGroupPython] P_element010  label="P_element : 0.108"  # scripted group (container) (typed FeaturePython)
  n = 0.001
FEATURE [App::DocumentObjectGroupPython] S_element021  label="S_element : 0.022"  # scripted group (container) (typed FeaturePython)
  n = 0.002
FEATURE [App::DocumentObjectGroupPython] Cl_element024  label="Cl_element : 0.002"  # scripted group (container) (typed FeaturePython)
  n = 0.002
FEATURE [App::DocumentObjectGroupPython] K_element011  label="K_element : 0.017"  # scripted group (container) (typed FeaturePython)
  n = 0.002
FEATURE [App::DocumentObjectGroupPython] G4_TESTIS_ICRP  # scripted group (container) (typed FeaturePython)
  Dunit = g/cm3
  Dvalue = 1.04
  Group = -> [H_element099,C_element108,N_element041,O_element093,Na_element018,P_element010,S_element021,Cl_element024,K_element011]
  conduct = 2
  density = 1
  expand = 3
  formula = G4_TESTIS_ICRP
  name = G4_TESTIS_ICRP
  specific = 4
FEATURE [App::DocumentObjectGroupPython] C_element109  label="C_element : 060"  # scripted group (container) (typed FeaturePython)
  n = 2
  ref = C_element
FEATURE [App::DocumentObjectGroupPython] Cl_element025  label="Cl_element : 012"  # scripted group (container) (typed FeaturePython)
  n = 4
  ref = Cl_element
FEATURE [App::DocumentObjectGroupPython] G4_TETRACHLOROETHYLENE  # scripted group (container) (typed FeaturePython)
  Dunit = g/cm3
  Dvalue = 1.625
  Group = -> [C_element109,Cl_element025]
  conduct = 2
  density = 1
  expand = 3
  formula = G4_TETRACHLOROETHYLENE
  name = G4_TETRACHLOROETHYLENE
  specific = 4
FEATURE [App::DocumentObjectGroupPython] Tl_element001  label="Tl_element : 1"  # scripted group (container) (typed FeaturePython)
  n = 1
  ref = Tl_element
FEATURE [App::DocumentObjectGroupPython] Cl_element026  label="Cl_element : 013"  # scripted group (container) (typed FeaturePython)
  n = 1
  ref = Cl_element
FEATURE [App::DocumentObjectGroupPython] G4_THALLIUM_CHLORIDE  # scripted group (container) (typed FeaturePython)
  Dunit = g/cm3
  Dvalue = 7.004
  Group = -> [Tl_element001,Cl_element026]
  conduct = 2
  density = 1
  expand = 3
  formula = G4_THALLIUM_CHLORIDE
  name = G4_THALLIUM_CHLORIDE
  specific = 4
FEATURE [App::DocumentObjectGroupPython] H_element100  label="H_element : 0.147"  # scripted group (container) (typed FeaturePython)
  n = 0.105
FEATURE [App::DocumentObjectGroupPython] C_element110  label="C_element : 0.256"  # scripted group (container) (typed FeaturePython)
  n = 0.256
FEATURE [App::DocumentObjectGroupPython] N_element042  label="N_element : 0.760"  # scripted group (container) (typed FeaturePython)
  n = 0.027
FEATURE [App::DocumentObjectGroupPython] O_element094  label="O_element : 0.602"  # scripted group (container) (typed FeaturePython)
  n = 0.602
FEATURE [App::DocumentObjectGroupPython] Na_element019  label="Na_element : 0.102"  # scripted group (container) (typed FeaturePython)
  n = 0.001
FEATURE [App::DocumentObjectGroupPython] P_element011  label="P_element : 0.109"  # scripted group (container) (typed FeaturePython)
  n = 0.002
FEATURE [App::DocumentObjectGroupPython] S_element022  label="S_element : 0.023"  # scripted group (container) (typed FeaturePython)
  n = 0.003
FEATURE [App::DocumentObjectGroupPython] Cl_element027  label="Cl_element : 0.591"  # scripted group (container) (typed FeaturePython)
  n = 0.002
FEATURE [App::DocumentObjectGroupPython] K_element012  label="K_element : 0.018"  # scripted group (container) (typed FeaturePython)
  n = 0.002
FEATURE [App::DocumentObjectGroupPython] G4_TISSUE_SOFT_ICRP  # scripted group (container) (typed FeaturePython)
  Dunit = g/cm3
  Dvalue = 1.03
  Group = -> [H_element100,C_element110,N_element042,O_element094,Na_element019,P_element011,S_element022,Cl_element027,K_element012]
  conduct = 2
  density = 1
  expand = 3
  formula = G4_TISSUE_SOFT_ICRP
  name = G4_TISSUE_SOFT_ICRP
  specific = 4
FEATURE [App::DocumentObjectGroupPython] H_element101  label="H_element : 0.148"  # scripted group (container) (typed FeaturePython)
  n = 0.101
FEATURE [App::DocumentObjectGroupPython] C_element111  label="C_element : 0.111"  # scripted group (container) (typed FeaturePython)
  n = 0.111
FEATURE [App::DocumentObjectGroupPython] N_element043  label="N_element : 0.026"  # scripted group (container) (typed FeaturePython)
  n = 0.026
FEATURE [App::DocumentObjectGroupPython] O_element095  label="O_element : 0.762"  # scripted group (container) (typed FeaturePython)
  n = 0.762
FEATURE [App::DocumentObjectGroupPython] G4_TISSUE_SOFT_ICRU_4  label="G4_TISSUE_SOFT_ICRU-4"  # scripted group (container) (typed FeaturePython)
  Dunit = g/cm3
  Dvalue = 1
  Group = -> [H_element101,C_element111,N_element043,O_element095]
  conduct = 2
  density = 1
  expand = 3
  formula = G4_TISSUE_SOFT_ICRU-4
  name = G4_TISSUE_SOFT_ICRU-4
  specific = 4
FEATURE [App::DocumentObjectGroupPython] H_element102  label="H_element : 0.149"  # scripted group (container) (typed FeaturePython)
  n = 0.101869
FEATURE [App::DocumentObjectGroupPython] C_element112  label="C_element : 0.456"  # scripted group (container) (typed FeaturePython)
  n = 0.456179
FEATURE [App::DocumentObjectGroupPython] N_element044  label="N_element : 0.761"  # scripted group (container) (typed FeaturePython)
  n = 0.035172
FEATURE [App::DocumentObjectGroupPython] O_element096  label="O_element : 0.407"  # scripted group (container) (typed FeaturePython)
  n = 0.40678
FEATURE [App::DocumentObjectGroupPython] G4_TISSUE_METHANE  label="G4_TISSUE-METHANE"  # scripted group (container) (typed FeaturePython)
  Dunit = g/cm3
  Dvalue = 0.00106409
  Group = -> [H_element102,C_element112,N_element044,O_element096]
  conduct = 2
  density = 1
  expand = 3
  formula = G4_TISSUE-METHANE
  name = G4_TISSUE-METHANE
  specific = 4
FEATURE [App::DocumentObjectGroupPython] H_element103  label="H_element : 0.103"  # scripted group (container) (typed FeaturePython)
  n = 0.102672
FEATURE [App::DocumentObjectGroupPython] C_element113  label="C_element : 0.569"  # scripted group (container) (typed FeaturePython)
  n = 0.56894
FEATURE [App::DocumentObjectGroupPython] N_element045  label="N_element : 0.762"  # scripted group (container) (typed FeaturePython)
  n = 0.035022
FEATURE [App::DocumentObjectGroupPython] O_element097  label="O_element : 0.293"  # scripted group (container) (typed FeaturePython)
  n = 0.293366
FEATURE [App::DocumentObjectGroupPython] G4_TISSUE_PROPANE  label="G4_TISSUE-PROPANE"  # scripted group (container) (typed FeaturePython)
  Dunit = g/cm3
  Dvalue = 0.00182628
  Group = -> [H_element103,C_element113,N_element045,O_element097]
  conduct = 2
  density = 1
  expand = 3
  formula = G4_TISSUE-PROPANE
  name = G4_TISSUE-PROPANE
  specific = 4
FEATURE [App::DocumentObjectGroupPython] Ti_element003  label="Ti_element : 1"  # scripted group (container) (typed FeaturePython)
  n = 1
  ref = Ti_element
FEATURE [App::DocumentObjectGroupPython] O_element098  label="O_element : 052"  # scripted group (container) (typed FeaturePython)
  n = 2
  ref = O_element
FEATURE [App::DocumentObjectGroupPython] G4_TITANIUM_DIOXIDE  # scripted group (container) (typed FeaturePython)
  Dunit = g/cm3
  Dvalue = 4.26
  Group = -> [Ti_element003,O_element098]
  conduct = 2
  density = 1
  expand = 3
  formula = G4_TITANIUM_DIOXIDE
  name = G4_TITANIUM_DIOXIDE
  specific = 4
FEATURE [App::DocumentObjectGroupPython] C_element114  label="C_element : 061"  # scripted group (container) (typed FeaturePython)
  n = 7
  ref = C_element
FEATURE [App::DocumentObjectGroupPython] H_element104  label="H_element : 055"  # scripted group (container) (typed FeaturePython)
  n = 8
  ref = H_element
FEATURE [App::DocumentObjectGroupPython] G4_TOLUENE  # scripted group (container) (typed FeaturePython)
  Dunit = g/cm3
  Dvalue = 0.8669
  Group = -> [C_element114,H_element104]
  conduct = 2
  density = 1
  expand = 3
  formula = G4_TOLUENE
  name = G4_TOLUENE
  specific = 4
FEATURE [App::DocumentObjectGroupPython] C_element115  label="C_element : 062"  # scripted group (container) (typed FeaturePython)
  n = 2
  ref = C_element
FEATURE [App::DocumentObjectGroupPython] H_element105  label="H_element : 056"  # scripted group (container) (typed FeaturePython)
  n = 1
  ref = H_element
FEATURE [App::DocumentObjectGroupPython] Cl_element028  label="Cl_element : 014"  # scripted group (container) (typed FeaturePython)
  n = 3
  ref = Cl_element
FEATURE [App::DocumentObjectGroupPython] G4_TRICHLOROETHYLENE  # scripted group (container) (typed FeaturePython)
  Dunit = g/cm3
  Dvalue = 1.46
  Group = -> [C_element115,H_element105,Cl_element028]
  conduct = 2
  density = 1
  expand = 3
  formula = G4_TRICHLOROETHYLENE
  name = G4_TRICHLOROETHYLENE
  specific = 4
FEATURE [App::DocumentObjectGroupPython] C_element116  label="C_element : 063"  # scripted group (container) (typed FeaturePython)
  n = 6
  ref = C_element
FEATURE [App::DocumentObjectGroupPython] H_element106  label="H_element : 15"  # scripted group (container) (typed FeaturePython)
  n = 15
  ref = H_element
FEATURE [App::DocumentObjectGroupPython] O_element099  label="O_element : 053"  # scripted group (container) (typed FeaturePython)
  n = 4
  ref = O_element
FEATURE [App::DocumentObjectGroupPython] P_element012  label="P_element : 1"  # scripted group (container) (typed FeaturePython)
  n = 1
  ref = P_element
FEATURE [App::DocumentObjectGroupPython] G4_TRIETHYL_PHOSPHATE  # scripted group (container) (typed FeaturePython)
  Dunit = g/cm3
  Dvalue = 1.07
  Group = -> [C_element116,H_element106,O_element099,P_element012]
  conduct = 2
  density = 1
  expand = 3
  formula = G4_TRIETHYL_PHOSPHATE
  name = G4_TRIETHYL_PHOSPHATE
  specific = 4
FEATURE [App::DocumentObjectGroupPython] W_element003  label="W_element : 003"  # scripted group (container) (typed FeaturePython)
  n = 1
  ref = W_element
FEATURE [App::DocumentObjectGroupPython] F_element017  label="F_element : 6"  # scripted group (container) (typed FeaturePython)
  n = 6
  ref = F_element
FEATURE [App::DocumentObjectGroupPython] G4_TUNGSTEN_HEXAFLUORIDE  # scripted group (container) (typed FeaturePython)
  Dunit = g/cm3
  Dvalue = 2.4
  Group = -> [W_element003,F_element017]
  conduct = 2
  density = 1
  expand = 3
  formula = G4_TUNGSTEN_HEXAFLUORIDE
  name = G4_TUNGSTEN_HEXAFLUORIDE
  specific = 4
FEATURE [App::DocumentObjectGroupPython] U_element001  label="U_element : 1"  # scripted group (container) (typed FeaturePython)
  n = 1
  ref = U_element
FEATURE [App::DocumentObjectGroupPython] C_element117  label="C_element : 064"  # scripted group (container) (typed FeaturePython)
  n = 2
  ref = C_element
FEATURE [App::DocumentObjectGroupPython] G4_URANIUM_DICARBIDE  # scripted group (container) (typed FeaturePython)
  Dunit = g/cm3
  Dvalue = 11.28
  Group = -> [U_element001,C_element117]
  conduct = 2
  density = 1
  expand = 3
  formula = G4_URANIUM_DICARBIDE
  name = G4_URANIUM_DICARBIDE
  specific = 4
FEATURE [App::DocumentObjectGroupPython] U_element002  label="U_element : 002"  # scripted group (container) (typed FeaturePython)
  n = 1
  ref = U_element
FEATURE [App::DocumentObjectGroupPython] C_element118  label="C_element : 065"  # scripted group (container) (typed FeaturePython)
  n = 1
  ref = C_element
FEATURE [App::DocumentObjectGroupPython] G4_URANIUM_MONOCARBIDE  # scripted group (container) (typed FeaturePython)
  Dunit = g/cm3
  Dvalue = 13.63
  Group = -> [U_element002,C_element118]
  conduct = 2
  density = 1
  expand = 3
  formula = G4_URANIUM_MONOCARBIDE
  name = G4_URANIUM_MONOCARBIDE
  specific = 4
FEATURE [App::DocumentObjectGroupPython] U_element003  label="U_element : 003"  # scripted group (container) (typed FeaturePython)
  n = 1
  ref = U_element
FEATURE [App::DocumentObjectGroupPython] O_element100  label="O_element : 054"  # scripted group (container) (typed FeaturePython)
  n = 2
  ref = O_element
FEATURE [App::DocumentObjectGroupPython] G4_URANIUM_OXIDE  # scripted group (container) (typed FeaturePython)
  Dunit = g/cm3
  Dvalue = 10.96
  Group = -> [U_element003,O_element100]
  conduct = 2
  density = 1
  expand = 3
  formula = G4_URANIUM_OXIDE
  name = G4_URANIUM_OXIDE
  specific = 4
FEATURE [App::DocumentObjectGroupPython] C_element119  label="C_element : 066"  # scripted group (container) (typed FeaturePython)
  n = 1
  ref = C_element
FEATURE [App::DocumentObjectGroupPython] H_element107  label="H_element : 057"  # scripted group (container) (typed FeaturePython)
  n = 4
  ref = H_element
FEATURE [App::DocumentObjectGroupPython] N_element046  label="N_element : 019"  # scripted group (container) (typed FeaturePython)
  n = 2
  ref = N_element
FEATURE [App::DocumentObjectGroupPython] O_element101  label="O_element : 055"  # scripted group (container) (typed FeaturePython)
  n = 1
  ref = O_element
FEATURE [App::DocumentObjectGroupPython] G4_UREA  # scripted group (container) (typed FeaturePython)
  Dunit = g/cm3
  Dvalue = 1.323
  Group = -> [C_element119,H_element107,N_element046,O_element101]
  conduct = 2
  density = 1
  expand = 3
  formula = G4_UREA
  name = G4_UREA
  specific = 4
FEATURE [App::DocumentObjectGroupPython] C_element120  label="C_element : 067"  # scripted group (container) (typed FeaturePython)
  n = 5
  ref = C_element
FEATURE [App::DocumentObjectGroupPython] H_element108  label="H_element : 058"  # scripted group (container) (typed FeaturePython)
  n = 11
  ref = H_element
FEATURE [App::DocumentObjectGroupPython] N_element047  label="N_element : 020"  # scripted group (container) (typed FeaturePython)
  n = 1
  ref = N_element
FEATURE [App::DocumentObjectGroupPython] O_element102  label="O_element : 056"  # scripted group (container) (typed FeaturePython)
  n = 2
  ref = O_element
FEATURE [App::DocumentObjectGroupPython] G4_VALINE  # scripted group (container) (typed FeaturePython)
  Dunit = g/cm3
  Dvalue = 1.23
  Group = -> [C_element120,H_element108,N_element047,O_element102]
  conduct = 2
  density = 1
  expand = 3
  formula = G4_VALINE
  name = G4_VALINE
  specific = 4
FEATURE [App::DocumentObjectGroupPython] H_element109  label="H_element : 0.009"  # scripted group (container) (typed FeaturePython)
  n = 0.009417
FEATURE [App::DocumentObjectGroupPython] C_element121  label="C_element : 0.281"  # scripted group (container) (typed FeaturePython)
  n = 0.280555
FEATURE [App::DocumentObjectGroupPython] F_element018  label="F_element : 0.710"  # scripted group (container) (typed FeaturePython)
  n = 0.710028
FEATURE [App::DocumentObjectGroupPython] G4_VITON  # scripted group (container) (typed FeaturePython)
  Dunit = g/cm3
  Dvalue = 1.8
  Group = -> [H_element109,C_element121,F_element018]
  conduct = 2
  density = 1
  expand = 3
  formula = G4_VITON
  name = G4_VITON
  specific = 4
FEATURE [App::DocumentObjectGroupPython] H_element110  label="H_element : 059"  # scripted group (container) (typed FeaturePython)
  n = 2
  ref = H_element
FEATURE [App::DocumentObjectGroupPython] O_element103  label="O_element : 057"  # scripted group (container) (typed FeaturePython)
  n = 1
  ref = O_element
FEATURE [App::DocumentObjectGroupPython] G4_WATER  # scripted group (container) (typed FeaturePython)
  Dunit = g/cm3
  Dvalue = 1
  Group = -> [H_element110,O_element103]
  conduct = 2
  density = 1
  expand = 3
  formula = G4_WATER
  name = G4_WATER
  specific = 4
FEATURE [App::DocumentObjectGroupPython] H_element111  label="H_element : 060"  # scripted group (container) (typed FeaturePython)
  n = 2
  ref = H_element
FEATURE [App::DocumentObjectGroupPython] O_element104  label="O_element : 058"  # scripted group (container) (typed FeaturePython)
  n = 1
  ref = O_element
FEATURE [App::DocumentObjectGroupPython] G4_WATER_VAPOR  # scripted group (container) (typed FeaturePython)
  Dunit = g/cm3
  Dvalue = 0.000756182
  Group = -> [H_element111,O_element104]
  conduct = 2
  density = 1
  expand = 3
  formula = G4_WATER_VAPOR
  name = G4_WATER_VAPOR
  specific = 4
FEATURE [App::DocumentObjectGroupPython] C_element122  label="C_element : 068"  # scripted group (container) (typed FeaturePython)
  n = 8
  ref = C_element
FEATURE [App::DocumentObjectGroupPython] H_element112  label="H_element : 061"  # scripted group (container) (typed FeaturePython)
  n = 10
  ref = H_element
FEATURE [App::DocumentObjectGroupPython] G4_XYLENE  # scripted group (container) (typed FeaturePython)
  Dunit = g/cm3
  Dvalue = 0.87
  Group = -> [C_element122,H_element112]
  conduct = 2
  density = 1
  expand = 3
  formula = G4_XYLENE
  name = G4_XYLENE
  specific = 4
FEATURE [App::DocumentObjectGroupPython] C_element123  label="C_element : 069"  # scripted group (container) (typed FeaturePython)
  n = 1
  ref = C_element
FEATURE [App::DocumentObjectGroupPython] G4_GRAPHITE  # scripted group (container) (typed FeaturePython)
  Dunit = g/cm3
  Dvalue = 2.21
  Group = -> [C_element123]
  conduct = 2
  density = 1
  expand = 3
  formula = G4_GRAPHITE
  name = G4_GRAPHITE
  specific = 4
FEATURE [App::DocumentObjectGroupPython] NIST  # scripted group (container) (typed FeaturePython)
  Group = -> [G4_A_150_TISSUE,G4_ACETONE,G4_ACETYLENE,G4_ADENINE,G4_ADIPOSE_TISSUE_ICRP,G4_AIR,G4_ALANINE,G4_ALUMINUM_OXIDE,G4_AMBER,G4_AMMONIA,G4_ANILINE,G4_ANTHRACENE,G4_B_100_BONE,G4_BAKELITE,G4_BARIUM_FLUORIDE,G4_BARIUM_SULFATE,G4_BENZENE,G4_BERYLLIUM_OXIDE,G4_BGO,G4_BLOOD_ICRP,G4_BONE_COMPACT_ICRU,G4_BONE_CORTICAL_ICRP,G4_BORON_CARBIDE,G4_BORON_OXIDE,G4_BRAIN_ICRP,G4_BUTANE,G4_N_BUTYL_ALCOHOL,G4_C_552,+152 more]
FEATURE [App::DocumentObjectGroupPython] H_element113  label="H_element : 062"  # scripted group (container) (typed FeaturePython)
  n = 1
  ref = H_element
FEATURE [App::DocumentObjectGroupPython] G4_H  # scripted group (container) (typed FeaturePython)
  Dunit = g/cm3
  Dvalue = 8.3748e-05
  Group = -> [H_element113]
  conduct = 2
  density = 1
  expand = 3
  formula = H
  name = G4_H
  specific = 4
FEATURE [App::DocumentObjectGroupPython] He_element001  label="He_element : 1"  # scripted group (container) (typed FeaturePython)
  n = 1
  ref = He_element
FEATURE [App::DocumentObjectGroupPython] G4_He  # scripted group (container) (typed FeaturePython)
  Dunit = g/cm3
  Dvalue = 0.000166322
  Group = -> [He_element001]
  conduct = 2
  density = 1
  expand = 3
  formula = He
  name = G4_He
  specific = 4
FEATURE [App::DocumentObjectGroupPython] Li_element008  label="Li_element : 008"  # scripted group (container) (typed FeaturePython)
  n = 1
  ref = Li_element
FEATURE [App::DocumentObjectGroupPython] G4_Li  # scripted group (container) (typed FeaturePython)
  Dunit = g/cm3
  Dvalue = 0.534
  Group = -> [Li_element008]
  conduct = 2
  density = 1
  expand = 3
  formula = Li
  name = G4_Li
  specific = 4
FEATURE [App::DocumentObjectGroupPython] Be_element002  label="Be_element : 002"  # scripted group (container) (typed FeaturePython)
  n = 1
  ref = Be_element
FEATURE [App::DocumentObjectGroupPython] G4_Be  # scripted group (container) (typed FeaturePython)
  Dunit = g/cm3
  Dvalue = 1.848
  Group = -> [Be_element002]
  conduct = 2
  density = 1
  expand = 3
  formula = Be
  name = G4_Be
  specific = 4
FEATURE [App::DocumentObjectGroupPython] B_element007  label="B_element : 007"  # scripted group (container) (typed FeaturePython)
  n = 1
  ref = B_element
FEATURE [App::DocumentObjectGroupPython] G4_B  # scripted group (container) (typed FeaturePython)
  Dunit = g/cm3
  Dvalue = 2.37
  Group = -> [B_element007]
  conduct = 2
  density = 1
  expand = 3
  formula = B
  name = G4_B
  specific = 4
FEATURE [App::DocumentObjectGroupPython] C_element124  label="C_element : 070"  # scripted group (container) (typed FeaturePython)
  n = 1
  ref = C_element
FEATURE [App::DocumentObjectGroupPython] G4_C  # scripted group (container) (typed FeaturePython)
  Dunit = g/cm3
  Dvalue = 2
  Group = -> [C_element124]
  conduct = 2
  density = 1
  expand = 3
  formula = C
  name = G4_C
  specific = 4
FEATURE [App::DocumentObjectGroupPython] N_element048  label="N_element : 021"  # scripted group (container) (typed FeaturePython)
  n = 1
  ref = N_element
FEATURE [App::DocumentObjectGroupPython] G4_N  # scripted group (container) (typed FeaturePython)
  Dunit = g/cm3
  Dvalue = 0.0011652
  Group = -> [N_element048]
  conduct = 2
  density = 1
  expand = 3
  formula = N
  name = G4_N
  specific = 4
FEATURE [App::DocumentObjectGroupPython] O_element105  label="O_element : 059"  # scripted group (container) (typed FeaturePython)
  n = 1
  ref = O_element
FEATURE [App::DocumentObjectGroupPython] G4_O  # scripted group (container) (typed FeaturePython)
  Dunit = g/cm3
  Dvalue = 0.00133151
  Group = -> [O_element105]
  conduct = 2
  density = 1
  expand = 3
  formula = O
  name = G4_O
  specific = 4
FEATURE [App::DocumentObjectGroupPython] F_element019  label="F_element : 008"  # scripted group (container) (typed FeaturePython)
  n = 1
  ref = F_element
FEATURE [App::DocumentObjectGroupPython] G4_F  # scripted group (container) (typed FeaturePython)
  Dunit = g/cm3
  Dvalue = 0.00158029
  Group = -> [F_element019]
  conduct = 2
  density = 1
  expand = 3
  formula = F
  name = G4_F
  specific = 4
FEATURE [App::DocumentObjectGroupPython] Ne_element001  label="Ne_element : 1"  # scripted group (container) (typed FeaturePython)
  n = 1
  ref = Ne_element
FEATURE [App::DocumentObjectGroupPython] G4_Ne  # scripted group (container) (typed FeaturePython)
  Dunit = g/cm3
  Dvalue = 0.000838505
  Group = -> [Ne_element001]
  conduct = 2
  density = 1
  expand = 3
  formula = Ne
  name = G4_Ne
  specific = 4
FEATURE [App::DocumentObjectGroupPython] Na_element020  label="Na_element : 005"  # scripted group (container) (typed FeaturePython)
  n = 1
  ref = Na_element
FEATURE [App::DocumentObjectGroupPython] G4_Na  # scripted group (container) (typed FeaturePython)
  Dunit = g/cm3
  Dvalue = 0.971
  Group = -> [Na_element020]
  conduct = 2
  density = 1
  expand = 3
  formula = Na
  name = G4_Na
  specific = 4
FEATURE [App::DocumentObjectGroupPython] Mg_element011  label="Mg_element : 005"  # scripted group (container) (typed FeaturePython)
  n = 1
  ref = Mg_element
FEATURE [App::DocumentObjectGroupPython] G4_Mg  # scripted group (container) (typed FeaturePython)
  Dunit = g/cm3
  Dvalue = 1.74
  Group = -> [Mg_element011]
  conduct = 2
  density = 1
  expand = 3
  formula = Mg
  name = G4_Mg
  specific = 4
FEATURE [App::DocumentObjectGroupPython] Al_element004  label="Al_element : 1"  # scripted group (container) (typed FeaturePython)
  n = 1
  ref = Al_element
FEATURE [App::DocumentObjectGroupPython] G4_Al  # scripted group (container) (typed FeaturePython)
  Dunit = g/cm3
  Dvalue = 2.699
  Group = -> [Al_element004]
  conduct = 2
  density = 1
  expand = 3
  formula = Al
  name = G4_Al
  specific = 4
FEATURE [App::DocumentObjectGroupPython] Si_element007  label="Si_element : 002"  # scripted group (container) (typed FeaturePython)
  n = 1
  ref = Si_element
FEATURE [App::DocumentObjectGroupPython] G4_Si  # scripted group (container) (typed FeaturePython)
  Dunit = g/cm3
  Dvalue = 2.33
  Group = -> [Si_element007]
  conduct = 2
  density = 1
  expand = 3
  formula = Si
  name = G4_Si
  specific = 4
FEATURE [App::DocumentObjectGroupPython] P_element013  label="P_element : 002"  # scripted group (container) (typed FeaturePython)
  n = 1
  ref = P_element
FEATURE [App::DocumentObjectGroupPython] G4_P  # scripted group (container) (typed FeaturePython)
  Dunit = g/cm3
  Dvalue = 2.2
  Group = -> [P_element013]
  conduct = 2
  density = 1
  expand = 3
  formula = P
  name = G4_P
  specific = 4
FEATURE [App::DocumentObjectGroupPython] S_element023  label="S_element : 007"  # scripted group (container) (typed FeaturePython)
  n = 1
  ref = S_element
FEATURE [App::DocumentObjectGroupPython] G4_S  # scripted group (container) (typed FeaturePython)
  Dunit = g/cm3
  Dvalue = 2
  Group = -> [S_element023]
  conduct = 2
  density = 1
  expand = 3
  formula = S
  name = G4_S
  specific = 4
FEATURE [App::DocumentObjectGroupPython] Cl_element029  label="Cl_element : 015"  # scripted group (container) (typed FeaturePython)
  n = 1
  ref = Cl_element
FEATURE [App::DocumentObjectGroupPython] G4_Cl  # scripted group (container) (typed FeaturePython)
  Dunit = g/cm3
  Dvalue = 0.00299473
  Group = -> [Cl_element029]
  conduct = 2
  density = 1
  expand = 3
  formula = Cl
  name = G4_Cl
  specific = 4
FEATURE [App::DocumentObjectGroupPython] Ar_element002  label="Ar_element : 1"  # scripted group (container) (typed FeaturePython)
  n = 1
  ref = Ar_element
FEATURE [App::DocumentObjectGroupPython] G4_Ar  # scripted group (container) (typed FeaturePython)
  Dunit = g/cm3
  Dvalue = 0.00166201
  Group = -> [Ar_element002]
  conduct = 2
  density = 1
  expand = 3
  formula = Ar
  name = G4_Ar
  specific = 4
FEATURE [App::DocumentObjectGroupPython] K_element013  label="K_element : 003"  # scripted group (container) (typed FeaturePython)
  n = 1
  ref = K_element
FEATURE [App::DocumentObjectGroupPython] G4_K  # scripted group (container) (typed FeaturePython)
  Dunit = g/cm3
  Dvalue = 0.862
  Group = -> [K_element013]
  conduct = 2
  density = 1
  expand = 3
  formula = K
  name = G4_K
  specific = 4
FEATURE [App::DocumentObjectGroupPython] Ca_element014  label="Ca_element : 007"  # scripted group (container) (typed FeaturePython)
  n = 1
  ref = Ca_element
FEATURE [App::DocumentObjectGroupPython] G4_Ca  # scripted group (container) (typed FeaturePython)
  Dunit = g/cm3
  Dvalue = 1.55
  Group = -> [Ca_element014]
  conduct = 2
  density = 1
  expand = 3
  formula = Ca
  name = G4_Ca
  specific = 4
FEATURE [App::DocumentObjectGroupPython] Sc_element001  label="Sc_element : 1"  # scripted group (container) (typed FeaturePython)
  n = 1
  ref = Sc_element
FEATURE [App::DocumentObjectGroupPython] G4_Sc  # scripted group (container) (typed FeaturePython)
  Dunit = g/cm3
  Dvalue = 2.989
  Group = -> [Sc_element001]
  conduct = 2
  density = 1
  expand = 3
  formula = Sc
  name = G4_Sc
  specific = 4
FEATURE [App::DocumentObjectGroupPython] Ti_element004  label="Ti_element : 002"  # scripted group (container) (typed FeaturePython)
  n = 1
  ref = Ti_element
FEATURE [App::DocumentObjectGroupPython] G4_Ti  # scripted group (container) (typed FeaturePython)
  Dunit = g/cm3
  Dvalue = 4.54
  Group = -> [Ti_element004]
  conduct = 2
  density = 1
  expand = 3
  formula = Ti
  name = G4_Ti
  specific = 4
FEATURE [App::DocumentObjectGroupPython] V_element001  label="V_element : 1"  # scripted group (container) (typed FeaturePython)
  n = 1
  ref = V_element
FEATURE [App::DocumentObjectGroupPython] G4_V  # scripted group (container) (typed FeaturePython)
  Dunit = g/cm3
  Dvalue = 6.11
  Group = -> [V_element001]
  conduct = 2
  density = 1
  expand = 3
  formula = V
  name = G4_V
  specific = 4
FEATURE [App::DocumentObjectGroupPython] Cr_element001  label="Cr_element : 1"  # scripted group (container) (typed FeaturePython)
  n = 1
  ref = Cr_element
FEATURE [App::DocumentObjectGroupPython] G4_Cr  # scripted group (container) (typed FeaturePython)
  Dunit = g/cm3
  Dvalue = 7.18
  Group = -> [Cr_element001]
  conduct = 2
  density = 1
  expand = 3
  formula = Cr
  name = G4_Cr
  specific = 4
FEATURE [App::DocumentObjectGroupPython] Mn_element001  label="Mn_element : 1"  # scripted group (container) (typed FeaturePython)
  n = 1
  ref = Mn_element
FEATURE [App::DocumentObjectGroupPython] G4_Mn  # scripted group (container) (typed FeaturePython)
  Dunit = g/cm3
  Dvalue = 7.44
  Group = -> [Mn_element001]
  conduct = 2
  density = 1
  expand = 3
  formula = Mn
  name = G4_Mn
  specific = 4
FEATURE [App::DocumentObjectGroupPython] Fe_element007  label="Fe_element : 004"  # scripted group (container) (typed FeaturePython)
  n = 1
  ref = Fe_element
FEATURE [App::DocumentObjectGroupPython] G4_Fe  # scripted group (container) (typed FeaturePython)
  Dunit = g/cm3
  Dvalue = 7.874
  Group = -> [Fe_element007]
  conduct = 2
  density = 1
  expand = 3
  formula = Fe
  name = G4_Fe
  specific = 4
FEATURE [App::DocumentObjectGroupPython] Co_element001  label="Co_element : 1"  # scripted group (container) (typed FeaturePython)
  n = 1
  ref = Co_element
FEATURE [App::DocumentObjectGroupPython] G4_Co  # scripted group (container) (typed FeaturePython)
  Dunit = g/cm3
  Dvalue = 8.9
  Group = -> [Co_element001]
  conduct = 2
  density = 1
  expand = 3
  formula = Co
  name = G4_Co
  specific = 4
FEATURE [App::DocumentObjectGroupPython] Ni_element001  label="Ni_element : 1"  # scripted group (container) (typed FeaturePython)
  n = 1
  ref = Ni_element
FEATURE [App::DocumentObjectGroupPython] G4_Ni  # scripted group (container) (typed FeaturePython)
  Dunit = g/cm3
  Dvalue = 8.902
  Group = -> [Ni_element001]
  conduct = 2
  density = 1
  expand = 3
  formula = Ni
  name = G4_Ni
  specific = 4
FEATURE [App::DocumentObjectGroupPython] Cu_element001  label="Cu_element : 1"  # scripted group (container) (typed FeaturePython)
  n = 1
  ref = Cu_element
FEATURE [App::DocumentObjectGroupPython] G4_Cu  # scripted group (container) (typed FeaturePython)
  Dunit = g/cm3
  Dvalue = 8.96
  Group = -> [Cu_element001]
  conduct = 2
  density = 1
  expand = 3
  formula = Cu
  name = G4_Cu
  specific = 4
FEATURE [App::DocumentObjectGroupPython] Zn_element001  label="Zn_element : 1"  # scripted group (container) (typed FeaturePython)
  n = 1
  ref = Zn_element
FEATURE [App::DocumentObjectGroupPython] G4_Zn  # scripted group (container) (typed FeaturePython)
  Dunit = g/cm3
  Dvalue = 7.133
  Group = -> [Zn_element001]
  conduct = 2
  density = 1
  expand = 3
  formula = Zn
  name = G4_Zn
  specific = 4
FEATURE [App::DocumentObjectGroupPython] Ga_element002  label="Ga_element : 002"  # scripted group (container) (typed FeaturePython)
  n = 1
  ref = Ga_element
FEATURE [App::DocumentObjectGroupPython] G4_Ga  # scripted group (container) (typed FeaturePython)
  Dunit = g/cm3
  Dvalue = 5.904
  Group = -> [Ga_element002]
  conduct = 2
  density = 1
  expand = 3
  formula = Ga
  name = G4_Ga
  specific = 4
FEATURE [App::DocumentObjectGroupPython] Ge_element002  label="Ge_element : 1"  # scripted group (container) (typed FeaturePython)
  n = 1
  ref = Ge_element
FEATURE [App::DocumentObjectGroupPython] G4_Ge  # scripted group (container) (typed FeaturePython)
  Dunit = g/cm3
  Dvalue = 5.323
  Group = -> [Ge_element002]
  conduct = 2
  density = 1
  expand = 3
  formula = Ge
  name = G4_Ge
  specific = 4
FEATURE [App::DocumentObjectGroupPython] As_element003  label="As_element : 002"  # scripted group (container) (typed FeaturePython)
  n = 1
  ref = As_element
FEATURE [App::DocumentObjectGroupPython] G4_As  # scripted group (container) (typed FeaturePython)
  Dunit = g/cm3
  Dvalue = 5.73
  Group = -> [As_element003]
  conduct = 2
  density = 1
  expand = 3
  formula = As
  name = G4_As
  specific = 4
FEATURE [App::DocumentObjectGroupPython] Se_element001  label="Se_element : 1"  # scripted group (container) (typed FeaturePython)
  n = 1
  ref = Se_element
FEATURE [App::DocumentObjectGroupPython] G4_Se  # scripted group (container) (typed FeaturePython)
  Dunit = g/cm3
  Dvalue = 4.5
  Group = -> [Se_element001]
  conduct = 2
  density = 1
  expand = 3
  formula = Se
  name = G4_Se
  specific = 4
FEATURE [App::DocumentObjectGroupPython] Br_element007  label="Br_element : 004"  # scripted group (container) (typed FeaturePython)
  n = 1
  ref = Br_element
FEATURE [App::DocumentObjectGroupPython] G4_Br  # scripted group (container) (typed FeaturePython)
  Dunit = g/cm3
  Dvalue = 0.0070721
  Group = -> [Br_element007]
  conduct = 2
  density = 1
  expand = 3
  formula = Br
  name = G4_Br
  specific = 4
FEATURE [App::DocumentObjectGroupPython] Kr_element001  label="Kr_element : 1"  # scripted group (container) (typed FeaturePython)
  n = 1
  ref = Kr_element
FEATURE [App::DocumentObjectGroupPython] G4_Kr  # scripted group (container) (typed FeaturePython)
  Dunit = g/cm3
  Dvalue = 0.00347832
  Group = -> [Kr_element001]
  conduct = 2
  density = 1
  expand = 3
  formula = Kr
  name = G4_Kr
  specific = 4
FEATURE [App::DocumentObjectGroupPython] Rb_element001  label="Rb_element : 1"  # scripted group (container) (typed FeaturePython)
  n = 1
  ref = Rb_element
FEATURE [App::DocumentObjectGroupPython] G4_Rb  # scripted group (container) (typed FeaturePython)
  Dunit = g/cm3
  Dvalue = 1.532
  Group = -> [Rb_element001]
  conduct = 2
  density = 1
  expand = 3
  formula = Rb
  name = G4_Rb
  specific = 4
FEATURE [App::DocumentObjectGroupPython] Sr_element001  label="Sr_element : 1"  # scripted group (container) (typed FeaturePython)
  n = 1
  ref = Sr_element
FEATURE [App::DocumentObjectGroupPython] G4_Sr  # scripted group (container) (typed FeaturePython)
  Dunit = g/cm3
  Dvalue = 2.54
  Group = -> [Sr_element001]
  conduct = 2
  density = 1
  expand = 3
  formula = Sr
  name = G4_Sr
  specific = 4
FEATURE [App::DocumentObjectGroupPython] Y_element001  label="Y_element : 1"  # scripted group (container) (typed FeaturePython)
  n = 1
  ref = Y_element
FEATURE [App::DocumentObjectGroupPython] G4_Y  # scripted group (container) (typed FeaturePython)
  Dunit = g/cm3
  Dvalue = 4.469
  Group = -> [Y_element001]
  conduct = 2
  density = 1
  expand = 3
  formula = Y
  name = G4_Y
  specific = 4
FEATURE [App::DocumentObjectGroupPython] Zr_element001  label="Zr_element : 1"  # scripted group (container) (typed FeaturePython)
  n = 1
  ref = Zr_element
FEATURE [App::DocumentObjectGroupPython] G4_Zr  # scripted group (container) (typed FeaturePython)
  Dunit = g/cm3
  Dvalue = 6.506
  Group = -> [Zr_element001]
  conduct = 2
  density = 1
  expand = 3
  formula = Zr
  name = G4_Zr
  specific = 4
FEATURE [App::DocumentObjectGroupPython] Nb_element001  label="Nb_element : 1"  # scripted group (container) (typed FeaturePython)
  n = 1
  ref = Nb_element
FEATURE [App::DocumentObjectGroupPython] G4_Nb  # scripted group (container) (typed FeaturePython)
  Dunit = g/cm3
  Dvalue = 8.57
  Group = -> [Nb_element001]
  conduct = 2
  density = 1
  expand = 3
  formula = Nb
  name = G4_Nb
  specific = 4
FEATURE [App::DocumentObjectGroupPython] Mo_element001  label="Mo_element : 1"  # scripted group (container) (typed FeaturePython)
  n = 1
  ref = Mo_element
FEATURE [App::DocumentObjectGroupPython] G4_Mo  # scripted group (container) (typed FeaturePython)
  Dunit = g/cm3
  Dvalue = 10.22
  Group = -> [Mo_element001]
  conduct = 2
  density = 1
  expand = 3
  formula = Mo
  name = G4_Mo
  specific = 4
FEATURE [App::DocumentObjectGroupPython] Tc_element001  label="Tc_element : 1"  # scripted group (container) (typed FeaturePython)
  n = 1
  ref = Tc_element
FEATURE [App::DocumentObjectGroupPython] G4_Tc  # scripted group (container) (typed FeaturePython)
  Dunit = g/cm3
  Dvalue = 11.5
  Group = -> [Tc_element001]
  conduct = 2
  density = 1
  expand = 3
  formula = Tc
  name = G4_Tc
  specific = 4
FEATURE [App::DocumentObjectGroupPython] Ru_element001  label="Ru_element : 1"  # scripted group (container) (typed FeaturePython)
  n = 1
  ref = Ru_element
FEATURE [App::DocumentObjectGroupPython] G4_Ru  # scripted group (container) (typed FeaturePython)
  Dunit = g/cm3
  Dvalue = 12.41
  Group = -> [Ru_element001]
  conduct = 2
  density = 1
  expand = 3
  formula = Ru
  name = G4_Ru
  specific = 4
FEATURE [App::DocumentObjectGroupPython] Rh_element001  label="Rh_element : 1"  # scripted group (container) (typed FeaturePython)
  n = 1
  ref = Rh_element
FEATURE [App::DocumentObjectGroupPython] G4_Rh  # scripted group (container) (typed FeaturePython)
  Dunit = g/cm3
  Dvalue = 12.41
  Group = -> [Rh_element001]
  conduct = 2
  density = 1
  expand = 3
  formula = Rh
  name = G4_Rh
  specific = 4
FEATURE [App::DocumentObjectGroupPython] Pd_element001  label="Pd_element : 1"  # scripted group (container) (typed FeaturePython)
  n = 1
  ref = Pd_element
FEATURE [App::DocumentObjectGroupPython] G4_Pd  # scripted group (container) (typed FeaturePython)
  Dunit = g/cm3
  Dvalue = 12.02
  Group = -> [Pd_element001]
  conduct = 2
  density = 1
  expand = 3
  formula = Pd
  name = G4_Pd
  specific = 4
FEATURE [App::DocumentObjectGroupPython] Ag_element006  label="Ag_element : 004"  # scripted group (container) (typed FeaturePython)
  n = 1
  ref = Ag_element
FEATURE [App::DocumentObjectGroupPython] G4_Ag  # scripted group (container) (typed FeaturePython)
  Dunit = g/cm3
  Dvalue = 10.5
  Group = -> [Ag_element006]
  conduct = 2
  density = 1
  expand = 3
  formula = Ag
  name = G4_Ag
  specific = 4
FEATURE [App::DocumentObjectGroupPython] Cd_element003  label="Cd_element : 003"  # scripted group (container) (typed FeaturePython)
  n = 1
  ref = Cd_element
FEATURE [App::DocumentObjectGroupPython] G4_Cd  # scripted group (container) (typed FeaturePython)
  Dunit = g/cm3
  Dvalue = 8.65
  Group = -> [Cd_element003]
  conduct = 2
  density = 1
  expand = 3
  formula = Cd
  name = G4_Cd
  specific = 4
FEATURE [App::DocumentObjectGroupPython] In_element001  label="In_element : 1"  # scripted group (container) (typed FeaturePython)
  n = 1
  ref = In_element
FEATURE [App::DocumentObjectGroupPython] G4_In  # scripted group (container) (typed FeaturePython)
  Dunit = g/cm3
  Dvalue = 7.31
  Group = -> [In_element001]
  conduct = 2
  density = 1
  expand = 3
  formula = In
  name = G4_In
  specific = 4
FEATURE [App::DocumentObjectGroupPython] Sn_element001  label="Sn_element : 1"  # scripted group (container) (typed FeaturePython)
  n = 1
  ref = Sn_element
FEATURE [App::DocumentObjectGroupPython] G4_Sn  # scripted group (container) (typed FeaturePython)
  Dunit = g/cm3
  Dvalue = 7.31
  Group = -> [Sn_element001]
  conduct = 2
  density = 1
  expand = 3
  formula = Sn
  name = G4_Sn
  specific = 4
FEATURE [App::DocumentObjectGroupPython] Sb_element001  label="Sb_element : 1"  # scripted group (container) (typed FeaturePython)
  n = 1
  ref = Sb_element
FEATURE [App::DocumentObjectGroupPython] G4_Sb  # scripted group (container) (typed FeaturePython)
  Dunit = g/cm3
  Dvalue = 6.691
  Group = -> [Sb_element001]
  conduct = 2
  density = 1
  expand = 3
  formula = Sb
  name = G4_Sb
  specific = 4
FEATURE [App::DocumentObjectGroupPython] Te_element002  label="Te_element : 002"  # scripted group (container) (typed FeaturePython)
  n = 1
  ref = Te_element
FEATURE [App::DocumentObjectGroupPython] G4_Te  # scripted group (container) (typed FeaturePython)
  Dunit = g/cm3
  Dvalue = 6.24
  Group = -> [Te_element002]
  conduct = 2
  density = 1
  expand = 3
  formula = Te
  name = G4_Te
  specific = 4
FEATURE [App::DocumentObjectGroupPython] I_element010  label="I_element : 006"  # scripted group (container) (typed FeaturePython)
  n = 1
  ref = I_element
FEATURE [App::DocumentObjectGroupPython] G4_I  # scripted group (container) (typed FeaturePython)
  Dunit = g/cm3
  Dvalue = 4.93
  Group = -> [I_element010]
  conduct = 2
  density = 1
  expand = 3
  formula = I
  name = G4_I
  specific = 4
FEATURE [App::DocumentObjectGroupPython] Xe_element001  label="Xe_element : 1"  # scripted group (container) (typed FeaturePython)
  n = 1
  ref = Xe_element
FEATURE [App::DocumentObjectGroupPython] G4_Xe  # scripted group (container) (typed FeaturePython)
  Dunit = g/cm3
  Dvalue = 0.00548536
  Group = -> [Xe_element001]
  conduct = 2
  density = 1
  expand = 3
  formula = Xe
  name = G4_Xe
  specific = 4
FEATURE [App::DocumentObjectGroupPython] Cs_element003  label="Cs_element : 003"  # scripted group (container) (typed FeaturePython)
  n = 1
  ref = Cs_element
FEATURE [App::DocumentObjectGroupPython] G4_Cs  # scripted group (container) (typed FeaturePython)
  Dunit = g/cm3
  Dvalue = 1.873
  Group = -> [Cs_element003]
  conduct = 2
  density = 1
  expand = 3
  formula = Cs
  name = G4_Cs
  specific = 4
FEATURE [App::DocumentObjectGroupPython] Ba_element003  label="Ba_element : 003"  # scripted group (container) (typed FeaturePython)
  n = 1
  ref = Ba_element
FEATURE [App::DocumentObjectGroupPython] G4_Ba  # scripted group (container) (typed FeaturePython)
  Dunit = g/cm3
  Dvalue = 3.5
  Group = -> [Ba_element003]
  conduct = 2
  density = 1
  expand = 3
  formula = Ba
  name = G4_Ba
  specific = 4
FEATURE [App::DocumentObjectGroupPython] La_element003  label="La_element : 003"  # scripted group (container) (typed FeaturePython)
  n = 1
  ref = La_element
FEATURE [App::DocumentObjectGroupPython] G4_La  # scripted group (container) (typed FeaturePython)
  Dunit = g/cm3
  Dvalue = 6.154
  Group = -> [La_element003]
  conduct = 2
  density = 1
  expand = 3
  formula = La
  name = G4_La
  specific = 4
FEATURE [App::DocumentObjectGroupPython] Ce_element002  label="Ce_element : 1"  # scripted group (container) (typed FeaturePython)
  n = 1
  ref = Ce_element
FEATURE [App::DocumentObjectGroupPython] G4_Ce  # scripted group (container) (typed FeaturePython)
  Dunit = g/cm3
  Dvalue = 6.657
  Group = -> [Ce_element002]
  conduct = 2
  density = 1
  expand = 3
  formula = Ce
  name = G4_Ce
  specific = 4
FEATURE [App::DocumentObjectGroupPython] Pr_element001  label="Pr_element : 1"  # scripted group (container) (typed FeaturePython)
  n = 1
  ref = Pr_element
FEATURE [App::DocumentObjectGroupPython] G4_Pr  # scripted group (container) (typed FeaturePython)
  Dunit = g/cm3
  Dvalue = 6.71
  Group = -> [Pr_element001]
  conduct = 2
  density = 1
  expand = 3
  formula = Pr
  name = G4_Pr
  specific = 4
FEATURE [App::DocumentObjectGroupPython] Nd_element001  label="Nd_element : 1"  # scripted group (container) (typed FeaturePython)
  n = 1
  ref = Nd_element
FEATURE [App::DocumentObjectGroupPython] G4_Nd  # scripted group (container) (typed FeaturePython)
  Dunit = g/cm3
  Dvalue = 6.9
  Group = -> [Nd_element001]
  conduct = 2
  density = 1
  expand = 3
  formula = Nd
  name = G4_Nd
  specific = 4
FEATURE [App::DocumentObjectGroupPython] Pm_element001  label="Pm_element : 1"  # scripted group (container) (typed FeaturePython)
  n = 1
  ref = Pm_element
FEATURE [App::DocumentObjectGroupPython] G4_Pm  # scripted group (container) (typed FeaturePython)
  Dunit = g/cm3
  Dvalue = 7.22
  Group = -> [Pm_element001]
  conduct = 2
  density = 1
  expand = 3
  formula = Pm
  name = G4_Pm
  specific = 4
FEATURE [App::DocumentObjectGroupPython] Sm_element001  label="Sm_element : 1"  # scripted group (container) (typed FeaturePython)
  n = 1
  ref = Sm_element
FEATURE [App::DocumentObjectGroupPython] G4_Sm  # scripted group (container) (typed FeaturePython)
  Dunit = g/cm3
  Dvalue = 7.46
  Group = -> [Sm_element001]
  conduct = 2
  density = 1
  expand = 3
  formula = Sm
  name = G4_Sm
  specific = 4
FEATURE [App::DocumentObjectGroupPython] Eu_element001  label="Eu_element : 1"  # scripted group (container) (typed FeaturePython)
  n = 1
  ref = Eu_element
FEATURE [App::DocumentObjectGroupPython] G4_Eu  # scripted group (container) (typed FeaturePython)
  Dunit = g/cm3
  Dvalue = 5.243
  Group = -> [Eu_element001]
  conduct = 2
  density = 1
  expand = 3
  formula = Eu
  name = G4_Eu
  specific = 4
FEATURE [App::DocumentObjectGroupPython] Gd_element002  label="Gd_element : 1"  # scripted group (container) (typed FeaturePython)
  n = 1
  ref = Gd_element
FEATURE [App::DocumentObjectGroupPython] G4_Gd  # scripted group (container) (typed FeaturePython)
  Dunit = g/cm3
  Dvalue = 7.9004
  Group = -> [Gd_element002]
  conduct = 2
  density = 1
  expand = 3
  formula = Gd
  name = G4_Gd
  specific = 4
FEATURE [App::DocumentObjectGroupPython] Tb_element001  label="Tb_element : 1"  # scripted group (container) (typed FeaturePython)
  n = 1
  ref = Tb_element
FEATURE [App::DocumentObjectGroupPython] G4_Tb  # scripted group (container) (typed FeaturePython)
  Dunit = g/cm3
  Dvalue = 8.229
  Group = -> [Tb_element001]
  conduct = 2
  density = 1
  expand = 3
  formula = Tb
  name = G4_Tb
  specific = 4
FEATURE [App::DocumentObjectGroupPython] Dy_element001  label="Dy_element : 1"  # scripted group (container) (typed FeaturePython)
  n = 1
  ref = Dy_element
FEATURE [App::DocumentObjectGroupPython] G4_Dy  # scripted group (container) (typed FeaturePython)
  Dunit = g/cm3
  Dvalue = 8.55
  Group = -> [Dy_element001]
  conduct = 2
  density = 1
  expand = 3
  formula = Dy
  name = G4_Dy
  specific = 4
FEATURE [App::DocumentObjectGroupPython] Ho_element001  label="Ho_element : 1"  # scripted group (container) (typed FeaturePython)
  n = 1
  ref = Ho_element
FEATURE [App::DocumentObjectGroupPython] G4_Ho  # scripted group (container) (typed FeaturePython)
  Dunit = g/cm3
  Dvalue = 8.795
  Group = -> [Ho_element001]
  conduct = 2
  density = 1
  expand = 3
  formula = Ho
  name = G4_Ho
  specific = 4
FEATURE [App::DocumentObjectGroupPython] Er_element001  label="Er_element : 1"  # scripted group (container) (typed FeaturePython)
  n = 1
  ref = Er_element
FEATURE [App::DocumentObjectGroupPython] G4_Er  # scripted group (container) (typed FeaturePython)
  Dunit = g/cm3
  Dvalue = 9.066
  Group = -> [Er_element001]
  conduct = 2
  density = 1
  expand = 3
  formula = Er
  name = G4_Er
  specific = 4
FEATURE [App::DocumentObjectGroupPython] Tm_element001  label="Tm_element : 1"  # scripted group (container) (typed FeaturePython)
  n = 1
  ref = Tm_element
FEATURE [App::DocumentObjectGroupPython] G4_Tm  # scripted group (container) (typed FeaturePython)
  Dunit = g/cm3
  Dvalue = 9.321
  Group = -> [Tm_element001]
  conduct = 2
  density = 1
  expand = 3
  formula = Tm
  name = G4_Tm
  specific = 4
FEATURE [App::DocumentObjectGroupPython] Yb_element001  label="Yb_element : 1"  # scripted group (container) (typed FeaturePython)
  n = 1
  ref = Yb_element
FEATURE [App::DocumentObjectGroupPython] G4_Yb  # scripted group (container) (typed FeaturePython)
  Dunit = g/cm3
  Dvalue = 6.73
  Group = -> [Yb_element001]
  conduct = 2
  density = 1
  expand = 3
  formula = Yb
  name = G4_Yb
  specific = 4
FEATURE [App::DocumentObjectGroupPython] Lu_element001  label="Lu_element : 1"  # scripted group (container) (typed FeaturePython)
  n = 1
  ref = Lu_element
FEATURE [App::DocumentObjectGroupPython] G4_Lu  # scripted group (container) (typed FeaturePython)
  Dunit = g/cm3
  Dvalue = 9.84
  Group = -> [Lu_element001]
  conduct = 2
  density = 1
  expand = 3
  formula = Lu
  name = G4_Lu
  specific = 4
FEATURE [App::DocumentObjectGroupPython] Hf_element001  label="Hf_element : 1"  # scripted group (container) (typed FeaturePython)
  n = 1
  ref = Hf_element
FEATURE [App::DocumentObjectGroupPython] G4_Hf  # scripted group (container) (typed FeaturePython)
  Dunit = g/cm3
  Dvalue = 13.31
  Group = -> [Hf_element001]
  conduct = 2
  density = 1
  expand = 3
  formula = Hf
  name = G4_Hf
  specific = 4
FEATURE [App::DocumentObjectGroupPython] Ta_element001  label="Ta_element : 1"  # scripted group (container) (typed FeaturePython)
  n = 1
  ref = Ta_element
FEATURE [App::DocumentObjectGroupPython] G4_Ta  # scripted group (container) (typed FeaturePython)
  Dunit = g/cm3
  Dvalue = 16.654
  Group = -> [Ta_element001]
  conduct = 2
  density = 1
  expand = 3
  formula = Ta
  name = G4_Ta
  specific = 4
FEATURE [App::DocumentObjectGroupPython] W_element004  label="W_element : 004"  # scripted group (container) (typed FeaturePython)
  n = 1
  ref = W_element
FEATURE [App::DocumentObjectGroupPython] G4_W  # scripted group (container) (typed FeaturePython)
  Dunit = g/cm3
  Dvalue = 19.3
  Group = -> [W_element004]
  conduct = 2
  density = 1
  expand = 3
  formula = W
  name = G4_W
  specific = 4
FEATURE [App::DocumentObjectGroupPython] Re_element001  label="Re_element : 1"  # scripted group (container) (typed FeaturePython)
  n = 1
  ref = Re_element
FEATURE [App::DocumentObjectGroupPython] G4_Re  # scripted group (container) (typed FeaturePython)
  Dunit = g/cm3
  Dvalue = 21.02
  Group = -> [Re_element001]
  conduct = 2
  density = 1
  expand = 3
  formula = Re
  name = G4_Re
  specific = 4
FEATURE [App::DocumentObjectGroupPython] Os_element001  label="Os_element : 1"  # scripted group (container) (typed FeaturePython)
  n = 1
  ref = Os_element
FEATURE [App::DocumentObjectGroupPython] G4_Os  # scripted group (container) (typed FeaturePython)
  Dunit = g/cm3
  Dvalue = 22.57
  Group = -> [Os_element001]
  conduct = 2
  density = 1
  expand = 3
  formula = Os
  name = G4_Os
  specific = 4
FEATURE [App::DocumentObjectGroupPython] Ir_element001  label="Ir_element : 1"  # scripted group (container) (typed FeaturePython)
  n = 1
  ref = Ir_element
FEATURE [App::DocumentObjectGroupPython] G4_Ir  # scripted group (container) (typed FeaturePython)
  Dunit = g/cm3
  Dvalue = 22.42
  Group = -> [Ir_element001]
  conduct = 2
  density = 1
  expand = 3
  formula = Ir
  name = G4_Ir
  specific = 4
FEATURE [App::DocumentObjectGroupPython] Pt_element001  label="Pt_element : 1"  # scripted group (container) (typed FeaturePython)
  n = 1
  ref = Pt_element
FEATURE [App::DocumentObjectGroupPython] G4_Pt  # scripted group (container) (typed FeaturePython)
  Dunit = g/cm3
  Dvalue = 21.45
  Group = -> [Pt_element001]
  conduct = 2
  density = 1
  expand = 3
  formula = Pt
  name = G4_Pt
  specific = 4
FEATURE [App::DocumentObjectGroupPython] Au_element001  label="Au_element : 1"  # scripted group (container) (typed FeaturePython)
  n = 1
  ref = Au_element
FEATURE [App::DocumentObjectGroupPython] G4_Au  # scripted group (container) (typed FeaturePython)
  Dunit = g/cm3
  Dvalue = 19.32
  Group = -> [Au_element001]
  conduct = 2
  density = 1
  expand = 3
  formula = Au
  name = G4_Au
  specific = 4
FEATURE [App::DocumentObjectGroupPython] Hg_element002  label="Hg_element : 002"  # scripted group (container) (typed FeaturePython)
  n = 1
  ref = Hg_element
FEATURE [App::DocumentObjectGroupPython] G4_Hg  # scripted group (container) (typed FeaturePython)
  Dunit = g/cm3
  Dvalue = 13.546
  Group = -> [Hg_element002]
  conduct = 2
  density = 1
  expand = 3
  formula = Hg
  name = G4_Hg
  specific = 4
FEATURE [App::DocumentObjectGroupPython] Tl_element002  label="Tl_element : 002"  # scripted group (container) (typed FeaturePython)
  n = 1
  ref = Tl_element
FEATURE [App::DocumentObjectGroupPython] G4_Tl  # scripted group (container) (typed FeaturePython)
  Dunit = g/cm3
  Dvalue = 11.72
  Group = -> [Tl_element002]
  conduct = 2
  density = 1
  expand = 3
  formula = Tl
  name = G4_Tl
  specific = 4
FEATURE [App::DocumentObjectGroupPython] Pb_element003  label="Pb_element : 1"  # scripted group (container) (typed FeaturePython)
  n = 1
  ref = Pb_element
FEATURE [App::DocumentObjectGroupPython] G4_Pb  # scripted group (container) (typed FeaturePython)
  Dunit = g/cm3
  Dvalue = 11.35
  Group = -> [Pb_element003]
  conduct = 2
  density = 1
  expand = 3
  formula = Pb
  name = G4_Pb
  specific = 4
FEATURE [App::DocumentObjectGroupPython] Bi_element002  label="Bi_element : 1"  # scripted group (container) (typed FeaturePython)
  n = 1
  ref = Bi_element
FEATURE [App::DocumentObjectGroupPython] G4_Bi  # scripted group (container) (typed FeaturePython)
  Dunit = g/cm3
  Dvalue = 9.747
  Group = -> [Bi_element002]
  conduct = 2
  density = 1
  expand = 3
  formula = Bi
  name = G4_Bi
  specific = 4
FEATURE [App::DocumentObjectGroupPython] Po_element001  label="Po_element : 1"  # scripted group (container) (typed FeaturePython)
  n = 1
  ref = Po_element
FEATURE [App::DocumentObjectGroupPython] G4_Po  # scripted group (container) (typed FeaturePython)
  Dunit = g/cm3
  Dvalue = 9.32
  Group = -> [Po_element001]
  conduct = 2
  density = 1
  expand = 3
  formula = Po
  name = G4_Po
  specific = 4
FEATURE [App::DocumentObjectGroupPython] At_element001  label="At_element : 1"  # scripted group (container) (typed FeaturePython)
  n = 1
  ref = At_element
FEATURE [App::DocumentObjectGroupPython] G4_At  # scripted group (container) (typed FeaturePython)
  Dunit = g/cm3
  Dvalue = 9.32
  Group = -> [At_element001]
  conduct = 2
  density = 1
  expand = 3
  formula = At
  name = G4_At
  specific = 4
FEATURE [App::DocumentObjectGroupPython] Rn_element001  label="Rn_element : 1"  # scripted group (container) (typed FeaturePython)
  n = 1
  ref = Rn_element
FEATURE [App::DocumentObjectGroupPython] G4_Rn  # scripted group (container) (typed FeaturePython)
  Dunit = g/cm3
  Dvalue = 0.00900662
  Group = -> [Rn_element001]
  conduct = 2
  density = 1
  expand = 3
  formula = Rn
  name = G4_Rn
  specific = 4
FEATURE [App::DocumentObjectGroupPython] Fr_element001  label="Fr_element : 1"  # scripted group (container) (typed FeaturePython)
  n = 1
  ref = Fr_element
FEATURE [App::DocumentObjectGroupPython] G4_Fr  # scripted group (container) (typed FeaturePython)
  Dunit = g/cm3
  Dvalue = 1
  Group = -> [Fr_element001]
  conduct = 2
  density = 1
  expand = 3
  formula = Fr
  name = G4_Fr
  specific = 4
FEATURE [App::DocumentObjectGroupPython] Ra_element001  label="Ra_element : 1"  # scripted group (container) (typed FeaturePython)
  n = 1
  ref = Ra_element
FEATURE [App::DocumentObjectGroupPython] G4_Ra  # scripted group (container) (typed FeaturePython)
  Dunit = g/cm3
  Dvalue = 5
  Group = -> [Ra_element001]
  conduct = 2
  density = 1
  expand = 3
  formula = Ra
  name = G4_Ra
  specific = 4
FEATURE [App::DocumentObjectGroupPython] Ac_element001  label="Ac_element : 1"  # scripted group (container) (typed FeaturePython)
  n = 1
  ref = Ac_element
FEATURE [App::DocumentObjectGroupPython] G4_Ac  # scripted group (container) (typed FeaturePython)
  Dunit = g/cm3
  Dvalue = 10.07
  Group = -> [Ac_element001]
  conduct = 2
  density = 1
  expand = 3
  formula = Ac
  name = G4_Ac
  specific = 4
FEATURE [App::DocumentObjectGroupPython] Th_element001  label="Th_element : 1"  # scripted group (container) (typed FeaturePython)
  n = 1
  ref = Th_element
FEATURE [App::DocumentObjectGroupPython] G4_Th  # scripted group (container) (typed FeaturePython)
  Dunit = g/cm3
  Dvalue = 11.72
  Group = -> [Th_element001]
  conduct = 2
  density = 1
  expand = 3
  formula = Th
  name = G4_Th
  specific = 4
FEATURE [App::DocumentObjectGroupPython] Pa_element001  label="Pa_element : 1"  # scripted group (container) (typed FeaturePython)
  n = 1
  ref = Pa_element
FEATURE [App::DocumentObjectGroupPython] G4_Pa  # scripted group (container) (typed FeaturePython)
  Dunit = g/cm3
  Dvalue = 15.37
  Group = -> [Pa_element001]
  conduct = 2
  density = 1
  expand = 3
  formula = Pa
  name = G4_Pa
  specific = 4
FEATURE [App::DocumentObjectGroupPython] U_element004  label="U_element : 004"  # scripted group (container) (typed FeaturePython)
  n = 1
  ref = U_element
FEATURE [App::DocumentObjectGroupPython] G4_U  # scripted group (container) (typed FeaturePython)
  Dunit = g/cm3
  Dvalue = 18.95
  Group = -> [U_element004]
  conduct = 2
  density = 1
  expand = 3
  formula = U
  name = G4_U
  specific = 4
FEATURE [App::DocumentObjectGroupPython] Np_element001  label="Np_element : 1"  # scripted group (container) (typed FeaturePython)
  n = 1
  ref = Np_element
FEATURE [App::DocumentObjectGroupPython] G4_Np  # scripted group (container) (typed FeaturePython)
  Dunit = g/cm3
  Dvalue = 20.25
  Group = -> [Np_element001]
  conduct = 2
  density = 1
  expand = 3
  formula = Np
  name = G4_Np
  specific = 4
FEATURE [App::DocumentObjectGroupPython] Pu_element002  label="Pu_element : 002"  # scripted group (container) (typed FeaturePython)
  n = 1
  ref = Pu_element
FEATURE [App::DocumentObjectGroupPython] G4_Pu  # scripted group (container) (typed FeaturePython)
  Dunit = g/cm3
  Dvalue = 19.84
  Group = -> [Pu_element002]
  conduct = 2
  density = 1
  expand = 3
  formula = Pu
  name = G4_Pu
  specific = 4
FEATURE [App::DocumentObjectGroupPython] Am_element001  label="Am_element : 1"  # scripted group (container) (typed FeaturePython)
  n = 1
  ref = Am_element
FEATURE [App::DocumentObjectGroupPython] G4_Am  # scripted group (container) (typed FeaturePython)
  Dunit = g/cm3
  Dvalue = 13.67
  Group = -> [Am_element001]
  conduct = 2
  density = 1
  expand = 3
  formula = Am
  name = G4_Am
  specific = 4
FEATURE [App::DocumentObjectGroupPython] Cm_element001  label="Cm_element : 1"  # scripted group (container) (typed FeaturePython)
  n = 1
  ref = Cm_element
FEATURE [App::DocumentObjectGroupPython] G4_Cm  # scripted group (container) (typed FeaturePython)
  Dunit = g/cm3
  Dvalue = 13.51
  Group = -> [Cm_element001]
  conduct = 2
  density = 1
  expand = 3
  formula = Cm
  name = G4_Cm
  specific = 4
FEATURE [App::DocumentObjectGroupPython] Bk_element001  label="Bk_element : 1"  # scripted group (container) (typed FeaturePython)
  n = 1
  ref = Bk_element
FEATURE [App::DocumentObjectGroupPython] G4_Bk  # scripted group (container) (typed FeaturePython)
  Dunit = g/cm3
  Dvalue = 14
  Group = -> [Bk_element001]
  conduct = 2
  density = 1
  expand = 3
  formula = Bk
  name = G4_Bk
  specific = 4
FEATURE [App::DocumentObjectGroupPython] Cf_element001  label="Cf_element : 1"  # scripted group (container) (typed FeaturePython)
  n = 1
  ref = Cf_element
FEATURE [App::DocumentObjectGroupPython] G4_Cf  # scripted group (container) (typed FeaturePython)
  Dunit = g/cm3
  Dvalue = 10
  Group = -> [Cf_element001]
  conduct = 2
  density = 1
  expand = 3
  formula = Cf
  name = G4_Cf
  specific = 4
FEATURE [App::DocumentObjectGroupPython] Element  # scripted group (container) (typed FeaturePython)
  Group = -> [G4_H,G4_He,G4_Li,G4_Be,G4_B,G4_C,G4_N,G4_O,G4_F,G4_Ne,G4_Na,G4_Mg,G4_Al,G4_Si,G4_P,G4_S,G4_Cl,G4_Ar,G4_K,G4_Ca,G4_Sc,G4_Ti,G4_V,G4_Cr,G4_Mn,G4_Fe,G4_Co,G4_Ni,G4_Cu,G4_Zn,G4_Ga,G4_Ge,G4_As,G4_Se,G4_Br,G4_Kr,G4_Rb,G4_Sr,G4_Y,G4_Zr,G4_Nb,G4_Mo,G4_Tc,G4_Ru,G4_Rh,G4_Pd,G4_Ag,G4_Cd,G4_In,G4_Sn,G4_Sb,G4_Te,G4_I,G4_Xe,G4_Cs,G4_Ba,G4_La,G4_Ce,G4_Pr,G4_Nd,G4_Pm,G4_Sm,G4_Eu,G4_Gd,G4_Tb,G4_Dy,G4_Ho,G4_Er,+30 more]
FEATURE [App::DocumentObjectGroupPython] H_element114  label="H_element : 063"  # scripted group (container) (typed FeaturePython)
  n = 2
  ref = H_element
FEATURE [App::DocumentObjectGroupPython] G4_lH2  # scripted group (container) (typed FeaturePython)
  Dunit = g/cm3
  Dvalue = 0.0708
  Group = -> [H_element114]
  conduct = 2
  density = 1
  expand = 3
  formula = G4_lH2
  name = G4_lH2
  specific = 4
FEATURE [App::DocumentObjectGroupPython] N_element049  label="N_element : 022"  # scripted group (container) (typed FeaturePython)
  n = 2
  ref = N_element
FEATURE [App::DocumentObjectGroupPython] G4_lN2  # scripted group (container) (typed FeaturePython)
  Dunit = g/cm3
  Dvalue = 0.807
  Group = -> [N_element049]
  conduct = 2
  density = 1
  expand = 3
  formula = G4_lN2
  name = G4_lN2
  specific = 4
FEATURE [App::DocumentObjectGroupPython] O_element106  label="O_element : 060"  # scripted group (container) (typed FeaturePython)
  n = 2
  ref = O_element
FEATURE [App::DocumentObjectGroupPython] G4_lO2  # scripted group (container) (typed FeaturePython)
  Dunit = g/cm3
  Dvalue = 1.141
  Group = -> [O_element106]
  conduct = 2
  density = 1
  expand = 3
  formula = G4_lO2
  name = G4_lO2
  specific = 4
FEATURE [App::DocumentObjectGroupPython] Ar  label="Ar : 1"  # scripted group (container) (typed FeaturePython)
  n = 1
  ref = Ar
FEATURE [App::DocumentObjectGroupPython] G4_lAr  # scripted group (container) (typed FeaturePython)
  Dunit = g/cm3
  Dvalue = 1.396
  Group = -> [Ar]
  conduct = 2
  density = 1
  expand = 3
  formula = G4_lAr
  name = G4_lAr
  specific = 4
FEATURE [App::DocumentObjectGroupPython] Br  label="Br : 1"  # scripted group (container) (typed FeaturePython)
  n = 1
  ref = Br
FEATURE [App::DocumentObjectGroupPython] G4_lBr  # scripted group (container) (typed FeaturePython)
  Dunit = g/cm3
  Dvalue = 3.1028
  Group = -> [Br]
  conduct = 2
  density = 1
  expand = 3
  formula = G4_lBr
  name = G4_lBr
  specific = 4
FEATURE [App::DocumentObjectGroupPython] Kr  label="Kr : 1"  # scripted group (container) (typed FeaturePython)
  n = 1
  ref = Kr
FEATURE [App::DocumentObjectGroupPython] G4_lKr  # scripted group (container) (typed FeaturePython)
  Dunit = g/cm3
  Dvalue = 2.418
  Group = -> [Kr]
  conduct = 2
  density = 1
  expand = 3
  formula = G4_lKr
  name = G4_lKr
  specific = 4
FEATURE [App::DocumentObjectGroupPython] Xe  label="Xe : 1"  # scripted group (container) (typed FeaturePython)
  n = 1
  ref = Xe
FEATURE [App::DocumentObjectGroupPython] G4_lXe  # scripted group (container) (typed FeaturePython)
  Dunit = g/cm3
  Dvalue = 2.953
  Group = -> [Xe]
  conduct = 2
  density = 1
  expand = 3
  formula = G4_lXe
  name = G4_lXe
  specific = 4
FEATURE [App::DocumentObjectGroupPython] O_element107  label="O_element : 061"  # scripted group (container) (typed FeaturePython)
  n = 4
  ref = O_element
FEATURE [App::DocumentObjectGroupPython] Pb_element004  label="Pb_element : 002"  # scripted group (container) (typed FeaturePython)
  n = 1
  ref = Pb_element
FEATURE [App::DocumentObjectGroupPython] W_element005  label="W_element : 005"  # scripted group (container) (typed FeaturePython)
  n = 1
  ref = W_element
FEATURE [App::DocumentObjectGroupPython] G4_PbWO4  # scripted group (container) (typed FeaturePython)
  Dunit = g/cm3
  Dvalue = 8.28
  Group = -> [O_element107,Pb_element004,W_element005]
  conduct = 2
  density = 1
  expand = 3
  formula = G4_PbWO4
  name = G4_PbWO4
  specific = 4
FEATURE [App::DocumentObjectGroupPython] alactic  label="alactic : 1"  # scripted group (container) (typed FeaturePython)
  n = 1
  ref = alactic
FEATURE [App::DocumentObjectGroupPython] G4_Galactic  # scripted group (container) (typed FeaturePython)
  Dunit = g/cm3
  Dvalue = 0
  Group = -> [alactic]
  conduct = 2
  density = 1
  expand = 3
  formula = G4_Galactic
  name = G4_Galactic
  specific = 4
FEATURE [App::DocumentObjectGroupPython] RAPHITE_POROUS  label="RAPHITE_POROUS : 1"  # scripted group (container) (typed FeaturePython)
  n = 1
  ref = RAPHITE_POROUS
FEATURE [App::DocumentObjectGroupPython] G4_GRAPHITE_POROUS  # scripted group (container) (typed FeaturePython)
  Dunit = g/cm3
  Dvalue = 1.7
  Group = -> [RAPHITE_POROUS]
  conduct = 2
  density = 1
  expand = 3
  formula = G4_GRAPHITE_POROUS
  name = G4_GRAPHITE_POROUS
  specific = 4
FEATURE [App::DocumentObjectGroupPython] H_element115  label="H_element : 0.150"  # scripted group (container) (typed FeaturePython)
  n = 0.080538
FEATURE [App::DocumentObjectGroupPython] C_element125  label="C_element : 0.600"  # scripted group (container) (typed FeaturePython)
  n = 0.599848
FEATURE [App::DocumentObjectGroupPython] O_element108  label="O_element : 0.320"  # scripted group (container) (typed FeaturePython)
  n = 0.319614
FEATURE [App::DocumentObjectGroupPython] G4_LUCITE  # scripted group (container) (typed FeaturePython)
  Dunit = g/cm3
  Dvalue = 1.19
  Group = -> [H_element115,C_element125,O_element108]
  conduct = 2
  density = 1
  expand = 3
  formula = G4_LUCITE
  name = G4_LUCITE
  specific = 4
FEATURE [App::DocumentObjectGroupPython] Cu_element002  label="Cu_element : 62"  # scripted group (container) (typed FeaturePython)
  n = 62
  ref = Cu_element
FEATURE [App::DocumentObjectGroupPython] Zn_element002  label="Zn_element : 35"  # scripted group (container) (typed FeaturePython)
  n = 35
  ref = Zn_element
FEATURE [App::DocumentObjectGroupPython] Pb_element005  label="Pb_element : 3"  # scripted group (container) (typed FeaturePython)
  n = 3
  ref = Pb_element
FEATURE [App::DocumentObjectGroupPython] G4_BRASS  # scripted group (container) (typed FeaturePython)
  Dunit = g/cm3
  Dvalue = 8.52
  Group = -> [Cu_element002,Zn_element002,Pb_element005]
  conduct = 2
  density = 1
  expand = 3
  formula = G4_BRASS
  name = G4_BRASS
  specific = 4
FEATURE [App::DocumentObjectGroupPython] Cu_element003  label="Cu_element : 89"  # scripted group (container) (typed FeaturePython)
  n = 89
  ref = Cu_element
FEATURE [App::DocumentObjectGroupPython] Zn_element003  label="Zn_element : 9"  # scripted group (container) (typed FeaturePython)
  n = 9
  ref = Zn_element
FEATURE [App::DocumentObjectGroupPython] Pb_element006  label="Pb_element : 2"  # scripted group (container) (typed FeaturePython)
  n = 2
  ref = Pb_element
FEATURE [App::DocumentObjectGroupPython] G4_BRONZE  # scripted group (container) (typed FeaturePython)
  Dunit = g/cm3
  Dvalue = 8.82
  Group = -> [Cu_element003,Zn_element003,Pb_element006]
  conduct = 2
  density = 1
  expand = 3
  formula = G4_BRONZE
  name = G4_BRONZE
  specific = 4
FEATURE [App::DocumentObjectGroupPython] Fe_element008  label="Fe_element : 74"  # scripted group (container) (typed FeaturePython)
  n = 74
  ref = Fe_element
FEATURE [App::DocumentObjectGroupPython] Cr_element002  label="Cr_element : 18"  # scripted group (container) (typed FeaturePython)
  n = 18
  ref = Cr_element
FEATURE [App::DocumentObjectGroupPython] Ni_element002  label="Ni_element : 8"  # scripted group (container) (typed FeaturePython)
  n = 8
  ref = Ni_element
FEATURE [App::DocumentObjectGroupPython] G4_STAINLESS_STEEL  label="G4_STAINLESS-STEEL"  # scripted group (container) (typed FeaturePython)
  Dunit = g/cm3
  Dvalue = 8
  Group = -> [Fe_element008,Cr_element002,Ni_element002]
  conduct = 2
  density = 1
  expand = 3
  formula = G4_STAINLESS-STEEL
  name = G4_STAINLESS-STEEL
  specific = 4
FEATURE [App::DocumentObjectGroupPython] H_element116  label="H_element : 064"  # scripted group (container) (typed FeaturePython)
  n = 18
  ref = H_element
FEATURE [App::DocumentObjectGroupPython] C_element126  label="C_element : 071"  # scripted group (container) (typed FeaturePython)
  n = 12
  ref = C_element
FEATURE [App::DocumentObjectGroupPython] O_element109  label="O_element : 062"  # scripted group (container) (typed FeaturePython)
  n = 7
  ref = O_element
FEATURE [App::DocumentObjectGroupPython] G4_CR39  # scripted group (container) (typed FeaturePython)
  Dunit = g/cm3
  Dvalue = 1.32
  Group = -> [H_element116,C_element126,O_element109]
  conduct = 2
  density = 1
  expand = 3
  formula = G4_CR39
  name = G4_CR39
  specific = 4
FEATURE [App::DocumentObjectGroupPython] H_element117  label="H_element : 38"  # scripted group (container) (typed FeaturePython)
  n = 38
  ref = H_element
FEATURE [App::DocumentObjectGroupPython] C_element127  label="C_element : 072"  # scripted group (container) (typed FeaturePython)
  n = 18
  ref = C_element
FEATURE [App::DocumentObjectGroupPython] O_element110  label="O_element : 063"  # scripted group (container) (typed FeaturePython)
  n = 1
  ref = O_element
FEATURE [App::DocumentObjectGroupPython] G4_OCTADECANOL  # scripted group (container) (typed FeaturePython)
  Dunit = g/cm3
  Dvalue = 0.812
  Group = -> [H_element117,C_element127,O_element110]
  conduct = 2
  density = 1
  expand = 3
  formula = G4_OCTADECANOL
  name = G4_OCTADECANOL
  specific = 4
FEATURE [App::DocumentObjectGroupPython] HEP  # scripted group (container) (typed FeaturePython)
  Group = -> [G4_lH2,G4_lN2,G4_lO2,G4_lAr,G4_lBr,G4_lKr,G4_lXe,G4_PbWO4,G4_Galactic,G4_GRAPHITE_POROUS,G4_LUCITE,G4_BRASS,G4_BRONZE,G4_STAINLESS_STEEL,G4_CR39,G4_OCTADECANOL]
FEATURE [App::DocumentObjectGroupPython] C_element128  label="C_element : 073"  # scripted group (container) (typed FeaturePython)
  n = 14
  ref = C_element
FEATURE [App::DocumentObjectGroupPython] H_element118  label="H_element : 065"  # scripted group (container) (typed FeaturePython)
  n = 10
  ref = H_element
FEATURE [App::DocumentObjectGroupPython] O_element111  label="O_element : 064"  # scripted group (container) (typed FeaturePython)
  n = 2
  ref = O_element
FEATURE [App::DocumentObjectGroupPython] N_element050  label="N_element : 023"  # scripted group (container) (typed FeaturePython)
  n = 2
  ref = N_element
FEATURE [App::DocumentObjectGroupPython] G4_KEVLAR  # scripted group (container) (typed FeaturePython)
  Dunit = g/cm3
  Dvalue = 1.44
  Group = -> [C_element128,H_element118,O_element111,N_element050]
  conduct = 2
  density = 1
  expand = 3
  formula = G4_KEVLAR
  name = G4_KEVLAR
  specific = 4
FEATURE [App::DocumentObjectGroupPython] C_element129  label="C_element : 074"  # scripted group (container) (typed FeaturePython)
  n = 10
  ref = C_element
FEATURE [App::DocumentObjectGroupPython] H_element119  label="H_element : 066"  # scripted group (container) (typed FeaturePython)
  n = 8
  ref = H_element
FEATURE [App::DocumentObjectGroupPython] O_element112  label="O_element : 065"  # scripted group (container) (typed FeaturePython)
  n = 4
  ref = O_element
FEATURE [App::DocumentObjectGroupPython] G4_DACRON  # scripted group (container) (typed FeaturePython)
  Dunit = g/cm3
  Dvalue = 1.4
  Group = -> [C_element129,H_element119,O_element112]
  conduct = 2
  density = 1
  expand = 3
  formula = G4_DACRON
  name = G4_DACRON
  specific = 4
FEATURE [App::DocumentObjectGroupPython] C_element130  label="C_element : 075"  # scripted group (container) (typed FeaturePython)
  n = 4
  ref = C_element
FEATURE [App::DocumentObjectGroupPython] H_element120  label="H_element : 067"  # scripted group (container) (typed FeaturePython)
  n = 5
  ref = H_element
FEATURE [App::DocumentObjectGroupPython] Cl_element030  label="Cl_element : 016"  # scripted group (container) (typed FeaturePython)
  n = 1
  ref = Cl_element
FEATURE [App::DocumentObjectGroupPython] G4_NEOPRENE  # scripted group (container) (typed FeaturePython)
  Dunit = g/cm3
  Dvalue = 1.23
  Group = -> [C_element130,H_element120,Cl_element030]
  conduct = 2
  density = 1
  expand = 3
  formula = G4_NEOPRENE
  name = G4_NEOPRENE
  specific = 4
FEATURE [App::DocumentObjectGroupPython] Space  # scripted group (container) (typed FeaturePython)
  Group = -> [G4_KEVLAR,G4_DACRON,G4_NEOPRENE]
FEATURE [App::DocumentObjectGroupPython] H_element121  label="H_element : 068"  # scripted group (container) (typed FeaturePython)
  n = 5
  ref = H_element
FEATURE [App::DocumentObjectGroupPython] C_element131  label="C_element : 076"  # scripted group (container) (typed FeaturePython)
  n = 4
  ref = C_element
FEATURE [App::DocumentObjectGroupPython] N_element051  label="N_element : 3"  # scripted group (container) (typed FeaturePython)
  n = 3
  ref = N_element
FEATURE [App::DocumentObjectGroupPython] O_element113  label="O_element : 066"  # scripted group (container) (typed FeaturePython)
  n = 1
  ref = O_element
FEATURE [App::DocumentObjectGroupPython] G4_CYTOSINE  # scripted group (container) (typed FeaturePython)
  Dunit = g/cm3
  Dvalue = 1.55
  Group = -> [H_element121,C_element131,N_element051,O_element113]
  conduct = 2
  density = 1
  expand = 3
  formula = G4_CYTOSINE
  name = G4_CYTOSINE
  specific = 4
FEATURE [App::DocumentObjectGroupPython] H_element122  label="H_element : 069"  # scripted group (container) (typed FeaturePython)
  n = 6
  ref = H_element
FEATURE [App::DocumentObjectGroupPython] C_element132  label="C_element : 077"  # scripted group (container) (typed FeaturePython)
  n = 5
  ref = C_element
FEATURE [App::DocumentObjectGroupPython] N_element052  label="N_element : 024"  # scripted group (container) (typed FeaturePython)
  n = 2
  ref = N_element
FEATURE [App::DocumentObjectGroupPython] O_element114  label="O_element : 067"  # scripted group (container) (typed FeaturePython)
  n = 2
  ref = O_element
FEATURE [App::DocumentObjectGroupPython] G4_THYMINE  # scripted group (container) (typed FeaturePython)
  Dunit = g/cm3
  Dvalue = 1.23
  Group = -> [H_element122,C_element132,N_element052,O_element114]
  conduct = 2
  density = 1
  expand = 3
  formula = G4_THYMINE
  name = G4_THYMINE
  specific = 4
FEATURE [App::DocumentObjectGroupPython] H_element123  label="H_element : 070"  # scripted group (container) (typed FeaturePython)
  n = 4
  ref = H_element
FEATURE [App::DocumentObjectGroupPython] C_element133  label="C_element : 078"  # scripted group (container) (typed FeaturePython)
  n = 4
  ref = C_element
FEATURE [App::DocumentObjectGroupPython] N_element053  label="N_element : 025"  # scripted group (container) (typed FeaturePython)
  n = 2
  ref = N_element
FEATURE [App::DocumentObjectGroupPython] O_element115  label="O_element : 068"  # scripted group (container) (typed FeaturePython)
  n = 2
  ref = O_element
FEATURE [App::DocumentObjectGroupPython] G4_URACIL  # scripted group (container) (typed FeaturePython)
  Dunit = g/cm3
  Dvalue = 1.32
  Group = -> [H_element123,C_element133,N_element053,O_element115]
  conduct = 2
  density = 1
  expand = 3
  formula = G4_URACIL
  name = G4_URACIL
  specific = 4
FEATURE [App::DocumentObjectGroupPython] H_element124  label="H_element : 071"  # scripted group (container) (typed FeaturePython)
  n = 4
  ref = H_element
FEATURE [App::DocumentObjectGroupPython] C_element134  label="C_element : 079"  # scripted group (container) (typed FeaturePython)
  n = 5
  ref = C_element
FEATURE [App::DocumentObjectGroupPython] N_element054  label="N_element : 026"  # scripted group (container) (typed FeaturePython)
  n = 5
  ref = N_element
FEATURE [App::DocumentObjectGroupPython] G4_DNA_ADENINE  # scripted group (container) (typed FeaturePython)
  Dunit = g/cm3
  Dvalue = 1
  Group = -> [H_element124,C_element134,N_element054]
  conduct = 2
  density = 1
  expand = 3
  formula = G4_DNA_ADENINE
  name = G4_DNA_ADENINE
  specific = 4
FEATURE [App::DocumentObjectGroupPython] H_element125  label="H_element : 072"  # scripted group (container) (typed FeaturePython)
  n = 4
  ref = H_element
FEATURE [App::DocumentObjectGroupPython] C_element135  label="C_element : 080"  # scripted group (container) (typed FeaturePython)
  n = 5
  ref = C_element
FEATURE [App::DocumentObjectGroupPython] N_element055  label="N_element : 027"  # scripted group (container) (typed FeaturePython)
  n = 5
  ref = N_element
FEATURE [App::DocumentObjectGroupPython] O_element116  label="O_element : 069"  # scripted group (container) (typed FeaturePython)
  n = 1
  ref = O_element
FEATURE [App::DocumentObjectGroupPython] G4_DNA_GUANINE  # scripted group (container) (typed FeaturePython)
  Dunit = g/cm3
  Dvalue = 1
  Group = -> [H_element125,C_element135,N_element055,O_element116]
  conduct = 2
  density = 1
  expand = 3
  formula = G4_DNA_GUANINE
  name = G4_DNA_GUANINE
  specific = 4
FEATURE [App::DocumentObjectGroupPython] H_element126  label="H_element : 073"  # scripted group (container) (typed FeaturePython)
  n = 4
  ref = H_element
FEATURE [App::DocumentObjectGroupPython] C_element136  label="C_element : 081"  # scripted group (container) (typed FeaturePython)
  n = 4
  ref = C_element
FEATURE [App::DocumentObjectGroupPython] N_element056  label="N_element : 028"  # scripted group (container) (typed FeaturePython)
  n = 3
  ref = N_element
FEATURE [App::DocumentObjectGroupPython] O_element117  label="O_element : 070"  # scripted group (container) (typed FeaturePython)
  n = 1
  ref = O_element
FEATURE [App::DocumentObjectGroupPython] G4_DNA_CYTOSINE  # scripted group (container) (typed FeaturePython)
  Dunit = g/cm3
  Dvalue = 1
  Group = -> [H_element126,C_element136,N_element056,O_element117]
  conduct = 2
  density = 1
  expand = 3
  formula = G4_DNA_CYTOSINE
  name = G4_DNA_CYTOSINE
  specific = 4
FEATURE [App::DocumentObjectGroupPython] H_element127  label="H_element : 074"  # scripted group (container) (typed FeaturePython)
  n = 5
  ref = H_element
FEATURE [App::DocumentObjectGroupPython] C_element137  label="C_element : 082"  # scripted group (container) (typed FeaturePython)
  n = 5
  ref = C_element
FEATURE [App::DocumentObjectGroupPython] N_element057  label="N_element : 029"  # scripted group (container) (typed FeaturePython)
  n = 2
  ref = N_element
FEATURE [App::DocumentObjectGroupPython] O_element118  label="O_element : 071"  # scripted group (container) (typed FeaturePython)
  n = 2
  ref = O_element
FEATURE [App::DocumentObjectGroupPython] G4_DNA_THYMINE  # scripted group (container) (typed FeaturePython)
  Dunit = g/cm3
  Dvalue = 1
  Group = -> [H_element127,C_element137,N_element057,O_element118]
  conduct = 2
  density = 1
  expand = 3
  formula = G4_DNA_THYMINE
  name = G4_DNA_THYMINE
  specific = 4
FEATURE [App::DocumentObjectGroupPython] H_element128  label="H_element : 075"  # scripted group (container) (typed FeaturePython)
  n = 3
  ref = H_element
FEATURE [App::DocumentObjectGroupPython] C_element138  label="C_element : 083"  # scripted group (container) (typed FeaturePython)
  n = 4
  ref = C_element
FEATURE [App::DocumentObjectGroupPython] N_element058  label="N_element : 030"  # scripted group (container) (typed FeaturePython)
  n = 2
  ref = N_element
FEATURE [App::DocumentObjectGroupPython] O_element119  label="O_element : 072"  # scripted group (container) (typed FeaturePython)
  n = 2
  ref = O_element
FEATURE [App::DocumentObjectGroupPython] G4_DNA_URACIL  # scripted group (container) (typed FeaturePython)
  Dunit = g/cm3
  Dvalue = 1
  Group = -> [H_element128,C_element138,N_element058,O_element119]
  conduct = 2
  density = 1
  expand = 3
  formula = G4_DNA_URACIL
  name = G4_DNA_URACIL
  specific = 4
FEATURE [App::DocumentObjectGroupPython] H_element129  label="H_element : 076"  # scripted group (container) (typed FeaturePython)
  n = 10
  ref = H_element
FEATURE [App::DocumentObjectGroupPython] C_element139  label="C_element : 084"  # scripted group (container) (typed FeaturePython)
  n = 10
  ref = C_element
FEATURE [App::DocumentObjectGroupPython] N_element059  label="N_element : 031"  # scripted group (container) (typed FeaturePython)
  n = 5
  ref = N_element
FEATURE [App::DocumentObjectGroupPython] O_element120  label="O_element : 073"  # scripted group (container) (typed FeaturePython)
  n = 4
  ref = O_element
FEATURE [App::DocumentObjectGroupPython] G4_DNA_ADENOSINE  # scripted group (container) (typed FeaturePython)
  Dunit = g/cm3
  Dvalue = 1
  Group = -> [H_element129,C_element139,N_element059,O_element120]
  conduct = 2
  density = 1
  expand = 3
  formula = G4_DNA_ADENOSINE
  name = G4_DNA_ADENOSINE
  specific = 4
FEATURE [App::DocumentObjectGroupPython] H_element130  label="H_element : 077"  # scripted group (container) (typed FeaturePython)
  n = 10
  ref = H_element
FEATURE [App::DocumentObjectGroupPython] C_element140  label="C_element : 085"  # scripted group (container) (typed FeaturePython)
  n = 10
  ref = C_element
FEATURE [App::DocumentObjectGroupPython] N_element060  label="N_element : 032"  # scripted group (container) (typed FeaturePython)
  n = 5
  ref = N_element
FEATURE [App::DocumentObjectGroupPython] O_element121  label="O_element : 074"  # scripted group (container) (typed FeaturePython)
  n = 5
  ref = O_element
FEATURE [App::DocumentObjectGroupPython] G4_DNA_GUANOSINE  # scripted group (container) (typed FeaturePython)
  Dunit = g/cm3
  Dvalue = 1
  Group = -> [H_element130,C_element140,N_element060,O_element121]
  conduct = 2
  density = 1
  expand = 3
  formula = G4_DNA_GUANOSINE
  name = G4_DNA_GUANOSINE
  specific = 4
FEATURE [App::DocumentObjectGroupPython] H_element131  label="H_element : 078"  # scripted group (container) (typed FeaturePython)
  n = 10
  ref = H_element
FEATURE [App::DocumentObjectGroupPython] C_element141  label="C_element : 086"  # scripted group (container) (typed FeaturePython)
  n = 9
  ref = C_element
FEATURE [App::DocumentObjectGroupPython] N_element061  label="N_element : 033"  # scripted group (container) (typed FeaturePython)
  n = 3
  ref = N_element
FEATURE [App::DocumentObjectGroupPython] O_element122  label="O_element : 075"  # scripted group (container) (typed FeaturePython)
  n = 5
  ref = O_element
FEATURE [App::DocumentObjectGroupPython] G4_DNA_CYTIDINE  # scripted group (container) (typed FeaturePython)
  Dunit = g/cm3
  Dvalue = 1
  Group = -> [H_element131,C_element141,N_element061,O_element122]
  conduct = 2
  density = 1
  expand = 3
  formula = G4_DNA_CYTIDINE
  name = G4_DNA_CYTIDINE
  specific = 4
FEATURE [App::DocumentObjectGroupPython] H_element132  label="H_element : 079"  # scripted group (container) (typed FeaturePython)
  n = 9
  ref = H_element
FEATURE [App::DocumentObjectGroupPython] C_element142  label="C_element : 087"  # scripted group (container) (typed FeaturePython)
  n = 9
  ref = C_element
FEATURE [App::DocumentObjectGroupPython] N_element062  label="N_element : 034"  # scripted group (container) (typed FeaturePython)
  n = 2
  ref = N_element
FEATURE [App::DocumentObjectGroupPython] O_element123  label="O_element : 076"  # scripted group (container) (typed FeaturePython)
  n = 6
  ref = O_element
FEATURE [App::DocumentObjectGroupPython] G4_DNA_URIDINE  # scripted group (container) (typed FeaturePython)
  Dunit = g/cm3
  Dvalue = 1
  Group = -> [H_element132,C_element142,N_element062,O_element123]
  conduct = 2
  density = 1
  expand = 3
  formula = G4_DNA_URIDINE
  name = G4_DNA_URIDINE
  specific = 4
FEATURE [App::DocumentObjectGroupPython] H_element133  label="H_element : 080"  # scripted group (container) (typed FeaturePython)
  n = 11
  ref = H_element
FEATURE [App::DocumentObjectGroupPython] C_element143  label="C_element : 088"  # scripted group (container) (typed FeaturePython)
  n = 10
  ref = C_element
FEATURE [App::DocumentObjectGroupPython] N_element063  label="N_element : 035"  # scripted group (container) (typed FeaturePython)
  n = 2
  ref = N_element
FEATURE [App::DocumentObjectGroupPython] O_element124  label="O_element : 077"  # scripted group (container) (typed FeaturePython)
  n = 6
  ref = O_element
FEATURE [App::DocumentObjectGroupPython] G4_DNA_METHYLURIDINE  # scripted group (container) (typed FeaturePython)
  Dunit = g/cm3
  Dvalue = 1
  Group = -> [H_element133,C_element143,N_element063,O_element124]
  conduct = 2
  density = 1
  expand = 3
  formula = G4_DNA_METHYLURIDINE
  name = G4_DNA_METHYLURIDINE
  specific = 4
FEATURE [App::DocumentObjectGroupPython] P_element014  label="P_element : 003"  # scripted group (container) (typed FeaturePython)
  n = 1
  ref = P_element
FEATURE [App::DocumentObjectGroupPython] O_element125  label="O_element : 078"  # scripted group (container) (typed FeaturePython)
  n = 3
  ref = O_element
FEATURE [App::DocumentObjectGroupPython] G4_DNA_MONOPHOSPHATE  # scripted group (container) (typed FeaturePython)
  Dunit = g/cm3
  Dvalue = 1
  Group = -> [P_element014,O_element125]
  conduct = 2
  density = 1
  expand = 3
  formula = G4_DNA_MONOPHOSPHATE
  name = G4_DNA_MONOPHOSPHATE
  specific = 4
FEATURE [App::DocumentObjectGroupPython] H_element134  label="H_element : 081"  # scripted group (container) (typed FeaturePython)
  n = 10
  ref = H_element
FEATURE [App::DocumentObjectGroupPython] C_element144  label="C_element : 089"  # scripted group (container) (typed FeaturePython)
  n = 10
  ref = C_element
FEATURE [App::DocumentObjectGroupPython] N_element064  label="N_element : 036"  # scripted group (container) (typed FeaturePython)
  n = 5
  ref = N_element
FEATURE [App::DocumentObjectGroupPython] O_element126  label="O_element : 079"  # scripted group (container) (typed FeaturePython)
  n = 7
  ref = O_element
FEATURE [App::DocumentObjectGroupPython] P_element015  label="P_element : 004"  # scripted group (container) (typed FeaturePython)
  n = 1
  ref = P_element
FEATURE [App::DocumentObjectGroupPython] G4_DNA_A  # scripted group (container) (typed FeaturePython)
  Dunit = g/cm3
  Dvalue = 1
  Group = -> [H_element134,C_element144,N_element064,O_element126,P_element015]
  conduct = 2
  density = 1
  expand = 3
  formula = G4_DNA_A
  name = G4_DNA_A
  specific = 4
FEATURE [App::DocumentObjectGroupPython] H_element135  label="H_element : 082"  # scripted group (container) (typed FeaturePython)
  n = 10
  ref = H_element
FEATURE [App::DocumentObjectGroupPython] C_element145  label="C_element : 090"  # scripted group (container) (typed FeaturePython)
  n = 10
  ref = C_element
FEATURE [App::DocumentObjectGroupPython] N_element065  label="N_element : 037"  # scripted group (container) (typed FeaturePython)
  n = 5
  ref = N_element
FEATURE [App::DocumentObjectGroupPython] O_element127  label="O_element : 8"  # scripted group (container) (typed FeaturePython)
  n = 8
  ref = O_element
FEATURE [App::DocumentObjectGroupPython] P_element016  label="P_element : 005"  # scripted group (container) (typed FeaturePython)
  n = 1
  ref = P_element
FEATURE [App::DocumentObjectGroupPython] G4_DNA_G  # scripted group (container) (typed FeaturePython)
  Dunit = g/cm3
  Dvalue = 1
  Group = -> [H_element135,C_element145,N_element065,O_element127,P_element016]
  conduct = 2
  density = 1
  expand = 3
  formula = G4_DNA_G
  name = G4_DNA_G
  specific = 4
FEATURE [App::DocumentObjectGroupPython] H_element136  label="H_element : 083"  # scripted group (container) (typed FeaturePython)
  n = 10
  ref = H_element
FEATURE [App::DocumentObjectGroupPython] C_element146  label="C_element : 091"  # scripted group (container) (typed FeaturePython)
  n = 9
  ref = C_element
FEATURE [App::DocumentObjectGroupPython] N_element066  label="N_element : 038"  # scripted group (container) (typed FeaturePython)
  n = 3
  ref = N_element
FEATURE [App::DocumentObjectGroupPython] O_element128  label="O_element : 080"  # scripted group (container) (typed FeaturePython)
  n = 8
  ref = O_element
FEATURE [App::DocumentObjectGroupPython] P_element017  label="P_element : 006"  # scripted group (container) (typed FeaturePython)
  n = 1
  ref = P_element
FEATURE [App::DocumentObjectGroupPython] G4_DNA_C  # scripted group (container) (typed FeaturePython)
  Dunit = g/cm3
  Dvalue = 1
  Group = -> [H_element136,C_element146,N_element066,O_element128,P_element017]
  conduct = 2
  density = 1
  expand = 3
  formula = G4_DNA_C
  name = G4_DNA_C
  specific = 4
FEATURE [App::DocumentObjectGroupPython] H_element137  label="H_element : 084"  # scripted group (container) (typed FeaturePython)
  n = 9
  ref = H_element
FEATURE [App::DocumentObjectGroupPython] C_element147  label="C_element : 092"  # scripted group (container) (typed FeaturePython)
  n = 9
  ref = C_element
FEATURE [App::DocumentObjectGroupPython] N_element067  label="N_element : 039"  # scripted group (container) (typed FeaturePython)
  n = 2
  ref = N_element
FEATURE [App::DocumentObjectGroupPython] O_element129  label="O_element : 9"  # scripted group (container) (typed FeaturePython)
  n = 9
  ref = O_element
FEATURE [App::DocumentObjectGroupPython] P_element018  label="P_element : 007"  # scripted group (container) (typed FeaturePython)
  n = 1
  ref = P_element
FEATURE [App::DocumentObjectGroupPython] G4_DNA_U  # scripted group (container) (typed FeaturePython)
  Dunit = g/cm3
  Dvalue = 1
  Group = -> [H_element137,C_element147,N_element067,O_element129,P_element018]
  conduct = 2
  density = 1
  expand = 3
  formula = G4_DNA_U
  name = G4_DNA_U
  specific = 4
FEATURE [App::DocumentObjectGroupPython] H_element138  label="H_element : 085"  # scripted group (container) (typed FeaturePython)
  n = 11
  ref = H_element
FEATURE [App::DocumentObjectGroupPython] C_element148  label="C_element : 093"  # scripted group (container) (typed FeaturePython)
  n = 10
  ref = C_element
FEATURE [App::DocumentObjectGroupPython] N_element068  label="N_element : 040"  # scripted group (container) (typed FeaturePython)
  n = 2
  ref = N_element
FEATURE [App::DocumentObjectGroupPython] O_element130  label="O_element : 081"  # scripted group (container) (typed FeaturePython)
  n = 9
  ref = O_element
FEATURE [App::DocumentObjectGroupPython] P_element019  label="P_element : 008"  # scripted group (container) (typed FeaturePython)
  n = 1
  ref = P_element
FEATURE [App::DocumentObjectGroupPython] G4_DNA_MU  # scripted group (container) (typed FeaturePython)
  Dunit = g/cm3
  Dvalue = 1
  Group = -> [H_element138,C_element148,N_element068,O_element130,P_element019]
  conduct = 2
  density = 1
  expand = 3
  formula = G4_DNA_MU
  name = G4_DNA_MU
  specific = 4
FEATURE [App::DocumentObjectGroupPython] BioChemical  # scripted group (container) (typed FeaturePython)
  Group = -> [G4_CYTOSINE,G4_THYMINE,G4_URACIL,G4_DNA_ADENINE,G4_DNA_GUANINE,G4_DNA_CYTOSINE,G4_DNA_THYMINE,G4_DNA_URACIL,G4_DNA_ADENOSINE,G4_DNA_GUANOSINE,G4_DNA_CYTIDINE,G4_DNA_URIDINE,G4_DNA_METHYLURIDINE,G4_DNA_MONOPHOSPHATE,G4_DNA_A,G4_DNA_G,G4_DNA_C,G4_DNA_U,G4_DNA_MU]
FEATURE [App::DocumentObjectGroupPython] G4Materials  # scripted group (container) (typed FeaturePython)
  Group = -> [NIST,Element,HEP,Space,BioChemical]
  version = 1
FEATURE [App::DocumentObjectGroupPython] Geant4  # scripted group (container) (typed FeaturePython)
  Group = -> [G4Isotopes,G4Elements,G4Materials]
FEATURE [App::DocumentObjectGroupPython] Materials  # scripted group (container) (typed FeaturePython)
  Group = -> [Geant4]
FEATURE [Part::FeaturePython] GDMLBox_WorldBox  # WARN: FeaturePython — macro-defined, semantics opaque (R4)
  lunit = 2
  material = 5
  x = 100
  y = 100
  z = 100
FEATURE [Part::FeaturePython] GDMLBox_Box  # WARN: FeaturePython — macro-defined, semantics opaque (R4)
  lunit = 2
  material = 0
  x = 5
  y = 5
  z = 5
FEATURE [App::Part] LV_Box
  Group = -> [GDMLBox_Box]
  Origin = -> Origin001
  Placement = pos=(10,0,0) rot=(0,0,1;0rad)
FEATURE [Part::FeaturePython] Array  # Draft array (typed FeaturePython)
  Angle = 360
  ArrayType = 1
  Axis = (0,0,1)
  Base = -> LV_Box
  Center = (0,0,0)
  Count = 5
  Fuse = false
  IntervalAxis = (0,0,0)
  IntervalX = (50,0,0)
  IntervalY = (0,50,0)
  IntervalZ = (0,0,50)
  NumberCircles = 3
  NumberPolar = 5
  NumberX = 2
  NumberY = 2
  NumberZ = 1
  RadialDistance = 50
  Symmetry = 1
  TangentialDistance = 25
FEATURE [Part::FeaturePython] Array001  # Draft array (typed FeaturePython)
  Angle = 360
  ArrayType = 0
  Axis = (0,0,1)
  Base = -> Array
  Center = (0,0,0)
  Count = 4
  Fuse = false
  IntervalAxis = (0,0,0)
  IntervalX = (50,0,0)
  IntervalY = (0,30,0)
  IntervalZ = (0,0,100)
  NumberCircles = 3
  NumberPolar = 5
  NumberX = 2
  NumberY = 2
  NumberZ = 1
  Placement = pos=(-20,-14,0) rot=(0,0,1;0rad)
  RadialDistance = 50
  Symmetry = 1
  TangentialDistance = 25
FEATURE [App::Part] Part
  Group = -> [LV_Box,Array,Array001]
  Origin = -> Origin002
FEATURE [App::Part] worldVOL
  Group = -> [GDMLBox_WorldBox,Part]
  Origin = -> Origin
